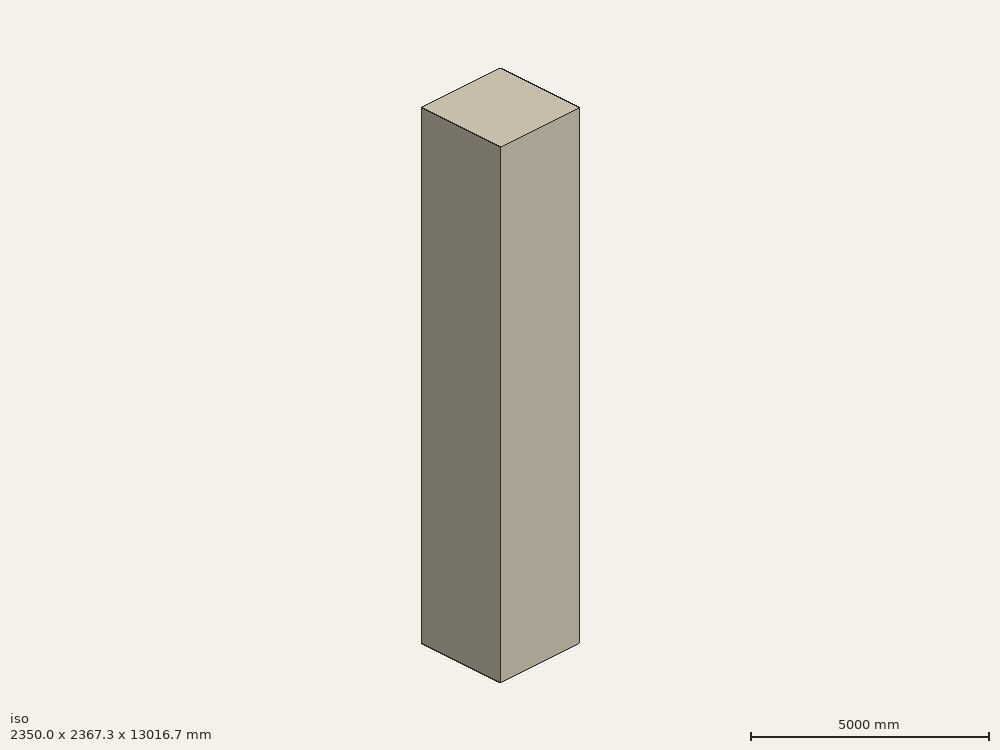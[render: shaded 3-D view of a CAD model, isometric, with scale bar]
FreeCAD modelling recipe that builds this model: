
FCSTD DOCUMENT  (FreeCAD 1.0R39109 (Git))
Label: revolveTester-6-a
License: All rights reserved
objects: App::DocumentObjectGroupPython×1252, Spreadsheet::Sheet×2, App::Part×2, Part::FeaturePython×1, Part::Cylinder×1, Sketcher::SketchObject×1, Part::Revolution×1, Part::Cut×1
note: 6 computed .brp shape members not serialized (recipe doc carries the construction recipe); baked Part::Feature solids carry a one-line shape summary decoded from their .brp

FEATURE [Spreadsheet::Sheet] defines
  cells = A1='constant; B1='HALFPI; C1(HALFPI)==pi / 2; A2='constant; B2='PI; C2(PI)==1 * pi; A3='constant; B3='TWOPI; C3(TWOPI)==2 * pi
FEATURE [Spreadsheet::Sheet] gdmlInfo
FEATURE [App::DocumentObjectGroupPython] Define  # scripted group (container) (typed FeaturePython)
  Group = -> [defines,gdmlInfo]
FEATURE [App::DocumentObjectGroupPython] HALFPI  # scripted group (container) (typed FeaturePython)
  name = HALFPI
  value = pi/2.
FEATURE [App::DocumentObjectGroupPython] PI  # scripted group (container) (typed FeaturePython)
  name = PI
  value = 1.*pi
FEATURE [App::DocumentObjectGroupPython] TWOPI  # scripted group (container) (typed FeaturePython)
  name = TWOPI
  value = 2.*pi
FEATURE [App::DocumentObjectGroupPython] Constants  # scripted group (container) (typed FeaturePython)
  Group = -> [HALFPI,PI,TWOPI]
FEATURE [App::DocumentObjectGroupPython] Quantities  # scripted group (container) (typed FeaturePython)
FEATURE [App::DocumentObjectGroupPython] Variables  # scripted group (container) (typed FeaturePython)
FEATURE [App::DocumentObjectGroupPython] Isotopes  # scripted group (container) (typed FeaturePython)
FEATURE [App::DocumentObjectGroupPython] Elements  # scripted group (container) (typed FeaturePython)
FEATURE [App::DocumentObjectGroupPython] Matrix  # scripted group (container) (typed FeaturePython)
FEATURE [App::DocumentObjectGroupPython] Surfaces  # scripted group (container) (typed FeaturePython)
FEATURE [App::DocumentObjectGroupPython] Opticals  # scripted group (container) (typed FeaturePython)
  Group = -> [Matrix,Surfaces]
FEATURE [App::DocumentObjectGroupPython] G4Isotopes  # scripted group (container) (typed FeaturePython)
FEATURE [App::DocumentObjectGroupPython] H_element  # scripted group (container) (typed FeaturePython)
  Z = 1
  atom_value = 1.008
  formula = H
  name = H_element
FEATURE [App::DocumentObjectGroupPython] He_element  # scripted group (container) (typed FeaturePython)
  Z = 2
  atom_value = 4.0026
  formula = He
  name = He_element
FEATURE [App::DocumentObjectGroupPython] Li_element  # scripted group (container) (typed FeaturePython)
  Z = 3
  atom_value = 6.94
  formula = Li
  name = Li_element
FEATURE [App::DocumentObjectGroupPython] Be_element  # scripted group (container) (typed FeaturePython)
  Z = 4
  atom_value = 9.01218
  formula = Be
  name = Be_element
FEATURE [App::DocumentObjectGroupPython] B_element  # scripted group (container) (typed FeaturePython)
  Z = 5
  atom_value = 10.81
  formula = B
  name = B_element
FEATURE [App::DocumentObjectGroupPython] C_element  # scripted group (container) (typed FeaturePython)
  Z = 6
  atom_value = 12.011
  formula = C
  name = C_element
FEATURE [App::DocumentObjectGroupPython] N_element  # scripted group (container) (typed FeaturePython)
  Z = 7
  atom_value = 14.007
  formula = N
  name = N_element
FEATURE [App::DocumentObjectGroupPython] O_element  # scripted group (container) (typed FeaturePython)
  Z = 8
  atom_value = 15.999
  formula = O
  name = O_element
FEATURE [App::DocumentObjectGroupPython] F_element  # scripted group (container) (typed FeaturePython)
  Z = 9
  atom_value = 18.9984
  formula = F
  name = F_element
FEATURE [App::DocumentObjectGroupPython] Ne_element  # scripted group (container) (typed FeaturePython)
  Z = 10
  atom_value = 20.1797
  formula = Ne
  name = Ne_element
FEATURE [App::DocumentObjectGroupPython] Na_element  # scripted group (container) (typed FeaturePython)
  Z = 11
  atom_value = 22.9898
  formula = Na
  name = Na_element
FEATURE [App::DocumentObjectGroupPython] Mg_element  # scripted group (container) (typed FeaturePython)
  Z = 12
  atom_value = 24.305
  formula = Mg
  name = Mg_element
FEATURE [App::DocumentObjectGroupPython] Al_element  # scripted group (container) (typed FeaturePython)
  Z = 13
  atom_value = 26.9815
  formula = Al
  name = Al_element
FEATURE [App::DocumentObjectGroupPython] Si_element  # scripted group (container) (typed FeaturePython)
  Z = 14
  atom_value = 28.085
  formula = Si
  name = Si_element
FEATURE [App::DocumentObjectGroupPython] P_element  # scripted group (container) (typed FeaturePython)
  Z = 15
  atom_value = 30.9738
  formula = P
  name = P_element
FEATURE [App::DocumentObjectGroupPython] S_element  # scripted group (container) (typed FeaturePython)
  Z = 16
  atom_value = 32.06
  formula = S
  name = S_element
FEATURE [App::DocumentObjectGroupPython] Cl_element  # scripted group (container) (typed FeaturePython)
  Z = 17
  atom_value = 35.45
  formula = Cl
  name = Cl_element
FEATURE [App::DocumentObjectGroupPython] Ar_element  # scripted group (container) (typed FeaturePython)
  Z = 18
  atom_value = 39.95
  formula = Ar
  name = Ar_element
FEATURE [App::DocumentObjectGroupPython] K_element  # scripted group (container) (typed FeaturePython)
  Z = 19
  atom_value = 39.0983
  formula = K
  name = K_element
FEATURE [App::DocumentObjectGroupPython] Ca_element  # scripted group (container) (typed FeaturePython)
  Z = 20
  atom_value = 40.078
  formula = Ca
  name = Ca_element
FEATURE [App::DocumentObjectGroupPython] Sc_element  # scripted group (container) (typed FeaturePython)
  Z = 21
  atom_value = 44.9559
  formula = Sc
  name = Sc_element
FEATURE [App::DocumentObjectGroupPython] Ti_element  # scripted group (container) (typed FeaturePython)
  Z = 22
  atom_value = 47.867
  formula = Ti
  name = Ti_element
FEATURE [App::DocumentObjectGroupPython] V_element  # scripted group (container) (typed FeaturePython)
  Z = 23
  atom_value = 50.9415
  formula = V
  name = V_element
FEATURE [App::DocumentObjectGroupPython] Cr_element  # scripted group (container) (typed FeaturePython)
  Z = 24
  atom_value = 51.9961
  formula = Cr
  name = Cr_element
FEATURE [App::DocumentObjectGroupPython] Mn_element  # scripted group (container) (typed FeaturePython)
  Z = 25
  atom_value = 54.938
  formula = Mn
  name = Mn_element
FEATURE [App::DocumentObjectGroupPython] Fe_element  # scripted group (container) (typed FeaturePython)
  Z = 26
  atom_value = 55.845
  formula = Fe
  name = Fe_element
FEATURE [App::DocumentObjectGroupPython] Co_element  # scripted group (container) (typed FeaturePython)
  Z = 27
  atom_value = 58.9332
  formula = Co
  name = Co_element
FEATURE [App::DocumentObjectGroupPython] Ni_element  # scripted group (container) (typed FeaturePython)
  Z = 28
  atom_value = 58.6934
  formula = Ni
  name = Ni_element
FEATURE [App::DocumentObjectGroupPython] Cu_element  # scripted group (container) (typed FeaturePython)
  Z = 29
  atom_value = 63.546
  formula = Cu
  name = Cu_element
FEATURE [App::DocumentObjectGroupPython] Zn_element  # scripted group (container) (typed FeaturePython)
  Z = 30
  atom_value = 65.38
  formula = Zn
  name = Zn_element
FEATURE [App::DocumentObjectGroupPython] Ga_element  # scripted group (container) (typed FeaturePython)
  Z = 31
  atom_value = 69.723
  formula = Ga
  name = Ga_element
FEATURE [App::DocumentObjectGroupPython] Ge_element  # scripted group (container) (typed FeaturePython)
  Z = 32
  atom_value = 72.63
  formula = Ge
  name = Ge_element
FEATURE [App::DocumentObjectGroupPython] As_element  # scripted group (container) (typed FeaturePython)
  Z = 33
  atom_value = 74.9216
  formula = As
  name = As_element
FEATURE [App::DocumentObjectGroupPython] Se_element  # scripted group (container) (typed FeaturePython)
  Z = 34
  atom_value = 78.971
  formula = Se
  name = Se_element
FEATURE [App::DocumentObjectGroupPython] Br_element  # scripted group (container) (typed FeaturePython)
  Z = 35
  atom_value = 79.904
  formula = Br
  name = Br_element
FEATURE [App::DocumentObjectGroupPython] Kr_element  # scripted group (container) (typed FeaturePython)
  Z = 36
  atom_value = 83.798
  formula = Kr
  name = Kr_element
FEATURE [App::DocumentObjectGroupPython] Rb_element  # scripted group (container) (typed FeaturePython)
  Z = 37
  atom_value = 85.4678
  formula = Rb
  name = Rb_element
FEATURE [App::DocumentObjectGroupPython] Sr_element  # scripted group (container) (typed FeaturePython)
  Z = 38
  atom_value = 87.62
  formula = Sr
  name = Sr_element
FEATURE [App::DocumentObjectGroupPython] Y_element  # scripted group (container) (typed FeaturePython)
  Z = 39
  atom_value = 88.9058
  formula = Y
  name = Y_element
FEATURE [App::DocumentObjectGroupPython] Zr_element  # scripted group (container) (typed FeaturePython)
  Z = 40
  atom_value = 91.224
  formula = Zr
  name = Zr_element
FEATURE [App::DocumentObjectGroupPython] Nb_element  # scripted group (container) (typed FeaturePython)
  Z = 41
  atom_value = 92.9064
  formula = Nb
  name = Nb_element
FEATURE [App::DocumentObjectGroupPython] Mo_element  # scripted group (container) (typed FeaturePython)
  Z = 42
  atom_value = 95.95
  formula = Mo
  name = Mo_element
FEATURE [App::DocumentObjectGroupPython] Tc_element  # scripted group (container) (typed FeaturePython)
  Z = 43
  atom_value = 97
  formula = Tc
  name = Tc_element
FEATURE [App::DocumentObjectGroupPython] Ru_element  # scripted group (container) (typed FeaturePython)
  Z = 44
  atom_value = 101.07
  formula = Ru
  name = Ru_element
FEATURE [App::DocumentObjectGroupPython] Rh_element  # scripted group (container) (typed FeaturePython)
  Z = 45
  atom_value = 102.905
  formula = Rh
  name = Rh_element
FEATURE [App::DocumentObjectGroupPython] Pd_element  # scripted group (container) (typed FeaturePython)
  Z = 46
  atom_value = 106.42
  formula = Pd
  name = Pd_element
FEATURE [App::DocumentObjectGroupPython] Ag_element  # scripted group (container) (typed FeaturePython)
  Z = 47
  atom_value = 107.868
  formula = Ag
  name = Ag_element
FEATURE [App::DocumentObjectGroupPython] Cd_element  # scripted group (container) (typed FeaturePython)
  Z = 48
  atom_value = 112.414
  formula = Cd
  name = Cd_element
FEATURE [App::DocumentObjectGroupPython] In_element  # scripted group (container) (typed FeaturePython)
  Z = 49
  atom_value = 114.818
  formula = In
  name = In_element
FEATURE [App::DocumentObjectGroupPython] Sn_element  # scripted group (container) (typed FeaturePython)
  Z = 50
  atom_value = 118.71
  formula = Sn
  name = Sn_element
FEATURE [App::DocumentObjectGroupPython] Sb_element  # scripted group (container) (typed FeaturePython)
  Z = 51
  atom_value = 121.76
  formula = Sb
  name = Sb_element
FEATURE [App::DocumentObjectGroupPython] Te_element  # scripted group (container) (typed FeaturePython)
  Z = 52
  atom_value = 127.6
  formula = Te
  name = Te_element
FEATURE [App::DocumentObjectGroupPython] I_element  # scripted group (container) (typed FeaturePython)
  Z = 53
  atom_value = 126.904
  formula = I
  name = I_element
FEATURE [App::DocumentObjectGroupPython] Xe_element  # scripted group (container) (typed FeaturePython)
  Z = 54
  atom_value = 131.293
  formula = Xe
  name = Xe_element
FEATURE [App::DocumentObjectGroupPython] Cs_element  # scripted group (container) (typed FeaturePython)
  Z = 55
  atom_value = 132.905
  formula = Cs
  name = Cs_element
FEATURE [App::DocumentObjectGroupPython] Ba_element  # scripted group (container) (typed FeaturePython)
  Z = 56
  atom_value = 137.327
  formula = Ba
  name = Ba_element
FEATURE [App::DocumentObjectGroupPython] La_element  # scripted group (container) (typed FeaturePython)
  Z = 57
  atom_value = 138.905
  formula = La
  name = La_element
FEATURE [App::DocumentObjectGroupPython] Ce_element  # scripted group (container) (typed FeaturePython)
  Z = 58
  atom_value = 140.116
  formula = Ce
  name = Ce_element
FEATURE [App::DocumentObjectGroupPython] Pr_element  # scripted group (container) (typed FeaturePython)
  Z = 59
  atom_value = 140.908
  formula = Pr
  name = Pr_element
FEATURE [App::DocumentObjectGroupPython] Nd_element  # scripted group (container) (typed FeaturePython)
  Z = 60
  atom_value = 144.242
  formula = Nd
  name = Nd_element
FEATURE [App::DocumentObjectGroupPython] Pm_element  # scripted group (container) (typed FeaturePython)
  Z = 61
  atom_value = 145
  formula = Pm
  name = Pm_element
FEATURE [App::DocumentObjectGroupPython] Sm_element  # scripted group (container) (typed FeaturePython)
  Z = 62
  atom_value = 150.36
  formula = Sm
  name = Sm_element
FEATURE [App::DocumentObjectGroupPython] Eu_element  # scripted group (container) (typed FeaturePython)
  Z = 63
  atom_value = 151.964
  formula = Eu
  name = Eu_element
FEATURE [App::DocumentObjectGroupPython] Gd_element  # scripted group (container) (typed FeaturePython)
  Z = 64
  atom_value = 157.25
  formula = Gd
  name = Gd_element
FEATURE [App::DocumentObjectGroupPython] Tb_element  # scripted group (container) (typed FeaturePython)
  Z = 65
  atom_value = 158.925
  formula = Tb
  name = Tb_element
FEATURE [App::DocumentObjectGroupPython] Dy_element  # scripted group (container) (typed FeaturePython)
  Z = 66
  atom_value = 162.5
  formula = Dy
  name = Dy_element
FEATURE [App::DocumentObjectGroupPython] Ho_element  # scripted group (container) (typed FeaturePython)
  Z = 67
  atom_value = 164.93
  formula = Ho
  name = Ho_element
FEATURE [App::DocumentObjectGroupPython] Er_element  # scripted group (container) (typed FeaturePython)
  Z = 68
  atom_value = 167.259
  formula = Er
  name = Er_element
FEATURE [App::DocumentObjectGroupPython] Tm_element  # scripted group (container) (typed FeaturePython)
  Z = 69
  atom_value = 168.934
  formula = Tm
  name = Tm_element
FEATURE [App::DocumentObjectGroupPython] Yb_element  # scripted group (container) (typed FeaturePython)
  Z = 70
  atom_value = 173.045
  formula = Yb
  name = Yb_element
FEATURE [App::DocumentObjectGroupPython] Lu_element  # scripted group (container) (typed FeaturePython)
  Z = 71
  atom_value = 174.967
  formula = Lu
  name = Lu_element
FEATURE [App::DocumentObjectGroupPython] Hf_element  # scripted group (container) (typed FeaturePython)
  Z = 72
  atom_value = 178.49
  formula = Hf
  name = Hf_element
FEATURE [App::DocumentObjectGroupPython] Ta_element  # scripted group (container) (typed FeaturePython)
  Z = 73
  atom_value = 180.948
  formula = Ta
  name = Ta_element
FEATURE [App::DocumentObjectGroupPython] W_element  # scripted group (container) (typed FeaturePython)
  Z = 74
  atom_value = 183.84
  formula = W
  name = W_element
FEATURE [App::DocumentObjectGroupPython] Re_element  # scripted group (container) (typed FeaturePython)
  Z = 75
  atom_value = 186.207
  formula = Re
  name = Re_element
FEATURE [App::DocumentObjectGroupPython] Os_element  # scripted group (container) (typed FeaturePython)
  Z = 76
  atom_value = 190.23
  formula = Os
  name = Os_element
FEATURE [App::DocumentObjectGroupPython] Ir_element  # scripted group (container) (typed FeaturePython)
  Z = 77
  atom_value = 192.217
  formula = Ir
  name = Ir_element
FEATURE [App::DocumentObjectGroupPython] Pt_element  # scripted group (container) (typed FeaturePython)
  Z = 78
  atom_value = 195.084
  formula = Pt
  name = Pt_element
FEATURE [App::DocumentObjectGroupPython] Au_element  # scripted group (container) (typed FeaturePython)
  Z = 79
  atom_value = 196.967
  formula = Au
  name = Au_element
FEATURE [App::DocumentObjectGroupPython] Hg_element  # scripted group (container) (typed FeaturePython)
  Z = 80
  atom_value = 200.592
  formula = Hg
  name = Hg_element
FEATURE [App::DocumentObjectGroupPython] Tl_element  # scripted group (container) (typed FeaturePython)
  Z = 81
  atom_value = 204.38
  formula = Tl
  name = Tl_element
FEATURE [App::DocumentObjectGroupPython] Pb_element  # scripted group (container) (typed FeaturePython)
  Z = 82
  atom_value = 207.2
  formula = Pb
  name = Pb_element
FEATURE [App::DocumentObjectGroupPython] Bi_element  # scripted group (container) (typed FeaturePython)
  Z = 83
  atom_value = 208.98
  formula = Bi
  name = Bi_element
FEATURE [App::DocumentObjectGroupPython] Po_element  # scripted group (container) (typed FeaturePython)
  Z = 84
  atom_value = 209
  formula = Po
  name = Po_element
FEATURE [App::DocumentObjectGroupPython] At_element  # scripted group (container) (typed FeaturePython)
  Z = 85
  atom_value = 210
  formula = At
  name = At_element
FEATURE [App::DocumentObjectGroupPython] Rn_element  # scripted group (container) (typed FeaturePython)
  Z = 86
  atom_value = 222
  formula = Rn
  name = Rn_element
FEATURE [App::DocumentObjectGroupPython] Fr_element  # scripted group (container) (typed FeaturePython)
  Z = 87
  atom_value = 223
  formula = Fr
  name = Fr_element
FEATURE [App::DocumentObjectGroupPython] Ra_element  # scripted group (container) (typed FeaturePython)
  Z = 88
  atom_value = 226
  formula = Ra
  name = Ra_element
FEATURE [App::DocumentObjectGroupPython] Ac_element  # scripted group (container) (typed FeaturePython)
  Z = 89
  atom_value = 227
  formula = Ac
  name = Ac_element
FEATURE [App::DocumentObjectGroupPython] Th_element  # scripted group (container) (typed FeaturePython)
  Z = 90
  atom_value = 232.038
  formula = Th
  name = Th_element
FEATURE [App::DocumentObjectGroupPython] Pa_element  # scripted group (container) (typed FeaturePython)
  Z = 91
  atom_value = 231.036
  formula = Pa
  name = Pa_element
FEATURE [App::DocumentObjectGroupPython] U_element  # scripted group (container) (typed FeaturePython)
  Z = 92
  atom_value = 238.029
  formula = U
  name = U_element
FEATURE [App::DocumentObjectGroupPython] Np_element  # scripted group (container) (typed FeaturePython)
  Z = 93
  atom_value = 237
  formula = Np
  name = Np_element
FEATURE [App::DocumentObjectGroupPython] Pu_element  # scripted group (container) (typed FeaturePython)
  Z = 94
  atom_value = 244
  formula = Pu
  name = Pu_element
FEATURE [App::DocumentObjectGroupPython] Am_element  # scripted group (container) (typed FeaturePython)
  Z = 95
  atom_value = 243
  formula = Am
  name = Am_element
FEATURE [App::DocumentObjectGroupPython] Cm_element  # scripted group (container) (typed FeaturePython)
  Z = 96
  atom_value = 247
  formula = Cm
  name = Cm_element
FEATURE [App::DocumentObjectGroupPython] Bk_element  # scripted group (container) (typed FeaturePython)
  Z = 97
  atom_value = 247
  formula = Bk
  name = Bk_element
FEATURE [App::DocumentObjectGroupPython] Cf_element  # scripted group (container) (typed FeaturePython)
  Z = 98
  atom_value = 251
  formula = Cf
  name = Cf_element
FEATURE [App::DocumentObjectGroupPython] G4Elements  # scripted group (container) (typed FeaturePython)
  Group = -> [H_element,He_element,Li_element,Be_element,B_element,C_element,N_element,O_element,F_element,Ne_element,Na_element,Mg_element,Al_element,Si_element,P_element,S_element,Cl_element,Ar_element,K_element,Ca_element,Sc_element,Ti_element,V_element,Cr_element,Mn_element,Fe_element,Co_element,Ni_element,Cu_element,Zn_element,Ga_element,Ge_element,As_element,Se_element,Br_element,Kr_element,Rb_element,+61 more]
FEATURE [App::DocumentObjectGroupPython] H_element001  label="H_element : 0.101"  # scripted group (container) (typed FeaturePython)
  n = 0.101327
FEATURE [App::DocumentObjectGroupPython] C_element001  label="C_element : 0.775"  # scripted group (container) (typed FeaturePython)
  n = 0.7755
FEATURE [App::DocumentObjectGroupPython] N_element001  label="N_element : 0.035"  # scripted group (container) (typed FeaturePython)
  n = 0.035057
FEATURE [App::DocumentObjectGroupPython] O_element001  label="O_element : 0.052"  # scripted group (container) (typed FeaturePython)
  n = 0.0523159
FEATURE [App::DocumentObjectGroupPython] F_element001  label="F_element : 0.017"  # scripted group (container) (typed FeaturePython)
  n = 0.017422
FEATURE [App::DocumentObjectGroupPython] Ca_element001  label="Ca_element : 0.018"  # scripted group (container) (typed FeaturePython)
  n = 0.018378
FEATURE [App::DocumentObjectGroupPython] G4_A_150_TISSUE  label="G4_A-150_TISSUE"  # scripted group (container) (typed FeaturePython)
  Dunit = g/cm3
  Dvalue = 1.127
  Group = -> [H_element001,C_element001,N_element001,O_element001,F_element001,Ca_element001]
  conduct = 2
  density = 1
  expand = 3
  formula = G4_A-150_TISSUE
  name = G4_A-150_TISSUE
  specific = 4
FEATURE [App::DocumentObjectGroupPython] C_element002  label="C_element : 3"  # scripted group (container) (typed FeaturePython)
  n = 3
  ref = C_element
FEATURE [App::DocumentObjectGroupPython] H_element002  label="H_element : 6"  # scripted group (container) (typed FeaturePython)
  n = 6
  ref = H_element
FEATURE [App::DocumentObjectGroupPython] O_element002  label="O_element : 1"  # scripted group (container) (typed FeaturePython)
  n = 1
  ref = O_element
FEATURE [App::DocumentObjectGroupPython] G4_ACETONE  # scripted group (container) (typed FeaturePython)
  Dunit = g/cm3
  Dvalue = 0.7899
  Group = -> [C_element002,H_element002,O_element002]
  conduct = 2
  density = 1
  expand = 3
  formula = G4_ACETONE
  name = G4_ACETONE
  specific = 4
FEATURE [App::DocumentObjectGroupPython] C_element003  label="C_element : 2"  # scripted group (container) (typed FeaturePython)
  n = 2
  ref = C_element
FEATURE [App::DocumentObjectGroupPython] H_element003  label="H_element : 2"  # scripted group (container) (typed FeaturePython)
  n = 2
  ref = H_element
FEATURE [App::DocumentObjectGroupPython] G4_ACETYLENE  # scripted group (container) (typed FeaturePython)
  Dunit = g/cm3
  Dvalue = 0.0010967
  Group = -> [C_element003,H_element003]
  conduct = 2
  density = 1
  expand = 3
  formula = G4_ACETYLENE
  name = G4_ACETYLENE
  specific = 4
FEATURE [App::DocumentObjectGroupPython] C_element004  label="C_element : 5"  # scripted group (container) (typed FeaturePython)
  n = 5
  ref = C_element
FEATURE [App::DocumentObjectGroupPython] H_element004  label="H_element : 5"  # scripted group (container) (typed FeaturePython)
  n = 5
  ref = H_element
FEATURE [App::DocumentObjectGroupPython] N_element002  label="N_element : 5"  # scripted group (container) (typed FeaturePython)
  n = 5
  ref = N_element
FEATURE [App::DocumentObjectGroupPython] G4_ADENINE  # scripted group (container) (typed FeaturePython)
  Dunit = g/cm3
  Dvalue = 1.6
  Group = -> [C_element004,H_element004,N_element002]
  conduct = 2
  density = 1
  expand = 3
  formula = G4_ADENINE
  name = G4_ADENINE
  specific = 4
FEATURE [App::DocumentObjectGroupPython] H_element005  label="H_element : 0.114"  # scripted group (container) (typed FeaturePython)
  n = 0.114
FEATURE [App::DocumentObjectGroupPython] C_element005  label="C_element : 0.598"  # scripted group (container) (typed FeaturePython)
  n = 0.598
FEATURE [App::DocumentObjectGroupPython] N_element003  label="N_element : 0.007"  # scripted group (container) (typed FeaturePython)
  n = 0.007
FEATURE [App::DocumentObjectGroupPython] O_element003  label="O_element : 0.278"  # scripted group (container) (typed FeaturePython)
  n = 0.278
FEATURE [App::DocumentObjectGroupPython] Na_element001  label="Na_element : 0.001"  # scripted group (container) (typed FeaturePython)
  n = 0.001
FEATURE [App::DocumentObjectGroupPython] S_element001  label="S_element : 0.001"  # scripted group (container) (typed FeaturePython)
  n = 0.001
FEATURE [App::DocumentObjectGroupPython] Cl_element001  label="Cl_element : 0.001"  # scripted group (container) (typed FeaturePython)
  n = 0.001
FEATURE [App::DocumentObjectGroupPython] G4_ADIPOSE_TISSUE_ICRP  # scripted group (container) (typed FeaturePython)
  Dunit = g/cm3
  Dvalue = 0.95
  Group = -> [H_element005,C_element005,N_element003,O_element003,Na_element001,S_element001,Cl_element001]
  conduct = 2
  density = 1
  expand = 3
  formula = G4_ADIPOSE_TISSUE_ICRP
  name = G4_ADIPOSE_TISSUE_ICRP
  specific = 4
FEATURE [App::DocumentObjectGroupPython] C_element006  label="C_element : 0.000"  # scripted group (container) (typed FeaturePython)
  n = 0.000124
FEATURE [App::DocumentObjectGroupPython] N_element004  label="N_element : 0.755"  # scripted group (container) (typed FeaturePython)
  n = 0.755268
FEATURE [App::DocumentObjectGroupPython] O_element004  label="O_element : 0.232"  # scripted group (container) (typed FeaturePython)
  n = 0.231781
FEATURE [App::DocumentObjectGroupPython] Ar_element001  label="Ar_element : 0.013"  # scripted group (container) (typed FeaturePython)
  n = 0.012827
FEATURE [App::DocumentObjectGroupPython] G4_AIR  # scripted group (container) (typed FeaturePython)
  Dunit = g/cm3
  Dvalue = 0.00120479
  Group = -> [C_element006,N_element004,O_element004,Ar_element001]
  conduct = 2
  density = 1
  expand = 3
  formula = G4_AIR
  name = G4_AIR
  specific = 4
FEATURE [App::DocumentObjectGroupPython] C_element007  label="C_element : 006"  # scripted group (container) (typed FeaturePython)
  n = 3
  ref = C_element
FEATURE [App::DocumentObjectGroupPython] H_element006  label="H_element : 7"  # scripted group (container) (typed FeaturePython)
  n = 7
  ref = H_element
FEATURE [App::DocumentObjectGroupPython] N_element005  label="N_element : 1"  # scripted group (container) (typed FeaturePython)
  n = 1
  ref = N_element
FEATURE [App::DocumentObjectGroupPython] O_element005  label="O_element : 2"  # scripted group (container) (typed FeaturePython)
  n = 2
  ref = O_element
FEATURE [App::DocumentObjectGroupPython] G4_ALANINE  # scripted group (container) (typed FeaturePython)
  Dunit = g/cm3
  Dvalue = 1.42
  Group = -> [C_element007,H_element006,N_element005,O_element005]
  conduct = 2
  density = 1
  expand = 3
  formula = G4_ALANINE
  name = G4_ALANINE
  specific = 4
FEATURE [App::DocumentObjectGroupPython] Al_element001  label="Al_element : 2"  # scripted group (container) (typed FeaturePython)
  n = 2
  ref = Al_element
FEATURE [App::DocumentObjectGroupPython] O_element006  label="O_element : 3"  # scripted group (container) (typed FeaturePython)
  n = 3
  ref = O_element
FEATURE [App::DocumentObjectGroupPython] G4_ALUMINUM_OXIDE  # scripted group (container) (typed FeaturePython)
  Dunit = g/cm3
  Dvalue = 3.97
  Group = -> [Al_element001,O_element006]
  conduct = 2
  density = 1
  expand = 3
  formula = G4_ALUMINUM_OXIDE
  name = G4_ALUMINUM_OXIDE
  specific = 4
FEATURE [App::DocumentObjectGroupPython] H_element007  label="H_element : 0.106"  # scripted group (container) (typed FeaturePython)
  n = 0.10593
FEATURE [App::DocumentObjectGroupPython] C_element008  label="C_element : 0.789"  # scripted group (container) (typed FeaturePython)
  n = 0.788974
FEATURE [App::DocumentObjectGroupPython] O_element007  label="O_element : 0.105"  # scripted group (container) (typed FeaturePython)
  n = 0.105096
FEATURE [App::DocumentObjectGroupPython] G4_AMBER  # scripted group (container) (typed FeaturePython)
  Dunit = g/cm3
  Dvalue = 1.1
  Group = -> [H_element007,C_element008,O_element007]
  conduct = 2
  density = 1
  expand = 3
  formula = G4_AMBER
  name = G4_AMBER
  specific = 4
FEATURE [App::DocumentObjectGroupPython] N_element006  label="N_element : 006"  # scripted group (container) (typed FeaturePython)
  n = 1
  ref = N_element
FEATURE [App::DocumentObjectGroupPython] H_element008  label="H_element : 3"  # scripted group (container) (typed FeaturePython)
  n = 3
  ref = H_element
FEATURE [App::DocumentObjectGroupPython] G4_AMMONIA  # scripted group (container) (typed FeaturePython)
  Dunit = g/cm3
  Dvalue = 0.000826019
  Group = -> [N_element006,H_element008]
  conduct = 2
  density = 1
  expand = 3
  formula = G4_AMMONIA
  name = G4_AMMONIA
  specific = 4
FEATURE [App::DocumentObjectGroupPython] C_element009  label="C_element : 6"  # scripted group (container) (typed FeaturePython)
  n = 6
  ref = C_element
FEATURE [App::DocumentObjectGroupPython] H_element009  label="H_element : 008"  # scripted group (container) (typed FeaturePython)
  n = 7
  ref = H_element
FEATURE [App::DocumentObjectGroupPython] N_element007  label="N_element : 007"  # scripted group (container) (typed FeaturePython)
  n = 1
  ref = N_element
FEATURE [App::DocumentObjectGroupPython] G4_ANILINE  # scripted group (container) (typed FeaturePython)
  Dunit = g/cm3
  Dvalue = 1.0235
  Group = -> [C_element009,H_element009,N_element007]
  conduct = 2
  density = 1
  expand = 3
  formula = G4_ANILINE
  name = G4_ANILINE
  specific = 4
FEATURE [App::DocumentObjectGroupPython] C_element010  label="C_element : 14"  # scripted group (container) (typed FeaturePython)
  n = 14
  ref = C_element
FEATURE [App::DocumentObjectGroupPython] H_element010  label="H_element : 10"  # scripted group (container) (typed FeaturePython)
  n = 10
  ref = H_element
FEATURE [App::DocumentObjectGroupPython] G4_ANTHRACENE  # scripted group (container) (typed FeaturePython)
  Dunit = g/cm3
  Dvalue = 1.283
  Group = -> [C_element010,H_element010]
  conduct = 2
  density = 1
  expand = 3
  formula = G4_ANTHRACENE
  name = G4_ANTHRACENE
  specific = 4
FEATURE [App::DocumentObjectGroupPython] H_element011  label="H_element : 0.065"  # scripted group (container) (typed FeaturePython)
  n = 0.0654709
FEATURE [App::DocumentObjectGroupPython] C_element011  label="C_element : 0.537"  # scripted group (container) (typed FeaturePython)
  n = 0.536944
FEATURE [App::DocumentObjectGroupPython] N_element008  label="N_element : 0.021"  # scripted group (container) (typed FeaturePython)
  n = 0.0215
FEATURE [App::DocumentObjectGroupPython] O_element008  label="O_element : 0.032"  # scripted group (container) (typed FeaturePython)
  n = 0.032085
FEATURE [App::DocumentObjectGroupPython] F_element002  label="F_element : 0.167"  # scripted group (container) (typed FeaturePython)
  n = 0.167411
FEATURE [App::DocumentObjectGroupPython] Ca_element002  label="Ca_element : 0.177"  # scripted group (container) (typed FeaturePython)
  n = 0.176589
FEATURE [App::DocumentObjectGroupPython] G4_B_100_BONE  label="G4_B-100_BONE"  # scripted group (container) (typed FeaturePython)
  Dunit = g/cm3
  Dvalue = 1.45
  Group = -> [H_element011,C_element011,N_element008,O_element008,F_element002,Ca_element002]
  conduct = 2
  density = 1
  expand = 3
  formula = G4_B-100_BONE
  name = G4_B-100_BONE
  specific = 4
FEATURE [App::DocumentObjectGroupPython] H_element012  label="H_element : 0.057"  # scripted group (container) (typed FeaturePython)
  n = 0.057441
FEATURE [App::DocumentObjectGroupPython] C_element012  label="C_element : 0.790"  # scripted group (container) (typed FeaturePython)
  n = 0.774591
FEATURE [App::DocumentObjectGroupPython] O_element009  label="O_element : 0.168"  # scripted group (container) (typed FeaturePython)
  n = 0.167968
FEATURE [App::DocumentObjectGroupPython] G4_BAKELITE  # scripted group (container) (typed FeaturePython)
  Dunit = g/cm3
  Dvalue = 1.25
  Group = -> [H_element012,C_element012,O_element009]
  conduct = 2
  density = 1
  expand = 3
  formula = G4_BAKELITE
  name = G4_BAKELITE
  specific = 4
FEATURE [App::DocumentObjectGroupPython] Ba_element001  label="Ba_element : 1"  # scripted group (container) (typed FeaturePython)
  n = 1
  ref = Ba_element
FEATURE [App::DocumentObjectGroupPython] F_element003  label="F_element : 2"  # scripted group (container) (typed FeaturePython)
  n = 2
  ref = F_element
FEATURE [App::DocumentObjectGroupPython] G4_BARIUM_FLUORIDE  # scripted group (container) (typed FeaturePython)
  Dunit = g/cm3
  Dvalue = 4.89
  Group = -> [Ba_element001,F_element003]
  conduct = 2
  density = 1
  expand = 3
  formula = G4_BARIUM_FLUORIDE
  name = G4_BARIUM_FLUORIDE
  specific = 4
FEATURE [App::DocumentObjectGroupPython] Ba_element002  label="Ba_element : 002"  # scripted group (container) (typed FeaturePython)
  n = 1
  ref = Ba_element
FEATURE [App::DocumentObjectGroupPython] S_element002  label="S_element : 1"  # scripted group (container) (typed FeaturePython)
  n = 1
  ref = S_element
FEATURE [App::DocumentObjectGroupPython] O_element010  label="O_element : 4"  # scripted group (container) (typed FeaturePython)
  n = 4
  ref = O_element
FEATURE [App::DocumentObjectGroupPython] G4_BARIUM_SULFATE  # scripted group (container) (typed FeaturePython)
  Dunit = g/cm3
  Dvalue = 4.5
  Group = -> [Ba_element002,S_element002,O_element010]
  conduct = 2
  density = 1
  expand = 3
  formula = G4_BARIUM_SULFATE
  name = G4_BARIUM_SULFATE
  specific = 4
FEATURE [App::DocumentObjectGroupPython] C_element013  label="C_element : 007"  # scripted group (container) (typed FeaturePython)
  n = 6
  ref = C_element
FEATURE [App::DocumentObjectGroupPython] H_element013  label="H_element : 009"  # scripted group (container) (typed FeaturePython)
  n = 6
  ref = H_element
FEATURE [App::DocumentObjectGroupPython] G4_BENZENE  # scripted group (container) (typed FeaturePython)
  Dunit = g/cm3
  Dvalue = 0.87865
  Group = -> [C_element013,H_element013]
  conduct = 2
  density = 1
  expand = 3
  formula = G4_BENZENE
  name = G4_BENZENE
  specific = 4
FEATURE [App::DocumentObjectGroupPython] Be_element001  label="Be_element : 1"  # scripted group (container) (typed FeaturePython)
  n = 1
  ref = Be_element
FEATURE [App::DocumentObjectGroupPython] O_element011  label="O_element : 005"  # scripted group (container) (typed FeaturePython)
  n = 1
  ref = O_element
FEATURE [App::DocumentObjectGroupPython] G4_BERYLLIUM_OXIDE  # scripted group (container) (typed FeaturePython)
  Dunit = g/cm3
  Dvalue = 3.01
  Group = -> [Be_element001,O_element011]
  conduct = 2
  density = 1
  expand = 3
  formula = G4_BERYLLIUM_OXIDE
  name = G4_BERYLLIUM_OXIDE
  specific = 4
FEATURE [App::DocumentObjectGroupPython] Bi_element001  label="Bi_element : 4"  # scripted group (container) (typed FeaturePython)
  n = 4
  ref = Bi_element
FEATURE [App::DocumentObjectGroupPython] Ge_element001  label="Ge_element : 3"  # scripted group (container) (typed FeaturePython)
  n = 3
  ref = Ge_element
FEATURE [App::DocumentObjectGroupPython] O_element012  label="O_element : 12"  # scripted group (container) (typed FeaturePython)
  n = 12
  ref = O_element
FEATURE [App::DocumentObjectGroupPython] G4_BGO  # scripted group (container) (typed FeaturePython)
  Dunit = g/cm3
  Dvalue = 7.13
  Group = -> [Bi_element001,Ge_element001,O_element012]
  conduct = 2
  density = 1
  expand = 3
  formula = G4_BGO
  name = G4_BGO
  specific = 4
FEATURE [App::DocumentObjectGroupPython] H_element014  label="H_element : 0.102"  # scripted group (container) (typed FeaturePython)
  n = 0.102
FEATURE [App::DocumentObjectGroupPython] C_element014  label="C_element : 0.110"  # scripted group (container) (typed FeaturePython)
  n = 0.11
FEATURE [App::DocumentObjectGroupPython] N_element009  label="N_element : 0.033"  # scripted group (container) (typed FeaturePython)
  n = 0.033
FEATURE [App::DocumentObjectGroupPython] O_element013  label="O_element : 0.745"  # scripted group (container) (typed FeaturePython)
  n = 0.745
FEATURE [App::DocumentObjectGroupPython] Na_element002  label="Na_element : 0.002"  # scripted group (container) (typed FeaturePython)
  n = 0.001
FEATURE [App::DocumentObjectGroupPython] P_element001  label="P_element : 0.001"  # scripted group (container) (typed FeaturePython)
  n = 0.001
FEATURE [App::DocumentObjectGroupPython] S_element003  label="S_element : 0.002"  # scripted group (container) (typed FeaturePython)
  n = 0.002
FEATURE [App::DocumentObjectGroupPython] Cl_element002  label="Cl_element : 0.003"  # scripted group (container) (typed FeaturePython)
  n = 0.003
FEATURE [App::DocumentObjectGroupPython] K_element001  label="K_element : 0.002"  # scripted group (container) (typed FeaturePython)
  n = 0.002
FEATURE [App::DocumentObjectGroupPython] Fe_element001  label="Fe_element : 0.001"  # scripted group (container) (typed FeaturePython)
  n = 0.001
FEATURE [App::DocumentObjectGroupPython] G4_BLOOD_ICRP  # scripted group (container) (typed FeaturePython)
  Dunit = g/cm3
  Dvalue = 1.06
  Group = -> [H_element014,C_element014,N_element009,O_element013,Na_element002,P_element001,S_element003,Cl_element002,K_element001,Fe_element001]
  conduct = 2
  density = 1
  expand = 3
  formula = G4_BLOOD_ICRP
  name = G4_BLOOD_ICRP
  specific = 4
FEATURE [App::DocumentObjectGroupPython] H_element015  label="H_element : 0.064"  # scripted group (container) (typed FeaturePython)
  n = 0.064
FEATURE [App::DocumentObjectGroupPython] C_element015  label="C_element : 0.278"  # scripted group (container) (typed FeaturePython)
  n = 0.278
FEATURE [App::DocumentObjectGroupPython] N_element010  label="N_element : 0.027"  # scripted group (container) (typed FeaturePython)
  n = 0.027
FEATURE [App::DocumentObjectGroupPython] O_element014  label="O_element : 0.410"  # scripted group (container) (typed FeaturePython)
  n = 0.41
FEATURE [App::DocumentObjectGroupPython] Mg_element001  label="Mg_element : 0.002"  # scripted group (container) (typed FeaturePython)
  n = 0.002
FEATURE [App::DocumentObjectGroupPython] P_element002  label="P_element : 0.070"  # scripted group (container) (typed FeaturePython)
  n = 0.07
FEATURE [App::DocumentObjectGroupPython] S_element004  label="S_element : 0.003"  # scripted group (container) (typed FeaturePython)
  n = 0.002
FEATURE [App::DocumentObjectGroupPython] Ca_element003  label="Ca_element : 0.147"  # scripted group (container) (typed FeaturePython)
  n = 0.147
FEATURE [App::DocumentObjectGroupPython] G4_BONE_COMPACT_ICRU  # scripted group (container) (typed FeaturePython)
  Dunit = g/cm3
  Dvalue = 1.85
  Group = -> [H_element015,C_element015,N_element010,O_element014,Mg_element001,P_element002,S_element004,Ca_element003]
  conduct = 2
  density = 1
  expand = 3
  formula = G4_BONE_COMPACT_ICRU
  name = G4_BONE_COMPACT_ICRU
  specific = 4
FEATURE [App::DocumentObjectGroupPython] H_element016  label="H_element : 0.034"  # scripted group (container) (typed FeaturePython)
  n = 0.034
FEATURE [App::DocumentObjectGroupPython] C_element016  label="C_element : 0.155"  # scripted group (container) (typed FeaturePython)
  n = 0.155
FEATURE [App::DocumentObjectGroupPython] N_element011  label="N_element : 0.042"  # scripted group (container) (typed FeaturePython)
  n = 0.042
FEATURE [App::DocumentObjectGroupPython] O_element015  label="O_element : 0.435"  # scripted group (container) (typed FeaturePython)
  n = 0.435
FEATURE [App::DocumentObjectGroupPython] Na_element003  label="Na_element : 0.003"  # scripted group (container) (typed FeaturePython)
  n = 0.001
FEATURE [App::DocumentObjectGroupPython] Mg_element002  label="Mg_element : 0.003"  # scripted group (container) (typed FeaturePython)
  n = 0.002
FEATURE [App::DocumentObjectGroupPython] P_element003  label="P_element : 0.103"  # scripted group (container) (typed FeaturePython)
  n = 0.103
FEATURE [App::DocumentObjectGroupPython] S_element005  label="S_element : 0.004"  # scripted group (container) (typed FeaturePython)
  n = 0.003
FEATURE [App::DocumentObjectGroupPython] Ca_element004  label="Ca_element : 0.225"  # scripted group (container) (typed FeaturePython)
  n = 0.225
FEATURE [App::DocumentObjectGroupPython] G4_BONE_CORTICAL_ICRP  # scripted group (container) (typed FeaturePython)
  Dunit = g/cm3
  Dvalue = 1.92
  Group = -> [H_element016,C_element016,N_element011,O_element015,Na_element003,Mg_element002,P_element003,S_element005,Ca_element004]
  conduct = 2
  density = 1
  expand = 3
  formula = G4_BONE_CORTICAL_ICRP
  name = G4_BONE_CORTICAL_ICRP
  specific = 4
FEATURE [App::DocumentObjectGroupPython] B_element001  label="B_element : 4"  # scripted group (container) (typed FeaturePython)
  n = 4
  ref = B_element
FEATURE [App::DocumentObjectGroupPython] C_element017  label="C_element : 1"  # scripted group (container) (typed FeaturePython)
  n = 1
  ref = C_element
FEATURE [App::DocumentObjectGroupPython] G4_BORON_CARBIDE  # scripted group (container) (typed FeaturePython)
  Dunit = g/cm3
  Dvalue = 2.52
  Group = -> [B_element001,C_element017]
  conduct = 2
  density = 1
  expand = 3
  formula = G4_BORON_CARBIDE
  name = G4_BORON_CARBIDE
  specific = 4
FEATURE [App::DocumentObjectGroupPython] B_element002  label="B_element : 2"  # scripted group (container) (typed FeaturePython)
  n = 2
  ref = B_element
FEATURE [App::DocumentObjectGroupPython] O_element016  label="O_element : 006"  # scripted group (container) (typed FeaturePython)
  n = 3
  ref = O_element
FEATURE [App::DocumentObjectGroupPython] G4_BORON_OXIDE  # scripted group (container) (typed FeaturePython)
  Dunit = g/cm3
  Dvalue = 1.812
  Group = -> [B_element002,O_element016]
  conduct = 2
  density = 1
  expand = 3
  formula = G4_BORON_OXIDE
  name = G4_BORON_OXIDE
  specific = 4
FEATURE [App::DocumentObjectGroupPython] H_element017  label="H_element : 0.107"  # scripted group (container) (typed FeaturePython)
  n = 0.107
FEATURE [App::DocumentObjectGroupPython] C_element018  label="C_element : 0.145"  # scripted group (container) (typed FeaturePython)
  n = 0.145
FEATURE [App::DocumentObjectGroupPython] N_element012  label="N_element : 0.022"  # scripted group (container) (typed FeaturePython)
  n = 0.022
FEATURE [App::DocumentObjectGroupPython] O_element017  label="O_element : 0.712"  # scripted group (container) (typed FeaturePython)
  n = 0.712
FEATURE [App::DocumentObjectGroupPython] Na_element004  label="Na_element : 0.004"  # scripted group (container) (typed FeaturePython)
  n = 0.002
FEATURE [App::DocumentObjectGroupPython] P_element004  label="P_element : 0.004"  # scripted group (container) (typed FeaturePython)
  n = 0.004
FEATURE [App::DocumentObjectGroupPython] S_element006  label="S_element : 0.005"  # scripted group (container) (typed FeaturePython)
  n = 0.002
FEATURE [App::DocumentObjectGroupPython] Cl_element003  label="Cl_element : 0.004"  # scripted group (container) (typed FeaturePython)
  n = 0.003
FEATURE [App::DocumentObjectGroupPython] K_element002  label="K_element : 0.003"  # scripted group (container) (typed FeaturePython)
  n = 0.003
FEATURE [App::DocumentObjectGroupPython] G4_BRAIN_ICRP  # scripted group (container) (typed FeaturePython)
  Dunit = g/cm3
  Dvalue = 1.04
  Group = -> [H_element017,C_element018,N_element012,O_element017,Na_element004,P_element004,S_element006,Cl_element003,K_element002]
  conduct = 2
  density = 1
  expand = 3
  formula = G4_BRAIN_ICRP
  name = G4_BRAIN_ICRP
  specific = 4
FEATURE [App::DocumentObjectGroupPython] C_element019  label="C_element : 4"  # scripted group (container) (typed FeaturePython)
  n = 4
  ref = C_element
FEATURE [App::DocumentObjectGroupPython] H_element018  label="H_element : 010"  # scripted group (container) (typed FeaturePython)
  n = 10
  ref = H_element
FEATURE [App::DocumentObjectGroupPython] G4_BUTANE  # scripted group (container) (typed FeaturePython)
  Dunit = g/cm3
  Dvalue = 0.00249343
  Group = -> [C_element019,H_element018]
  conduct = 2
  density = 1
  expand = 3
  formula = G4_BUTANE
  name = G4_BUTANE
  specific = 4
FEATURE [App::DocumentObjectGroupPython] C_element020  label="C_element : 008"  # scripted group (container) (typed FeaturePython)
  n = 4
  ref = C_element
FEATURE [App::DocumentObjectGroupPython] H_element019  label="H_element : 011"  # scripted group (container) (typed FeaturePython)
  n = 10
  ref = H_element
FEATURE [App::DocumentObjectGroupPython] O_element018  label="O_element : 007"  # scripted group (container) (typed FeaturePython)
  n = 1
  ref = O_element
FEATURE [App::DocumentObjectGroupPython] G4_N_BUTYL_ALCOHOL  label="G4_N-BUTYL_ALCOHOL"  # scripted group (container) (typed FeaturePython)
  Dunit = g/cm3
  Dvalue = 0.8098
  Group = -> [C_element020,H_element019,O_element018]
  conduct = 2
  density = 1
  expand = 3
  formula = G4_N-BUTYL_ALCOHOL
  name = G4_N-BUTYL_ALCOHOL
  specific = 4
FEATURE [App::DocumentObjectGroupPython] H_element020  label="H_element : 0.025"  # scripted group (container) (typed FeaturePython)
  n = 0.02468
FEATURE [App::DocumentObjectGroupPython] C_element021  label="C_element : 0.502"  # scripted group (container) (typed FeaturePython)
  n = 0.501611
FEATURE [App::DocumentObjectGroupPython] O_element019  label="O_element : 0.005"  # scripted group (container) (typed FeaturePython)
  n = 0.004527
FEATURE [App::DocumentObjectGroupPython] F_element004  label="F_element : 0.465"  # scripted group (container) (typed FeaturePython)
  n = 0.465209
FEATURE [App::DocumentObjectGroupPython] Si_element001  label="Si_element : 0.004"  # scripted group (container) (typed FeaturePython)
  n = 0.003973
FEATURE [App::DocumentObjectGroupPython] G4_C_552  label="G4_C-552"  # scripted group (container) (typed FeaturePython)
  Dunit = g/cm3
  Dvalue = 1.76
  Group = -> [H_element020,C_element021,O_element019,F_element004,Si_element001]
  conduct = 2
  density = 1
  expand = 3
  formula = G4_C-552
  name = G4_C-552
  specific = 4
FEATURE [App::DocumentObjectGroupPython] Cd_element001  label="Cd_element : 1"  # scripted group (container) (typed FeaturePython)
  n = 1
  ref = Cd_element
FEATURE [App::DocumentObjectGroupPython] Te_element001  label="Te_element : 1"  # scripted group (container) (typed FeaturePython)
  n = 1
  ref = Te_element
FEATURE [App::DocumentObjectGroupPython] G4_CADMIUM_TELLURIDE  # scripted group (container) (typed FeaturePython)
  Dunit = g/cm3
  Dvalue = 6.2
  Group = -> [Cd_element001,Te_element001]
  conduct = 2
  density = 1
  expand = 3
  formula = G4_CADMIUM_TELLURIDE
  name = G4_CADMIUM_TELLURIDE
  specific = 4
FEATURE [App::DocumentObjectGroupPython] Cd_element002  label="Cd_element : 002"  # scripted group (container) (typed FeaturePython)
  n = 1
  ref = Cd_element
FEATURE [App::DocumentObjectGroupPython] W_element001  label="W_element : 1"  # scripted group (container) (typed FeaturePython)
  n = 1
  ref = W_element
FEATURE [App::DocumentObjectGroupPython] O_element020  label="O_element : 008"  # scripted group (container) (typed FeaturePython)
  n = 4
  ref = O_element
FEATURE [App::DocumentObjectGroupPython] G4_CADMIUM_TUNGSTATE  # scripted group (container) (typed FeaturePython)
  Dunit = g/cm3
  Dvalue = 7.9
  Group = -> [Cd_element002,W_element001,O_element020]
  conduct = 2
  density = 1
  expand = 3
  formula = G4_CADMIUM_TUNGSTATE
  name = G4_CADMIUM_TUNGSTATE
  specific = 4
FEATURE [App::DocumentObjectGroupPython] Ca_element005  label="Ca_element : 1"  # scripted group (container) (typed FeaturePython)
  n = 1
  ref = Ca_element
FEATURE [App::DocumentObjectGroupPython] C_element022  label="C_element : 009"  # scripted group (container) (typed FeaturePython)
  n = 1
  ref = C_element
FEATURE [App::DocumentObjectGroupPython] O_element021  label="O_element : 009"  # scripted group (container) (typed FeaturePython)
  n = 3
  ref = O_element
FEATURE [App::DocumentObjectGroupPython] G4_CALCIUM_CARBONATE  # scripted group (container) (typed FeaturePython)
  Dunit = g/cm3
  Dvalue = 2.8
  Group = -> [Ca_element005,C_element022,O_element021]
  conduct = 2
  density = 1
  expand = 3
  formula = G4_CALCIUM_CARBONATE
  name = G4_CALCIUM_CARBONATE
  specific = 4
FEATURE [App::DocumentObjectGroupPython] Ca_element006  label="Ca_element : 002"  # scripted group (container) (typed FeaturePython)
  n = 1
  ref = Ca_element
FEATURE [App::DocumentObjectGroupPython] F_element005  label="F_element : 003"  # scripted group (container) (typed FeaturePython)
  n = 2
  ref = F_element
FEATURE [App::DocumentObjectGroupPython] G4_CALCIUM_FLUORIDE  # scripted group (container) (typed FeaturePython)
  Dunit = g/cm3
  Dvalue = 3.18
  Group = -> [Ca_element006,F_element005]
  conduct = 2
  density = 1
  expand = 3
  formula = G4_CALCIUM_FLUORIDE
  name = G4_CALCIUM_FLUORIDE
  specific = 4
FEATURE [App::DocumentObjectGroupPython] Ca_element007  label="Ca_element : 003"  # scripted group (container) (typed FeaturePython)
  n = 1
  ref = Ca_element
FEATURE [App::DocumentObjectGroupPython] O_element022  label="O_element : 010"  # scripted group (container) (typed FeaturePython)
  n = 1
  ref = O_element
FEATURE [App::DocumentObjectGroupPython] G4_CALCIUM_OXIDE  # scripted group (container) (typed FeaturePython)
  Dunit = g/cm3
  Dvalue = 3.3
  Group = -> [Ca_element007,O_element022]
  conduct = 2
  density = 1
  expand = 3
  formula = G4_CALCIUM_OXIDE
  name = G4_CALCIUM_OXIDE
  specific = 4
FEATURE [App::DocumentObjectGroupPython] Ca_element008  label="Ca_element : 004"  # scripted group (container) (typed FeaturePython)
  n = 1
  ref = Ca_element
FEATURE [App::DocumentObjectGroupPython] S_element007  label="S_element : 002"  # scripted group (container) (typed FeaturePython)
  n = 1
  ref = S_element
FEATURE [App::DocumentObjectGroupPython] O_element023  label="O_element : 011"  # scripted group (container) (typed FeaturePython)
  n = 4
  ref = O_element
FEATURE [App::DocumentObjectGroupPython] G4_CALCIUM_SULFATE  # scripted group (container) (typed FeaturePython)
  Dunit = g/cm3
  Dvalue = 2.96
  Group = -> [Ca_element008,S_element007,O_element023]
  conduct = 2
  density = 1
  expand = 3
  formula = G4_CALCIUM_SULFATE
  name = G4_CALCIUM_SULFATE
  specific = 4
FEATURE [App::DocumentObjectGroupPython] Ca_element009  label="Ca_element : 005"  # scripted group (container) (typed FeaturePython)
  n = 1
  ref = Ca_element
FEATURE [App::DocumentObjectGroupPython] W_element002  label="W_element : 002"  # scripted group (container) (typed FeaturePython)
  n = 1
  ref = W_element
FEATURE [App::DocumentObjectGroupPython] O_element024  label="O_element : 012"  # scripted group (container) (typed FeaturePython)
  n = 4
  ref = O_element
FEATURE [App::DocumentObjectGroupPython] G4_CALCIUM_TUNGSTATE  # scripted group (container) (typed FeaturePython)
  Dunit = g/cm3
  Dvalue = 6.062
  Group = -> [Ca_element009,W_element002,O_element024]
  conduct = 2
  density = 1
  expand = 3
  formula = G4_CALCIUM_TUNGSTATE
  name = G4_CALCIUM_TUNGSTATE
  specific = 4
FEATURE [App::DocumentObjectGroupPython] C_element023  label="C_element : 010"  # scripted group (container) (typed FeaturePython)
  n = 1
  ref = C_element
FEATURE [App::DocumentObjectGroupPython] O_element025  label="O_element : 013"  # scripted group (container) (typed FeaturePython)
  n = 2
  ref = O_element
FEATURE [App::DocumentObjectGroupPython] G4_CARBON_DIOXIDE  # scripted group (container) (typed FeaturePython)
  Dunit = g/cm3
  Dvalue = 0.00184212
  Group = -> [C_element023,O_element025]
  conduct = 2
  density = 1
  expand = 3
  formula = G4_CARBON_DIOXIDE
  name = G4_CARBON_DIOXIDE
  specific = 4
FEATURE [App::DocumentObjectGroupPython] C_element024  label="C_element : 011"  # scripted group (container) (typed FeaturePython)
  n = 1
  ref = C_element
FEATURE [App::DocumentObjectGroupPython] Cl_element004  label="Cl_element : 4"  # scripted group (container) (typed FeaturePython)
  n = 4
  ref = Cl_element
FEATURE [App::DocumentObjectGroupPython] G4_CARBON_TETRACHLORIDE  # scripted group (container) (typed FeaturePython)
  Dunit = g/cm3
  Dvalue = 1.594
  Group = -> [C_element024,Cl_element004]
  conduct = 2
  density = 1
  expand = 3
  formula = G4_CARBON_TETRACHLORIDE
  name = G4_CARBON_TETRACHLORIDE
  specific = 4
FEATURE [App::DocumentObjectGroupPython] C_element025  label="C_element : 012"  # scripted group (container) (typed FeaturePython)
  n = 6
  ref = C_element
FEATURE [App::DocumentObjectGroupPython] H_element021  label="H_element : 012"  # scripted group (container) (typed FeaturePython)
  n = 10
  ref = H_element
FEATURE [App::DocumentObjectGroupPython] O_element026  label="O_element : 5"  # scripted group (container) (typed FeaturePython)
  n = 5
  ref = O_element
FEATURE [App::DocumentObjectGroupPython] G4_CELLULOSE_CELLOPHANE  # scripted group (container) (typed FeaturePython)
  Dunit = g/cm3
  Dvalue = 1.42
  Group = -> [C_element025,H_element021,O_element026]
  conduct = 2
  density = 1
  expand = 3
  formula = G4_CELLULOSE_CELLOPHANE
  name = G4_CELLULOSE_CELLOPHANE
  specific = 4
FEATURE [App::DocumentObjectGroupPython] H_element022  label="H_element : 0.067"  # scripted group (container) (typed FeaturePython)
  n = 0.067125
FEATURE [App::DocumentObjectGroupPython] C_element026  label="C_element : 0.545"  # scripted group (container) (typed FeaturePython)
  n = 0.545403
FEATURE [App::DocumentObjectGroupPython] O_element027  label="O_element : 0.387"  # scripted group (container) (typed FeaturePython)
  n = 0.387472
FEATURE [App::DocumentObjectGroupPython] G4_CELLULOSE_BUTYRATE  # scripted group (container) (typed FeaturePython)
  Dunit = g/cm3
  Dvalue = 1.2
  Group = -> [H_element022,C_element026,O_element027]
  conduct = 2
  density = 1
  expand = 3
  formula = G4_CELLULOSE_BUTYRATE
  name = G4_CELLULOSE_BUTYRATE
  specific = 4
FEATURE [App::DocumentObjectGroupPython] H_element023  label="H_element : 0.029"  # scripted group (container) (typed FeaturePython)
  n = 0.029216
FEATURE [App::DocumentObjectGroupPython] C_element027  label="C_element : 0.271"  # scripted group (container) (typed FeaturePython)
  n = 0.271296
FEATURE [App::DocumentObjectGroupPython] N_element013  label="N_element : 0.121"  # scripted group (container) (typed FeaturePython)
  n = 0.121276
FEATURE [App::DocumentObjectGroupPython] O_element028  label="O_element : 0.578"  # scripted group (container) (typed FeaturePython)
  n = 0.578212
FEATURE [App::DocumentObjectGroupPython] G4_CELLULOSE_NITRATE  # scripted group (container) (typed FeaturePython)
  Dunit = g/cm3
  Dvalue = 1.49
  Group = -> [H_element023,C_element027,N_element013,O_element028]
  conduct = 2
  density = 1
  expand = 3
  formula = G4_CELLULOSE_NITRATE
  name = G4_CELLULOSE_NITRATE
  specific = 4
FEATURE [App::DocumentObjectGroupPython] H_element024  label="H_element : 0.108"  # scripted group (container) (typed FeaturePython)
  n = 0.107596
FEATURE [App::DocumentObjectGroupPython] N_element014  label="N_element : 0.001"  # scripted group (container) (typed FeaturePython)
  n = 0.0008
FEATURE [App::DocumentObjectGroupPython] O_element029  label="O_element : 0.875"  # scripted group (container) (typed FeaturePython)
  n = 0.874976
FEATURE [App::DocumentObjectGroupPython] S_element008  label="S_element : 0.015"  # scripted group (container) (typed FeaturePython)
  n = 0.014627
FEATURE [App::DocumentObjectGroupPython] Ce_element001  label="Ce_element : 0.002"  # scripted group (container) (typed FeaturePython)
  n = 0.002001
FEATURE [App::DocumentObjectGroupPython] G4_CERIC_SULFATE  # scripted group (container) (typed FeaturePython)
  Dunit = g/cm3
  Dvalue = 1.03
  Group = -> [H_element024,N_element014,O_element029,S_element008,Ce_element001]
  conduct = 2
  density = 1
  expand = 3
  formula = G4_CERIC_SULFATE
  name = G4_CERIC_SULFATE
  specific = 4
FEATURE [App::DocumentObjectGroupPython] Cs_element001  label="Cs_element : 1"  # scripted group (container) (typed FeaturePython)
  n = 1
  ref = Cs_element
FEATURE [App::DocumentObjectGroupPython] F_element006  label="F_element : 1"  # scripted group (container) (typed FeaturePython)
  n = 1
  ref = F_element
FEATURE [App::DocumentObjectGroupPython] G4_CESIUM_FLUORIDE  # scripted group (container) (typed FeaturePython)
  Dunit = g/cm3
  Dvalue = 4.115
  Group = -> [Cs_element001,F_element006]
  conduct = 2
  density = 1
  expand = 3
  formula = G4_CESIUM_FLUORIDE
  name = G4_CESIUM_FLUORIDE
  specific = 4
FEATURE [App::DocumentObjectGroupPython] Cs_element002  label="Cs_element : 002"  # scripted group (container) (typed FeaturePython)
  n = 1
  ref = Cs_element
FEATURE [App::DocumentObjectGroupPython] I_element001  label="I_element : 1"  # scripted group (container) (typed FeaturePython)
  n = 1
  ref = I_element
FEATURE [App::DocumentObjectGroupPython] G4_CESIUM_IODIDE  # scripted group (container) (typed FeaturePython)
  Dunit = g/cm3
  Dvalue = 4.51
  Group = -> [Cs_element002,I_element001]
  conduct = 2
  density = 1
  expand = 3
  formula = G4_CESIUM_IODIDE
  name = G4_CESIUM_IODIDE
  specific = 4
FEATURE [App::DocumentObjectGroupPython] C_element028  label="C_element : 013"  # scripted group (container) (typed FeaturePython)
  n = 6
  ref = C_element
FEATURE [App::DocumentObjectGroupPython] H_element025  label="H_element : 013"  # scripted group (container) (typed FeaturePython)
  n = 5
  ref = H_element
FEATURE [App::DocumentObjectGroupPython] Cl_element005  label="Cl_element : 1"  # scripted group (container) (typed FeaturePython)
  n = 1
  ref = Cl_element
FEATURE [App::DocumentObjectGroupPython] G4_CHLOROBENZENE  # scripted group (container) (typed FeaturePython)
  Dunit = g/cm3
  Dvalue = 1.1058
  Group = -> [C_element028,H_element025,Cl_element005]
  conduct = 2
  density = 1
  expand = 3
  formula = G4_CHLOROBENZENE
  name = G4_CHLOROBENZENE
  specific = 4
FEATURE [App::DocumentObjectGroupPython] C_element029  label="C_element : 014"  # scripted group (container) (typed FeaturePython)
  n = 1
  ref = C_element
FEATURE [App::DocumentObjectGroupPython] H_element026  label="H_element : 1"  # scripted group (container) (typed FeaturePython)
  n = 1
  ref = H_element
FEATURE [App::DocumentObjectGroupPython] Cl_element006  label="Cl_element : 3"  # scripted group (container) (typed FeaturePython)
  n = 3
  ref = Cl_element
FEATURE [App::DocumentObjectGroupPython] G4_CHLOROFORM  # scripted group (container) (typed FeaturePython)
  Dunit = g/cm3
  Dvalue = 1.4832
  Group = -> [C_element029,H_element026,Cl_element006]
  conduct = 2
  density = 1
  expand = 3
  formula = G4_CHLOROFORM
  name = G4_CHLOROFORM
  specific = 4
FEATURE [App::DocumentObjectGroupPython] H_element027  label="H_element : 0.010"  # scripted group (container) (typed FeaturePython)
  n = 0.01
FEATURE [App::DocumentObjectGroupPython] C_element030  label="C_element : 0.001"  # scripted group (container) (typed FeaturePython)
  n = 0.001
FEATURE [App::DocumentObjectGroupPython] O_element030  label="O_element : 0.529"  # scripted group (container) (typed FeaturePython)
  n = 0.529107
FEATURE [App::DocumentObjectGroupPython] Na_element005  label="Na_element : 0.016"  # scripted group (container) (typed FeaturePython)
  n = 0.016
FEATURE [App::DocumentObjectGroupPython] Mg_element003  label="Mg_element : 0.004"  # scripted group (container) (typed FeaturePython)
  n = 0.002
FEATURE [App::DocumentObjectGroupPython] Al_element002  label="Al_element : 0.034"  # scripted group (container) (typed FeaturePython)
  n = 0.033872
FEATURE [App::DocumentObjectGroupPython] Si_element002  label="Si_element : 0.337"  # scripted group (container) (typed FeaturePython)
  n = 0.337021
FEATURE [App::DocumentObjectGroupPython] K_element003  label="K_element : 0.013"  # scripted group (container) (typed FeaturePython)
  n = 0.013
FEATURE [App::DocumentObjectGroupPython] Ca_element010  label="Ca_element : 0.044"  # scripted group (container) (typed FeaturePython)
  n = 0.044
FEATURE [App::DocumentObjectGroupPython] Fe_element002  label="Fe_element : 0.014"  # scripted group (container) (typed FeaturePython)
  n = 0.014
FEATURE [App::DocumentObjectGroupPython] G4_CONCRETE  # scripted group (container) (typed FeaturePython)
  Dunit = g/cm3
  Dvalue = 2.3
  Group = -> [H_element027,C_element030,O_element030,Na_element005,Mg_element003,Al_element002,Si_element002,K_element003,Ca_element010,Fe_element002]
  conduct = 2
  density = 1
  expand = 3
  formula = G4_CONCRETE
  name = G4_CONCRETE
  specific = 4
FEATURE [App::DocumentObjectGroupPython] C_element031  label="C_element : 015"  # scripted group (container) (typed FeaturePython)
  n = 6
  ref = C_element
FEATURE [App::DocumentObjectGroupPython] H_element028  label="H_element : 12"  # scripted group (container) (typed FeaturePython)
  n = 12
  ref = H_element
FEATURE [App::DocumentObjectGroupPython] G4_CYCLOHEXANE  # scripted group (container) (typed FeaturePython)
  Dunit = g/cm3
  Dvalue = 0.779
  Group = -> [C_element031,H_element028]
  conduct = 2
  density = 1
  expand = 3
  formula = G4_CYCLOHEXANE
  name = G4_CYCLOHEXANE
  specific = 4
FEATURE [App::DocumentObjectGroupPython] C_element032  label="C_element : 016"  # scripted group (container) (typed FeaturePython)
  n = 6
  ref = C_element
FEATURE [App::DocumentObjectGroupPython] H_element029  label="H_element : 4"  # scripted group (container) (typed FeaturePython)
  n = 4
  ref = H_element
FEATURE [App::DocumentObjectGroupPython] Cl_element007  label="Cl_element : 2"  # scripted group (container) (typed FeaturePython)
  n = 2
  ref = Cl_element
FEATURE [App::DocumentObjectGroupPython] G4_1_2_DICHLOROBENZENE  label="G4_1.2-DICHLOROBENZENE"  # scripted group (container) (typed FeaturePython)
  Dunit = g/cm3
  Dvalue = 1.3048
  Group = -> [C_element032,H_element029,Cl_element007]
  conduct = 2
  density = 1
  expand = 3
  formula = G4_1.2-DICHLOROBENZENE
  name = G4_1.2-DICHLOROBENZENE
  specific = 4
FEATURE [App::DocumentObjectGroupPython] C_element033  label="C_element : 017"  # scripted group (container) (typed FeaturePython)
  n = 4
  ref = C_element
FEATURE [App::DocumentObjectGroupPython] H_element030  label="H_element : 8"  # scripted group (container) (typed FeaturePython)
  n = 8
  ref = H_element
FEATURE [App::DocumentObjectGroupPython] O_element031  label="O_element : 014"  # scripted group (container) (typed FeaturePython)
  n = 1
  ref = O_element
FEATURE [App::DocumentObjectGroupPython] Cl_element008  label="Cl_element : 005"  # scripted group (container) (typed FeaturePython)
  n = 2
  ref = Cl_element
FEATURE [App::DocumentObjectGroupPython] G4_DICHLORODIETHYL_ETHER  # scripted group (container) (typed FeaturePython)
  Dunit = g/cm3
  Dvalue = 1.2199
  Group = -> [C_element033,H_element030,O_element031,Cl_element008]
  conduct = 2
  density = 1
  expand = 3
  formula = G4_DICHLORODIETHYL_ETHER
  name = G4_DICHLORODIETHYL_ETHER
  specific = 4
FEATURE [App::DocumentObjectGroupPython] C_element034  label="C_element : 018"  # scripted group (container) (typed FeaturePython)
  n = 2
  ref = C_element
FEATURE [App::DocumentObjectGroupPython] H_element031  label="H_element : 014"  # scripted group (container) (typed FeaturePython)
  n = 4
  ref = H_element
FEATURE [App::DocumentObjectGroupPython] Cl_element009  label="Cl_element : 006"  # scripted group (container) (typed FeaturePython)
  n = 2
  ref = Cl_element
FEATURE [App::DocumentObjectGroupPython] G4_1_2_DICHLOROETHANE  label="G4_1.2-DICHLOROETHANE"  # scripted group (container) (typed FeaturePython)
  Dunit = g/cm3
  Dvalue = 1.2351
  Group = -> [C_element034,H_element031,Cl_element009]
  conduct = 2
  density = 1
  expand = 3
  formula = G4_1.2-DICHLOROETHANE
  name = G4_1.2-DICHLOROETHANE
  specific = 4
FEATURE [App::DocumentObjectGroupPython] C_element035  label="C_element : 019"  # scripted group (container) (typed FeaturePython)
  n = 4
  ref = C_element
FEATURE [App::DocumentObjectGroupPython] H_element032  label="H_element : 015"  # scripted group (container) (typed FeaturePython)
  n = 10
  ref = H_element
FEATURE [App::DocumentObjectGroupPython] O_element032  label="O_element : 015"  # scripted group (container) (typed FeaturePython)
  n = 1
  ref = O_element
FEATURE [App::DocumentObjectGroupPython] G4_DIETHYL_ETHER  # scripted group (container) (typed FeaturePython)
  Dunit = g/cm3
  Dvalue = 0.71378
  Group = -> [C_element035,H_element032,O_element032]
  conduct = 2
  density = 1
  expand = 3
  formula = G4_DIETHYL_ETHER
  name = G4_DIETHYL_ETHER
  specific = 4
FEATURE [App::DocumentObjectGroupPython] C_element036  label="C_element : 020"  # scripted group (container) (typed FeaturePython)
  n = 3
  ref = C_element
FEATURE [App::DocumentObjectGroupPython] H_element033  label="H_element : 016"  # scripted group (container) (typed FeaturePython)
  n = 7
  ref = H_element
FEATURE [App::DocumentObjectGroupPython] N_element015  label="N_element : 008"  # scripted group (container) (typed FeaturePython)
  n = 1
  ref = N_element
FEATURE [App::DocumentObjectGroupPython] O_element033  label="O_element : 016"  # scripted group (container) (typed FeaturePython)
  n = 1
  ref = O_element
FEATURE [App::DocumentObjectGroupPython] G4_N_N_DIMETHYL_FORMAMIDE  label="G4_N.N-DIMETHYL_FORMAMIDE"  # scripted group (container) (typed FeaturePython)
  Dunit = g/cm3
  Dvalue = 0.9487
  Group = -> [C_element036,H_element033,N_element015,O_element033]
  conduct = 2
  density = 1
  expand = 3
  formula = G4_N.N-DIMETHYL_FORMAMIDE
  name = G4_N.N-DIMETHYL_FORMAMIDE
  specific = 4
FEATURE [App::DocumentObjectGroupPython] C_element037  label="C_element : 021"  # scripted group (container) (typed FeaturePython)
  n = 2
  ref = C_element
FEATURE [App::DocumentObjectGroupPython] H_element034  label="H_element : 017"  # scripted group (container) (typed FeaturePython)
  n = 6
  ref = H_element
FEATURE [App::DocumentObjectGroupPython] O_element034  label="O_element : 017"  # scripted group (container) (typed FeaturePython)
  n = 1
  ref = O_element
FEATURE [App::DocumentObjectGroupPython] S_element009  label="S_element : 003"  # scripted group (container) (typed FeaturePython)
  n = 1
  ref = S_element
FEATURE [App::DocumentObjectGroupPython] G4_DIMETHYL_SULFOXIDE  # scripted group (container) (typed FeaturePython)
  Dunit = g/cm3
  Dvalue = 1.1014
  Group = -> [C_element037,H_element034,O_element034,S_element009]
  conduct = 2
  density = 1
  expand = 3
  formula = G4_DIMETHYL_SULFOXIDE
  name = G4_DIMETHYL_SULFOXIDE
  specific = 4
FEATURE [App::DocumentObjectGroupPython] C_element038  label="C_element : 022"  # scripted group (container) (typed FeaturePython)
  n = 2
  ref = C_element
FEATURE [App::DocumentObjectGroupPython] H_element035  label="H_element : 018"  # scripted group (container) (typed FeaturePython)
  n = 6
  ref = H_element
FEATURE [App::DocumentObjectGroupPython] G4_ETHANE  # scripted group (container) (typed FeaturePython)
  Dunit = g/cm3
  Dvalue = 0.00125324
  Group = -> [C_element038,H_element035]
  conduct = 2
  density = 1
  expand = 3
  formula = G4_ETHANE
  name = G4_ETHANE
  specific = 4
FEATURE [App::DocumentObjectGroupPython] C_element039  label="C_element : 023"  # scripted group (container) (typed FeaturePython)
  n = 2
  ref = C_element
FEATURE [App::DocumentObjectGroupPython] H_element036  label="H_element : 019"  # scripted group (container) (typed FeaturePython)
  n = 6
  ref = H_element
FEATURE [App::DocumentObjectGroupPython] O_element035  label="O_element : 018"  # scripted group (container) (typed FeaturePython)
  n = 1
  ref = O_element
FEATURE [App::DocumentObjectGroupPython] G4_ETHYL_ALCOHOL  # scripted group (container) (typed FeaturePython)
  Dunit = g/cm3
  Dvalue = 0.7893
  Group = -> [C_element039,H_element036,O_element035]
  conduct = 2
  density = 1
  expand = 3
  formula = G4_ETHYL_ALCOHOL
  name = G4_ETHYL_ALCOHOL
  specific = 4
FEATURE [App::DocumentObjectGroupPython] H_element037  label="H_element : 0.090"  # scripted group (container) (typed FeaturePython)
  n = 0.090027
FEATURE [App::DocumentObjectGroupPython] C_element040  label="C_element : 0.585"  # scripted group (container) (typed FeaturePython)
  n = 0.585182
FEATURE [App::DocumentObjectGroupPython] O_element036  label="O_element : 0.325"  # scripted group (container) (typed FeaturePython)
  n = 0.324791
FEATURE [App::DocumentObjectGroupPython] G4_ETHYL_CELLULOSE  # scripted group (container) (typed FeaturePython)
  Dunit = g/cm3
  Dvalue = 1.13
  Group = -> [H_element037,C_element040,O_element036]
  conduct = 2
  density = 1
  expand = 3
  formula = G4_ETHYL_CELLULOSE
  name = G4_ETHYL_CELLULOSE
  specific = 4
FEATURE [App::DocumentObjectGroupPython] C_element041  label="C_element : 024"  # scripted group (container) (typed FeaturePython)
  n = 2
  ref = C_element
FEATURE [App::DocumentObjectGroupPython] H_element038  label="H_element : 020"  # scripted group (container) (typed FeaturePython)
  n = 4
  ref = H_element
FEATURE [App::DocumentObjectGroupPython] G4_ETHYLENE  # scripted group (container) (typed FeaturePython)
  Dunit = g/cm3
  Dvalue = 0.00117497
  Group = -> [C_element041,H_element038]
  conduct = 2
  density = 1
  expand = 3
  formula = G4_ETHYLENE
  name = G4_ETHYLENE
  specific = 4
FEATURE [App::DocumentObjectGroupPython] H_element039  label="H_element : 0.096"  # scripted group (container) (typed FeaturePython)
  n = 0.096
FEATURE [App::DocumentObjectGroupPython] C_element042  label="C_element : 0.195"  # scripted group (container) (typed FeaturePython)
  n = 0.195
FEATURE [App::DocumentObjectGroupPython] N_element016  label="N_element : 0.057"  # scripted group (container) (typed FeaturePython)
  n = 0.057
FEATURE [App::DocumentObjectGroupPython] O_element037  label="O_element : 0.646"  # scripted group (container) (typed FeaturePython)
  n = 0.646
FEATURE [App::DocumentObjectGroupPython] Na_element006  label="Na_element : 0.017"  # scripted group (container) (typed FeaturePython)
  n = 0.001
FEATURE [App::DocumentObjectGroupPython] P_element005  label="P_element : 0.104"  # scripted group (container) (typed FeaturePython)
  n = 0.001
FEATURE [App::DocumentObjectGroupPython] S_element010  label="S_element : 0.016"  # scripted group (container) (typed FeaturePython)
  n = 0.003
FEATURE [App::DocumentObjectGroupPython] Cl_element010  label="Cl_element : 0.005"  # scripted group (container) (typed FeaturePython)
  n = 0.001
FEATURE [App::DocumentObjectGroupPython] G4_EYE_LENS_ICRP  # scripted group (container) (typed FeaturePython)
  Dunit = g/cm3
  Dvalue = 1.07
  Group = -> [H_element039,C_element042,N_element016,O_element037,Na_element006,P_element005,S_element010,Cl_element010]
  conduct = 2
  density = 1
  expand = 3
  formula = G4_EYE_LENS_ICRP
  name = G4_EYE_LENS_ICRP
  specific = 4
FEATURE [App::DocumentObjectGroupPython] Fe_element003  label="Fe_element : 2"  # scripted group (container) (typed FeaturePython)
  n = 2
  ref = Fe_element
FEATURE [App::DocumentObjectGroupPython] O_element038  label="O_element : 019"  # scripted group (container) (typed FeaturePython)
  n = 3
  ref = O_element
FEATURE [App::DocumentObjectGroupPython] G4_FERRIC_OXIDE  # scripted group (container) (typed FeaturePython)
  Dunit = g/cm3
  Dvalue = 5.2
  Group = -> [Fe_element003,O_element038]
  conduct = 2
  density = 1
  expand = 3
  formula = G4_FERRIC_OXIDE
  name = G4_FERRIC_OXIDE
  specific = 4
FEATURE [App::DocumentObjectGroupPython] Fe_element004  label="Fe_element : 1"  # scripted group (container) (typed FeaturePython)
  n = 1
  ref = Fe_element
FEATURE [App::DocumentObjectGroupPython] B_element003  label="B_element : 1"  # scripted group (container) (typed FeaturePython)
  n = 1
  ref = B_element
FEATURE [App::DocumentObjectGroupPython] G4_FERROBORIDE  # scripted group (container) (typed FeaturePython)
  Dunit = g/cm3
  Dvalue = 7.15
  Group = -> [Fe_element004,B_element003]
  conduct = 2
  density = 1
  expand = 3
  formula = G4_FERROBORIDE
  name = G4_FERROBORIDE
  specific = 4
FEATURE [App::DocumentObjectGroupPython] Fe_element005  label="Fe_element : 003"  # scripted group (container) (typed FeaturePython)
  n = 1
  ref = Fe_element
FEATURE [App::DocumentObjectGroupPython] O_element039  label="O_element : 020"  # scripted group (container) (typed FeaturePython)
  n = 1
  ref = O_element
FEATURE [App::DocumentObjectGroupPython] G4_FERROUS_OXIDE  # scripted group (container) (typed FeaturePython)
  Dunit = g/cm3
  Dvalue = 5.7
  Group = -> [Fe_element005,O_element039]
  conduct = 2
  density = 1
  expand = 3
  formula = G4_FERROUS_OXIDE
  name = G4_FERROUS_OXIDE
  specific = 4
FEATURE [App::DocumentObjectGroupPython] H_element040  label="H_element : 0.115"  # scripted group (container) (typed FeaturePython)
  n = 0.108259
FEATURE [App::DocumentObjectGroupPython] N_element017  label="N_element : 0.000"  # scripted group (container) (typed FeaturePython)
  n = 2.7e-05
FEATURE [App::DocumentObjectGroupPython] O_element040  label="O_element : 0.879"  # scripted group (container) (typed FeaturePython)
  n = 0.878636
FEATURE [App::DocumentObjectGroupPython] Na_element007  label="Na_element : 0.000"  # scripted group (container) (typed FeaturePython)
  n = 2.2e-05
FEATURE [App::DocumentObjectGroupPython] S_element011  label="S_element : 0.013"  # scripted group (container) (typed FeaturePython)
  n = 0.012968
FEATURE [App::DocumentObjectGroupPython] Cl_element011  label="Cl_element : 0.000"  # scripted group (container) (typed FeaturePython)
  n = 3.4e-05
FEATURE [App::DocumentObjectGroupPython] Fe_element006  label="Fe_element : 0.000"  # scripted group (container) (typed FeaturePython)
  n = 5.4e-05
FEATURE [App::DocumentObjectGroupPython] G4_FERROUS_SULFATE  # scripted group (container) (typed FeaturePython)
  Dunit = g/cm3
  Dvalue = 1.024
  Group = -> [H_element040,N_element017,O_element040,Na_element007,S_element011,Cl_element011,Fe_element006]
  conduct = 2
  density = 1
  expand = 3
  formula = G4_FERROUS_SULFATE
  name = G4_FERROUS_SULFATE
  specific = 4
FEATURE [App::DocumentObjectGroupPython] C_element043  label="C_element : 0.099"  # scripted group (container) (typed FeaturePython)
  n = 0.099335
FEATURE [App::DocumentObjectGroupPython] F_element007  label="F_element : 0.314"  # scripted group (container) (typed FeaturePython)
  n = 0.314247
FEATURE [App::DocumentObjectGroupPython] Cl_element012  label="Cl_element : 0.586"  # scripted group (container) (typed FeaturePython)
  n = 0.586418
FEATURE [App::DocumentObjectGroupPython] G4_FREON_12  label="G4_FREON-12"  # scripted group (container) (typed FeaturePython)
  Dunit = g/cm3
  Dvalue = 1.12
  Group = -> [C_element043,F_element007,Cl_element012]
  conduct = 2
  density = 1
  expand = 3
  formula = G4_FREON-12
  name = G4_FREON-12
  specific = 4
FEATURE [App::DocumentObjectGroupPython] C_element044  label="C_element : 0.057"  # scripted group (container) (typed FeaturePython)
  n = 0.057245
FEATURE [App::DocumentObjectGroupPython] F_element008  label="F_element : 0.181"  # scripted group (container) (typed FeaturePython)
  n = 0.181096
FEATURE [App::DocumentObjectGroupPython] Br_element001  label="Br_element : 0.762"  # scripted group (container) (typed FeaturePython)
  n = 0.761659
FEATURE [App::DocumentObjectGroupPython] G4_FREON_12B2  label="G4_FREON-12B2"  # scripted group (container) (typed FeaturePython)
  Dunit = g/cm3
  Dvalue = 1.8
  Group = -> [C_element044,F_element008,Br_element001]
  conduct = 2
  density = 1
  expand = 3
  formula = G4_FREON-12B2
  name = G4_FREON-12B2
  specific = 4
FEATURE [App::DocumentObjectGroupPython] C_element045  label="C_element : 0.115"  # scripted group (container) (typed FeaturePython)
  n = 0.114983
FEATURE [App::DocumentObjectGroupPython] F_element009  label="F_element : 0.546"  # scripted group (container) (typed FeaturePython)
  n = 0.545621
FEATURE [App::DocumentObjectGroupPython] Cl_element013  label="Cl_element : 0.339"  # scripted group (container) (typed FeaturePython)
  n = 0.339396
FEATURE [App::DocumentObjectGroupPython] G4_FREON_13  label="G4_FREON-13"  # scripted group (container) (typed FeaturePython)
  Dunit = g/cm3
  Dvalue = 0.95
  Group = -> [C_element045,F_element009,Cl_element013]
  conduct = 2
  density = 1
  expand = 3
  formula = G4_FREON-13
  name = G4_FREON-13
  specific = 4
FEATURE [App::DocumentObjectGroupPython] C_element046  label="C_element : 025"  # scripted group (container) (typed FeaturePython)
  n = 1
  ref = C_element
FEATURE [App::DocumentObjectGroupPython] F_element010  label="F_element : 3"  # scripted group (container) (typed FeaturePython)
  n = 3
  ref = F_element
FEATURE [App::DocumentObjectGroupPython] Br_element002  label="Br_element : 1"  # scripted group (container) (typed FeaturePython)
  n = 1
  ref = Br_element
FEATURE [App::DocumentObjectGroupPython] G4_FREON_13B1  label="G4_FREON-13B1"  # scripted group (container) (typed FeaturePython)
  Dunit = g/cm3
  Dvalue = 1.5
  Group = -> [C_element046,F_element010,Br_element002]
  conduct = 2
  density = 1
  expand = 3
  formula = G4_FREON-13B1
  name = G4_FREON-13B1
  specific = 4
FEATURE [App::DocumentObjectGroupPython] C_element047  label="C_element : 0.061"  # scripted group (container) (typed FeaturePython)
  n = 0.061309
FEATURE [App::DocumentObjectGroupPython] F_element011  label="F_element : 0.291"  # scripted group (container) (typed FeaturePython)
  n = 0.290924
FEATURE [App::DocumentObjectGroupPython] I_element002  label="I_element : 0.648"  # scripted group (container) (typed FeaturePython)
  n = 0.647767
FEATURE [App::DocumentObjectGroupPython] G4_FREON_13I1  label="G4_FREON-13I1"  # scripted group (container) (typed FeaturePython)
  Dunit = g/cm3
  Dvalue = 1.8
  Group = -> [C_element047,F_element011,I_element002]
  conduct = 2
  density = 1
  expand = 3
  formula = G4_FREON-13I1
  name = G4_FREON-13I1
  specific = 4
FEATURE [App::DocumentObjectGroupPython] Gd_element001  label="Gd_element : 2"  # scripted group (container) (typed FeaturePython)
  n = 2
  ref = Gd_element
FEATURE [App::DocumentObjectGroupPython] O_element041  label="O_element : 021"  # scripted group (container) (typed FeaturePython)
  n = 2
  ref = O_element
FEATURE [App::DocumentObjectGroupPython] S_element012  label="S_element : 004"  # scripted group (container) (typed FeaturePython)
  n = 1
  ref = S_element
FEATURE [App::DocumentObjectGroupPython] G4_GADOLINIUM_OXYSULFIDE  # scripted group (container) (typed FeaturePython)
  Dunit = g/cm3
  Dvalue = 7.44
  Group = -> [Gd_element001,O_element041,S_element012]
  conduct = 2
  density = 1
  expand = 3
  formula = G4_GADOLINIUM_OXYSULFIDE
  name = G4_GADOLINIUM_OXYSULFIDE
  specific = 4
FEATURE [App::DocumentObjectGroupPython] Ga_element001  label="Ga_element : 1"  # scripted group (container) (typed FeaturePython)
  n = 1
  ref = Ga_element
FEATURE [App::DocumentObjectGroupPython] As_element001  label="As_element : 1"  # scripted group (container) (typed FeaturePython)
  n = 1
  ref = As_element
FEATURE [App::DocumentObjectGroupPython] G4_GALLIUM_ARSENIDE  # scripted group (container) (typed FeaturePython)
  Dunit = g/cm3
  Dvalue = 5.31
  Group = -> [Ga_element001,As_element001]
  conduct = 2
  density = 1
  expand = 3
  formula = G4_GALLIUM_ARSENIDE
  name = G4_GALLIUM_ARSENIDE
  specific = 4
FEATURE [App::DocumentObjectGroupPython] H_element041  label="H_element : 0.081"  # scripted group (container) (typed FeaturePython)
  n = 0.08118
FEATURE [App::DocumentObjectGroupPython] C_element048  label="C_element : 0.416"  # scripted group (container) (typed FeaturePython)
  n = 0.41606
FEATURE [App::DocumentObjectGroupPython] N_element018  label="N_element : 0.111"  # scripted group (container) (typed FeaturePython)
  n = 0.11124
FEATURE [App::DocumentObjectGroupPython] O_element042  label="O_element : 0.381"  # scripted group (container) (typed FeaturePython)
  n = 0.38064
FEATURE [App::DocumentObjectGroupPython] S_element013  label="S_element : 0.011"  # scripted group (container) (typed FeaturePython)
  n = 0.01088
FEATURE [App::DocumentObjectGroupPython] G4_GEL_PHOTO_EMULSION  # scripted group (container) (typed FeaturePython)
  Dunit = g/cm3
  Dvalue = 1.2914
  Group = -> [H_element041,C_element048,N_element018,O_element042,S_element013]
  conduct = 2
  density = 1
  expand = 3
  formula = G4_GEL_PHOTO_EMULSION
  name = G4_GEL_PHOTO_EMULSION
  specific = 4
FEATURE [App::DocumentObjectGroupPython] B_element004  label="B_element : 0.040"  # scripted group (container) (typed FeaturePython)
  n = 0.0400639
FEATURE [App::DocumentObjectGroupPython] O_element043  label="O_element : 0.540"  # scripted group (container) (typed FeaturePython)
  n = 0.539561
FEATURE [App::DocumentObjectGroupPython] Na_element008  label="Na_element : 0.028"  # scripted group (container) (typed FeaturePython)
  n = 0.0281909
FEATURE [App::DocumentObjectGroupPython] Al_element003  label="Al_element : 0.012"  # scripted group (container) (typed FeaturePython)
  n = 0.011644
FEATURE [App::DocumentObjectGroupPython] Si_element003  label="Si_element : 0.377"  # scripted group (container) (typed FeaturePython)
  n = 0.377219
FEATURE [App::DocumentObjectGroupPython] K_element004  label="K_element : 0.014"  # scripted group (container) (typed FeaturePython)
  n = 0.00332099
FEATURE [App::DocumentObjectGroupPython] G4_Pyrex_Glass  # scripted group (container) (typed FeaturePython)
  Dunit = g/cm3
  Dvalue = 2.23
  Group = -> [B_element004,O_element043,Na_element008,Al_element003,Si_element003,K_element004]
  conduct = 2
  density = 1
  expand = 3
  formula = G4_Pyrex_Glass
  name = G4_Pyrex_Glass
  specific = 4
FEATURE [App::DocumentObjectGroupPython] O_element044  label="O_element : 0.156"  # scripted group (container) (typed FeaturePython)
  n = 0.156453
FEATURE [App::DocumentObjectGroupPython] Si_element004  label="Si_element : 0.081"  # scripted group (container) (typed FeaturePython)
  n = 0.080866
FEATURE [App::DocumentObjectGroupPython] Ti_element001  label="Ti_element : 0.008"  # scripted group (container) (typed FeaturePython)
  n = 0.008092
FEATURE [App::DocumentObjectGroupPython] As_element002  label="As_element : 0.003"  # scripted group (container) (typed FeaturePython)
  n = 0.002651
FEATURE [App::DocumentObjectGroupPython] Pb_element001  label="Pb_element : 0.752"  # scripted group (container) (typed FeaturePython)
  n = 0.751938
FEATURE [App::DocumentObjectGroupPython] G4_GLASS_LEAD  # scripted group (container) (typed FeaturePython)
  Dunit = g/cm3
  Dvalue = 6.22
  Group = -> [O_element044,Si_element004,Ti_element001,As_element002,Pb_element001]
  conduct = 2
  density = 1
  expand = 3
  formula = G4_GLASS_LEAD
  name = G4_GLASS_LEAD
  specific = 4
FEATURE [App::DocumentObjectGroupPython] O_element045  label="O_element : 0.460"  # scripted group (container) (typed FeaturePython)
  n = 0.4598
FEATURE [App::DocumentObjectGroupPython] Na_element009  label="Na_element : 0.096"  # scripted group (container) (typed FeaturePython)
  n = 0.0964411
FEATURE [App::DocumentObjectGroupPython] Si_element005  label="Si_element : 0.378"  # scripted group (container) (typed FeaturePython)
  n = 0.336553
FEATURE [App::DocumentObjectGroupPython] Ca_element011  label="Ca_element : 0.107"  # scripted group (container) (typed FeaturePython)
  n = 0.107205
FEATURE [App::DocumentObjectGroupPython] G4_GLASS_PLATE  # scripted group (container) (typed FeaturePython)
  Dunit = g/cm3
  Dvalue = 2.4
  Group = -> [O_element045,Na_element009,Si_element005,Ca_element011]
  conduct = 2
  density = 1
  expand = 3
  formula = G4_GLASS_PLATE
  name = G4_GLASS_PLATE
  specific = 4
FEATURE [App::DocumentObjectGroupPython] C_element049  label="C_element : 026"  # scripted group (container) (typed FeaturePython)
  n = 5
  ref = C_element
FEATURE [App::DocumentObjectGroupPython] H_element042  label="H_element : 021"  # scripted group (container) (typed FeaturePython)
  n = 10
  ref = H_element
FEATURE [App::DocumentObjectGroupPython] N_element019  label="N_element : 2"  # scripted group (container) (typed FeaturePython)
  n = 2
  ref = N_element
FEATURE [App::DocumentObjectGroupPython] O_element046  label="O_element : 022"  # scripted group (container) (typed FeaturePython)
  n = 3
  ref = O_element
FEATURE [App::DocumentObjectGroupPython] G4_GLUTAMINE  # scripted group (container) (typed FeaturePython)
  Dunit = g/cm3
  Dvalue = 1.46
  Group = -> [C_element049,H_element042,N_element019,O_element046]
  conduct = 2
  density = 1
  expand = 3
  formula = G4_GLUTAMINE
  name = G4_GLUTAMINE
  specific = 4
FEATURE [App::DocumentObjectGroupPython] C_element050  label="C_element : 027"  # scripted group (container) (typed FeaturePython)
  n = 3
  ref = C_element
FEATURE [App::DocumentObjectGroupPython] H_element043  label="H_element : 022"  # scripted group (container) (typed FeaturePython)
  n = 8
  ref = H_element
FEATURE [App::DocumentObjectGroupPython] O_element047  label="O_element : 023"  # scripted group (container) (typed FeaturePython)
  n = 3
  ref = O_element
FEATURE [App::DocumentObjectGroupPython] G4_GLYCEROL  # scripted group (container) (typed FeaturePython)
  Dunit = g/cm3
  Dvalue = 1.2613
  Group = -> [C_element050,H_element043,O_element047]
  conduct = 2
  density = 1
  expand = 3
  formula = G4_GLYCEROL
  name = G4_GLYCEROL
  specific = 4
FEATURE [App::DocumentObjectGroupPython] C_element051  label="C_element : 028"  # scripted group (container) (typed FeaturePython)
  n = 5
  ref = C_element
FEATURE [App::DocumentObjectGroupPython] H_element044  label="H_element : 023"  # scripted group (container) (typed FeaturePython)
  n = 5
  ref = H_element
FEATURE [App::DocumentObjectGroupPython] N_element020  label="N_element : 009"  # scripted group (container) (typed FeaturePython)
  n = 5
  ref = N_element
FEATURE [App::DocumentObjectGroupPython] O_element048  label="O_element : 024"  # scripted group (container) (typed FeaturePython)
  n = 1
  ref = O_element
FEATURE [App::DocumentObjectGroupPython] G4_GUANINE  # scripted group (container) (typed FeaturePython)
  Dunit = g/cm3
  Dvalue = 2.2
  Group = -> [C_element051,H_element044,N_element020,O_element048]
  conduct = 2
  density = 1
  expand = 3
  formula = G4_GUANINE
  name = G4_GUANINE
  specific = 4
FEATURE [App::DocumentObjectGroupPython] Ca_element012  label="Ca_element : 006"  # scripted group (container) (typed FeaturePython)
  n = 1
  ref = Ca_element
FEATURE [App::DocumentObjectGroupPython] S_element014  label="S_element : 005"  # scripted group (container) (typed FeaturePython)
  n = 1
  ref = S_element
FEATURE [App::DocumentObjectGroupPython] O_element049  label="O_element : 6"  # scripted group (container) (typed FeaturePython)
  n = 6
  ref = O_element
FEATURE [App::DocumentObjectGroupPython] H_element045  label="H_element : 024"  # scripted group (container) (typed FeaturePython)
  n = 4
  ref = H_element
FEATURE [App::DocumentObjectGroupPython] G4_GYPSUM  # scripted group (container) (typed FeaturePython)
  Dunit = g/cm3
  Dvalue = 2.32
  Group = -> [Ca_element012,S_element014,O_element049,H_element045]
  conduct = 2
  density = 1
  expand = 3
  formula = G4_GYPSUM
  name = G4_GYPSUM
  specific = 4
FEATURE [App::DocumentObjectGroupPython] C_element052  label="C_element : 7"  # scripted group (container) (typed FeaturePython)
  n = 7
  ref = C_element
FEATURE [App::DocumentObjectGroupPython] H_element046  label="H_element : 16"  # scripted group (container) (typed FeaturePython)
  n = 16
  ref = H_element
FEATURE [App::DocumentObjectGroupPython] G4_N_HEPTANE  label="G4_N-HEPTANE"  # scripted group (container) (typed FeaturePython)
  Dunit = g/cm3
  Dvalue = 0.68376
  Group = -> [C_element052,H_element046]
  conduct = 2
  density = 1
  expand = 3
  formula = G4_N-HEPTANE
  name = G4_N-HEPTANE
  specific = 4
FEATURE [App::DocumentObjectGroupPython] C_element053  label="C_element : 029"  # scripted group (container) (typed FeaturePython)
  n = 6
  ref = C_element
FEATURE [App::DocumentObjectGroupPython] H_element047  label="H_element : 14"  # scripted group (container) (typed FeaturePython)
  n = 14
  ref = H_element
FEATURE [App::DocumentObjectGroupPython] G4_N_HEXANE  label="G4_N-HEXANE"  # scripted group (container) (typed FeaturePython)
  Dunit = g/cm3
  Dvalue = 0.6603
  Group = -> [C_element053,H_element047]
  conduct = 2
  density = 1
  expand = 3
  formula = G4_N-HEXANE
  name = G4_N-HEXANE
  specific = 4
FEATURE [App::DocumentObjectGroupPython] C_element054  label="C_element : 22"  # scripted group (container) (typed FeaturePython)
  n = 22
  ref = C_element
FEATURE [App::DocumentObjectGroupPython] H_element048  label="H_element : 025"  # scripted group (container) (typed FeaturePython)
  n = 10
  ref = H_element
FEATURE [App::DocumentObjectGroupPython] N_element021  label="N_element : 010"  # scripted group (container) (typed FeaturePython)
  n = 2
  ref = N_element
FEATURE [App::DocumentObjectGroupPython] O_element050  label="O_element : 025"  # scripted group (container) (typed FeaturePython)
  n = 5
  ref = O_element
FEATURE [App::DocumentObjectGroupPython] G4_KAPTON  # scripted group (container) (typed FeaturePython)
  Dunit = g/cm3
  Dvalue = 1.42
  Group = -> [C_element054,H_element048,N_element021,O_element050]
  conduct = 2
  density = 1
  expand = 3
  formula = G4_KAPTON
  name = G4_KAPTON
  specific = 4
FEATURE [App::DocumentObjectGroupPython] La_element001  label="La_element : 1"  # scripted group (container) (typed FeaturePython)
  n = 1
  ref = La_element
FEATURE [App::DocumentObjectGroupPython] Br_element003  label="Br_element : 002"  # scripted group (container) (typed FeaturePython)
  n = 1
  ref = Br_element
FEATURE [App::DocumentObjectGroupPython] O_element051  label="O_element : 026"  # scripted group (container) (typed FeaturePython)
  n = 1
  ref = O_element
FEATURE [App::DocumentObjectGroupPython] G4_LANTHANUM_OXYBROMIDE  # scripted group (container) (typed FeaturePython)
  Dunit = g/cm3
  Dvalue = 6.28
  Group = -> [La_element001,Br_element003,O_element051]
  conduct = 2
  density = 1
  expand = 3
  formula = G4_LANTHANUM_OXYBROMIDE
  name = G4_LANTHANUM_OXYBROMIDE
  specific = 4
FEATURE [App::DocumentObjectGroupPython] La_element002  label="La_element : 2"  # scripted group (container) (typed FeaturePython)
  n = 2
  ref = La_element
FEATURE [App::DocumentObjectGroupPython] O_element052  label="O_element : 027"  # scripted group (container) (typed FeaturePython)
  n = 2
  ref = O_element
FEATURE [App::DocumentObjectGroupPython] S_element015  label="S_element : 006"  # scripted group (container) (typed FeaturePython)
  n = 1
  ref = S_element
FEATURE [App::DocumentObjectGroupPython] G4_LANTHANUM_OXYSULFIDE  # scripted group (container) (typed FeaturePython)
  Dunit = g/cm3
  Dvalue = 5.86
  Group = -> [La_element002,O_element052,S_element015]
  conduct = 2
  density = 1
  expand = 3
  formula = G4_LANTHANUM_OXYSULFIDE
  name = G4_LANTHANUM_OXYSULFIDE
  specific = 4
FEATURE [App::DocumentObjectGroupPython] O_element053  label="O_element : 0.072"  # scripted group (container) (typed FeaturePython)
  n = 0.071682
FEATURE [App::DocumentObjectGroupPython] Pb_element002  label="Pb_element : 0.928"  # scripted group (container) (typed FeaturePython)
  n = 0.928318
FEATURE [App::DocumentObjectGroupPython] G4_LEAD_OXIDE  # scripted group (container) (typed FeaturePython)
  Dunit = g/cm3
  Dvalue = 9.53
  Group = -> [O_element053,Pb_element002]
  conduct = 2
  density = 1
  expand = 3
  formula = G4_LEAD_OXIDE
  name = G4_LEAD_OXIDE
  specific = 4
FEATURE [App::DocumentObjectGroupPython] Li_element001  label="Li_element : 1"  # scripted group (container) (typed FeaturePython)
  n = 1
  ref = Li_element
FEATURE [App::DocumentObjectGroupPython] N_element022  label="N_element : 011"  # scripted group (container) (typed FeaturePython)
  n = 1
  ref = N_element
FEATURE [App::DocumentObjectGroupPython] H_element049  label="H_element : 026"  # scripted group (container) (typed FeaturePython)
  n = 2
  ref = H_element
FEATURE [App::DocumentObjectGroupPython] G4_LITHIUM_AMIDE  # scripted group (container) (typed FeaturePython)
  Dunit = g/cm3
  Dvalue = 1.178
  Group = -> [Li_element001,N_element022,H_element049]
  conduct = 2
  density = 1
  expand = 3
  formula = G4_LITHIUM_AMIDE
  name = G4_LITHIUM_AMIDE
  specific = 4
FEATURE [App::DocumentObjectGroupPython] Li_element002  label="Li_element : 2"  # scripted group (container) (typed FeaturePython)
  n = 2
  ref = Li_element
FEATURE [App::DocumentObjectGroupPython] C_element055  label="C_element : 030"  # scripted group (container) (typed FeaturePython)
  n = 1
  ref = C_element
FEATURE [App::DocumentObjectGroupPython] O_element054  label="O_element : 028"  # scripted group (container) (typed FeaturePython)
  n = 3
  ref = O_element
FEATURE [App::DocumentObjectGroupPython] G4_LITHIUM_CARBONATE  # scripted group (container) (typed FeaturePython)
  Dunit = g/cm3
  Dvalue = 2.11
  Group = -> [Li_element002,C_element055,O_element054]
  conduct = 2
  density = 1
  expand = 3
  formula = G4_LITHIUM_CARBONATE
  name = G4_LITHIUM_CARBONATE
  specific = 4
FEATURE [App::DocumentObjectGroupPython] Li_element003  label="Li_element : 003"  # scripted group (container) (typed FeaturePython)
  n = 1
  ref = Li_element
FEATURE [App::DocumentObjectGroupPython] F_element012  label="F_element : 004"  # scripted group (container) (typed FeaturePython)
  n = 1
  ref = F_element
FEATURE [App::DocumentObjectGroupPython] G4_LITHIUM_FLUORIDE  # scripted group (container) (typed FeaturePython)
  Dunit = g/cm3
  Dvalue = 2.635
  Group = -> [Li_element003,F_element012]
  conduct = 2
  density = 1
  expand = 3
  formula = G4_LITHIUM_FLUORIDE
  name = G4_LITHIUM_FLUORIDE
  specific = 4
FEATURE [App::DocumentObjectGroupPython] Li_element004  label="Li_element : 004"  # scripted group (container) (typed FeaturePython)
  n = 1
  ref = Li_element
FEATURE [App::DocumentObjectGroupPython] H_element050  label="H_element : 027"  # scripted group (container) (typed FeaturePython)
  n = 1
  ref = H_element
FEATURE [App::DocumentObjectGroupPython] G4_LITHIUM_HYDRIDE  # scripted group (container) (typed FeaturePython)
  Dunit = g/cm3
  Dvalue = 0.82
  Group = -> [Li_element004,H_element050]
  conduct = 2
  density = 1
  expand = 3
  formula = G4_LITHIUM_HYDRIDE
  name = G4_LITHIUM_HYDRIDE
  specific = 4
FEATURE [App::DocumentObjectGroupPython] Li_element005  label="Li_element : 005"  # scripted group (container) (typed FeaturePython)
  n = 1
  ref = Li_element
FEATURE [App::DocumentObjectGroupPython] I_element003  label="I_element : 002"  # scripted group (container) (typed FeaturePython)
  n = 1
  ref = I_element
FEATURE [App::DocumentObjectGroupPython] G4_LITHIUM_IODIDE  # scripted group (container) (typed FeaturePython)
  Dunit = g/cm3
  Dvalue = 3.494
  Group = -> [Li_element005,I_element003]
  conduct = 2
  density = 1
  expand = 3
  formula = G4_LITHIUM_IODIDE
  name = G4_LITHIUM_IODIDE
  specific = 4
FEATURE [App::DocumentObjectGroupPython] Li_element006  label="Li_element : 006"  # scripted group (container) (typed FeaturePython)
  n = 2
  ref = Li_element
FEATURE [App::DocumentObjectGroupPython] O_element055  label="O_element : 029"  # scripted group (container) (typed FeaturePython)
  n = 1
  ref = O_element
FEATURE [App::DocumentObjectGroupPython] G4_LITHIUM_OXIDE  # scripted group (container) (typed FeaturePython)
  Dunit = g/cm3
  Dvalue = 2.013
  Group = -> [Li_element006,O_element055]
  conduct = 2
  density = 1
  expand = 3
  formula = G4_LITHIUM_OXIDE
  name = G4_LITHIUM_OXIDE
  specific = 4
FEATURE [App::DocumentObjectGroupPython] Li_element007  label="Li_element : 007"  # scripted group (container) (typed FeaturePython)
  n = 2
  ref = Li_element
FEATURE [App::DocumentObjectGroupPython] B_element005  label="B_element : 005"  # scripted group (container) (typed FeaturePython)
  n = 4
  ref = B_element
FEATURE [App::DocumentObjectGroupPython] O_element056  label="O_element : 7"  # scripted group (container) (typed FeaturePython)
  n = 7
  ref = O_element
FEATURE [App::DocumentObjectGroupPython] G4_LITHIUM_TETRABORATE  # scripted group (container) (typed FeaturePython)
  Dunit = g/cm3
  Dvalue = 2.44
  Group = -> [Li_element007,B_element005,O_element056]
  conduct = 2
  density = 1
  expand = 3
  formula = G4_LITHIUM_TETRABORATE
  name = G4_LITHIUM_TETRABORATE
  specific = 4
FEATURE [App::DocumentObjectGroupPython] H_element051  label="H_element : 0.105"  # scripted group (container) (typed FeaturePython)
  n = 0.105
FEATURE [App::DocumentObjectGroupPython] C_element056  label="C_element : 0.083"  # scripted group (container) (typed FeaturePython)
  n = 0.083
FEATURE [App::DocumentObjectGroupPython] N_element023  label="N_element : 0.023"  # scripted group (container) (typed FeaturePython)
  n = 0.023
FEATURE [App::DocumentObjectGroupPython] O_element057  label="O_element : 0.779"  # scripted group (container) (typed FeaturePython)
  n = 0.779
FEATURE [App::DocumentObjectGroupPython] Na_element010  label="Na_element : 0.097"  # scripted group (container) (typed FeaturePython)
  n = 0.002
FEATURE [App::DocumentObjectGroupPython] P_element006  label="P_element : 0.105"  # scripted group (container) (typed FeaturePython)
  n = 0.001
FEATURE [App::DocumentObjectGroupPython] S_element016  label="S_element : 0.017"  # scripted group (container) (typed FeaturePython)
  n = 0.002
FEATURE [App::DocumentObjectGroupPython] Cl_element014  label="Cl_element : 0.587"  # scripted group (container) (typed FeaturePython)
  n = 0.003
FEATURE [App::DocumentObjectGroupPython] K_element005  label="K_element : 0.015"  # scripted group (container) (typed FeaturePython)
  n = 0.002
FEATURE [App::DocumentObjectGroupPython] G4_LUNG_ICRP  # scripted group (container) (typed FeaturePython)
  Dunit = g/cm3
  Dvalue = 1.04
  Group = -> [H_element051,C_element056,N_element023,O_element057,Na_element010,P_element006,S_element016,Cl_element014,K_element005]
  conduct = 2
  density = 1
  expand = 3
  formula = G4_LUNG_ICRP
  name = G4_LUNG_ICRP
  specific = 4
FEATURE [App::DocumentObjectGroupPython] H_element052  label="H_element : 0.116"  # scripted group (container) (typed FeaturePython)
  n = 0.114318
FEATURE [App::DocumentObjectGroupPython] C_element057  label="C_element : 0.656"  # scripted group (container) (typed FeaturePython)
  n = 0.655824
FEATURE [App::DocumentObjectGroupPython] O_element058  label="O_element : 0.092"  # scripted group (container) (typed FeaturePython)
  n = 0.0921831
FEATURE [App::DocumentObjectGroupPython] Mg_element004  label="Mg_element : 0.135"  # scripted group (container) (typed FeaturePython)
  n = 0.134792
FEATURE [App::DocumentObjectGroupPython] Ca_element013  label="Ca_element : 0.003"  # scripted group (container) (typed FeaturePython)
  n = 0.002883
FEATURE [App::DocumentObjectGroupPython] G4_M3_WAX  # scripted group (container) (typed FeaturePython)
  Dunit = g/cm3
  Dvalue = 1.05
  Group = -> [H_element052,C_element057,O_element058,Mg_element004,Ca_element013]
  conduct = 2
  density = 1
  expand = 3
  formula = G4_M3_WAX
  name = G4_M3_WAX
  specific = 4
FEATURE [App::DocumentObjectGroupPython] Mg_element005  label="Mg_element : 1"  # scripted group (container) (typed FeaturePython)
  n = 1
  ref = Mg_element
FEATURE [App::DocumentObjectGroupPython] C_element058  label="C_element : 031"  # scripted group (container) (typed FeaturePython)
  n = 1
  ref = C_element
FEATURE [App::DocumentObjectGroupPython] O_element059  label="O_element : 030"  # scripted group (container) (typed FeaturePython)
  n = 3
  ref = O_element
FEATURE [App::DocumentObjectGroupPython] G4_MAGNESIUM_CARBONATE  # scripted group (container) (typed FeaturePython)
  Dunit = g/cm3
  Dvalue = 2.958
  Group = -> [Mg_element005,C_element058,O_element059]
  conduct = 2
  density = 1
  expand = 3
  formula = G4_MAGNESIUM_CARBONATE
  name = G4_MAGNESIUM_CARBONATE
  specific = 4
FEATURE [App::DocumentObjectGroupPython] Mg_element006  label="Mg_element : 002"  # scripted group (container) (typed FeaturePython)
  n = 1
  ref = Mg_element
FEATURE [App::DocumentObjectGroupPython] F_element013  label="F_element : 005"  # scripted group (container) (typed FeaturePython)
  n = 2
  ref = F_element
FEATURE [App::DocumentObjectGroupPython] G4_MAGNESIUM_FLUORIDE  # scripted group (container) (typed FeaturePython)
  Dunit = g/cm3
  Dvalue = 3
  Group = -> [Mg_element006,F_element013]
  conduct = 2
  density = 1
  expand = 3
  formula = G4_MAGNESIUM_FLUORIDE
  name = G4_MAGNESIUM_FLUORIDE
  specific = 4
FEATURE [App::DocumentObjectGroupPython] Mg_element007  label="Mg_element : 003"  # scripted group (container) (typed FeaturePython)
  n = 1
  ref = Mg_element
FEATURE [App::DocumentObjectGroupPython] O_element060  label="O_element : 031"  # scripted group (container) (typed FeaturePython)
  n = 1
  ref = O_element
FEATURE [App::DocumentObjectGroupPython] G4_MAGNESIUM_OXIDE  # scripted group (container) (typed FeaturePython)
  Dunit = g/cm3
  Dvalue = 3.58
  Group = -> [Mg_element007,O_element060]
  conduct = 2
  density = 1
  expand = 3
  formula = G4_MAGNESIUM_OXIDE
  name = G4_MAGNESIUM_OXIDE
  specific = 4
FEATURE [App::DocumentObjectGroupPython] Mg_element008  label="Mg_element : 004"  # scripted group (container) (typed FeaturePython)
  n = 1
  ref = Mg_element
FEATURE [App::DocumentObjectGroupPython] B_element006  label="B_element : 006"  # scripted group (container) (typed FeaturePython)
  n = 4
  ref = B_element
FEATURE [App::DocumentObjectGroupPython] O_element061  label="O_element : 032"  # scripted group (container) (typed FeaturePython)
  n = 7
  ref = O_element
FEATURE [App::DocumentObjectGroupPython] G4_MAGNESIUM_TETRABORATE  # scripted group (container) (typed FeaturePython)
  Dunit = g/cm3
  Dvalue = 2.53
  Group = -> [Mg_element008,B_element006,O_element061]
  conduct = 2
  density = 1
  expand = 3
  formula = G4_MAGNESIUM_TETRABORATE
  name = G4_MAGNESIUM_TETRABORATE
  specific = 4
FEATURE [App::DocumentObjectGroupPython] Hg_element001  label="Hg_element : 1"  # scripted group (container) (typed FeaturePython)
  n = 1
  ref = Hg_element
FEATURE [App::DocumentObjectGroupPython] I_element004  label="I_element : 2"  # scripted group (container) (typed FeaturePython)
  n = 2
  ref = I_element
FEATURE [App::DocumentObjectGroupPython] G4_MERCURIC_IODIDE  # scripted group (container) (typed FeaturePython)
  Dunit = g/cm3
  Dvalue = 6.36
  Group = -> [Hg_element001,I_element004]
  conduct = 2
  density = 1
  expand = 3
  formula = G4_MERCURIC_IODIDE
  name = G4_MERCURIC_IODIDE
  specific = 4
FEATURE [App::DocumentObjectGroupPython] C_element059  label="C_element : 032"  # scripted group (container) (typed FeaturePython)
  n = 1
  ref = C_element
FEATURE [App::DocumentObjectGroupPython] H_element053  label="H_element : 028"  # scripted group (container) (typed FeaturePython)
  n = 4
  ref = H_element
FEATURE [App::DocumentObjectGroupPython] G4_METHANE  # scripted group (container) (typed FeaturePython)
  Dunit = g/cm3
  Dvalue = 0.000667151
  Group = -> [C_element059,H_element053]
  conduct = 2
  density = 1
  expand = 3
  formula = G4_METHANE
  name = G4_METHANE
  specific = 4
FEATURE [App::DocumentObjectGroupPython] C_element060  label="C_element : 033"  # scripted group (container) (typed FeaturePython)
  n = 1
  ref = C_element
FEATURE [App::DocumentObjectGroupPython] H_element054  label="H_element : 029"  # scripted group (container) (typed FeaturePython)
  n = 4
  ref = H_element
FEATURE [App::DocumentObjectGroupPython] O_element062  label="O_element : 033"  # scripted group (container) (typed FeaturePython)
  n = 1
  ref = O_element
FEATURE [App::DocumentObjectGroupPython] G4_METHANOL  # scripted group (container) (typed FeaturePython)
  Dunit = g/cm3
  Dvalue = 0.7914
  Group = -> [C_element060,H_element054,O_element062]
  conduct = 2
  density = 1
  expand = 3
  formula = G4_METHANOL
  name = G4_METHANOL
  specific = 4
FEATURE [App::DocumentObjectGroupPython] H_element055  label="H_element : 0.134"  # scripted group (container) (typed FeaturePython)
  n = 0.13404
FEATURE [App::DocumentObjectGroupPython] C_element061  label="C_element : 0.778"  # scripted group (container) (typed FeaturePython)
  n = 0.77796
FEATURE [App::DocumentObjectGroupPython] O_element063  label="O_element : 0.035"  # scripted group (container) (typed FeaturePython)
  n = 0.03502
FEATURE [App::DocumentObjectGroupPython] Mg_element009  label="Mg_element : 0.039"  # scripted group (container) (typed FeaturePython)
  n = 0.038594
FEATURE [App::DocumentObjectGroupPython] Ti_element002  label="Ti_element : 0.014"  # scripted group (container) (typed FeaturePython)
  n = 0.014386
FEATURE [App::DocumentObjectGroupPython] G4_MIX_D_WAX  # scripted group (container) (typed FeaturePython)
  Dunit = g/cm3
  Dvalue = 0.99
  Group = -> [H_element055,C_element061,O_element063,Mg_element009,Ti_element002]
  conduct = 2
  density = 1
  expand = 3
  formula = G4_MIX_D_WAX
  name = G4_MIX_D_WAX
  specific = 4
FEATURE [App::DocumentObjectGroupPython] H_element056  label="H_element : 0.135"  # scripted group (container) (typed FeaturePython)
  n = 0.081192
FEATURE [App::DocumentObjectGroupPython] C_element062  label="C_element : 0.583"  # scripted group (container) (typed FeaturePython)
  n = 0.583442
FEATURE [App::DocumentObjectGroupPython] N_element024  label="N_element : 0.018"  # scripted group (container) (typed FeaturePython)
  n = 0.017798
FEATURE [App::DocumentObjectGroupPython] O_element064  label="O_element : 0.186"  # scripted group (container) (typed FeaturePython)
  n = 0.186381
FEATURE [App::DocumentObjectGroupPython] Mg_element010  label="Mg_element : 0.130"  # scripted group (container) (typed FeaturePython)
  n = 0.130287
FEATURE [App::DocumentObjectGroupPython] Cl_element015  label="Cl_element : 0.588"  # scripted group (container) (typed FeaturePython)
  n = 0.0009
FEATURE [App::DocumentObjectGroupPython] G4_MS20_TISSUE  # scripted group (container) (typed FeaturePython)
  Dunit = g/cm3
  Dvalue = 1
  Group = -> [H_element056,C_element062,N_element024,O_element064,Mg_element010,Cl_element015]
  conduct = 2
  density = 1
  expand = 3
  formula = G4_MS20_TISSUE
  name = G4_MS20_TISSUE
  specific = 4
FEATURE [App::DocumentObjectGroupPython] H_element057  label="H_element : 0.136"  # scripted group (container) (typed FeaturePython)
  n = 0.102
FEATURE [App::DocumentObjectGroupPython] C_element063  label="C_element : 0.143"  # scripted group (container) (typed FeaturePython)
  n = 0.143
FEATURE [App::DocumentObjectGroupPython] N_element025  label="N_element : 0.034"  # scripted group (container) (typed FeaturePython)
  n = 0.034
FEATURE [App::DocumentObjectGroupPython] O_element065  label="O_element : 0.710"  # scripted group (container) (typed FeaturePython)
  n = 0.71
FEATURE [App::DocumentObjectGroupPython] Na_element011  label="Na_element : 0.098"  # scripted group (container) (typed FeaturePython)
  n = 0.001
FEATURE [App::DocumentObjectGroupPython] P_element007  label="P_element : 0.002"  # scripted group (container) (typed FeaturePython)
  n = 0.002
FEATURE [App::DocumentObjectGroupPython] S_element017  label="S_element : 0.018"  # scripted group (container) (typed FeaturePython)
  n = 0.003
FEATURE [App::DocumentObjectGroupPython] Cl_element016  label="Cl_element : 0.589"  # scripted group (container) (typed FeaturePython)
  n = 0.001
FEATURE [App::DocumentObjectGroupPython] K_element006  label="K_element : 0.004"  # scripted group (container) (typed FeaturePython)
  n = 0.004
FEATURE [App::DocumentObjectGroupPython] G4_MUSCLE_SKELETAL_ICRP  # scripted group (container) (typed FeaturePython)
  Dunit = g/cm3
  Dvalue = 1.05
  Group = -> [H_element057,C_element063,N_element025,O_element065,Na_element011,P_element007,S_element017,Cl_element016,K_element006]
  conduct = 2
  density = 1
  expand = 3
  formula = G4_MUSCLE_SKELETAL_ICRP
  name = G4_MUSCLE_SKELETAL_ICRP
  specific = 4
FEATURE [App::DocumentObjectGroupPython] H_element058  label="H_element : 0.137"  # scripted group (container) (typed FeaturePython)
  n = 0.102102
FEATURE [App::DocumentObjectGroupPython] C_element064  label="C_element : 0.123"  # scripted group (container) (typed FeaturePython)
  n = 0.123123
FEATURE [App::DocumentObjectGroupPython] N_element026  label="N_element : 0.756"  # scripted group (container) (typed FeaturePython)
  n = 0.035035
FEATURE [App::DocumentObjectGroupPython] O_element066  label="O_element : 0.730"  # scripted group (container) (typed FeaturePython)
  n = 0.72973
FEATURE [App::DocumentObjectGroupPython] Na_element012  label="Na_element : 0.099"  # scripted group (container) (typed FeaturePython)
  n = 0.001001
FEATURE [App::DocumentObjectGroupPython] P_element008  label="P_element : 0.106"  # scripted group (container) (typed FeaturePython)
  n = 0.002002
FEATURE [App::DocumentObjectGroupPython] S_element018  label="S_element : 0.019"  # scripted group (container) (typed FeaturePython)
  n = 0.004004
FEATURE [App::DocumentObjectGroupPython] K_element007  label="K_element : 0.016"  # scripted group (container) (typed FeaturePython)
  n = 0.003003
FEATURE [App::DocumentObjectGroupPython] G4_MUSCLE_STRIATED_ICRU  # scripted group (container) (typed FeaturePython)
  Dunit = g/cm3
  Dvalue = 1.04
  Group = -> [H_element058,C_element064,N_element026,O_element066,Na_element012,P_element008,S_element018,K_element007]
  conduct = 2
  density = 1
  expand = 3
  formula = G4_MUSCLE_STRIATED_ICRU
  name = G4_MUSCLE_STRIATED_ICRU
  specific = 4
FEATURE [App::DocumentObjectGroupPython] H_element059  label="H_element : 0.098"  # scripted group (container) (typed FeaturePython)
  n = 0.0982341
FEATURE [App::DocumentObjectGroupPython] C_element065  label="C_element : 0.156"  # scripted group (container) (typed FeaturePython)
  n = 0.156214
FEATURE [App::DocumentObjectGroupPython] N_element027  label="N_element : 0.757"  # scripted group (container) (typed FeaturePython)
  n = 0.035451
FEATURE [App::DocumentObjectGroupPython] O_element067  label="O_element : 0.880"  # scripted group (container) (typed FeaturePython)
  n = 0.710101
FEATURE [App::DocumentObjectGroupPython] G4_MUSCLE_WITH_SUCROSE  # scripted group (container) (typed FeaturePython)
  Dunit = g/cm3
  Dvalue = 1.11
  Group = -> [H_element059,C_element065,N_element027,O_element067]
  conduct = 2
  density = 1
  expand = 3
  formula = G4_MUSCLE_WITH_SUCROSE
  name = G4_MUSCLE_WITH_SUCROSE
  specific = 4
FEATURE [App::DocumentObjectGroupPython] H_element060  label="H_element : 0.138"  # scripted group (container) (typed FeaturePython)
  n = 0.101969
FEATURE [App::DocumentObjectGroupPython] C_element066  label="C_element : 0.120"  # scripted group (container) (typed FeaturePython)
  n = 0.120058
FEATURE [App::DocumentObjectGroupPython] N_element028  label="N_element : 0.758"  # scripted group (container) (typed FeaturePython)
  n = 0.035451
FEATURE [App::DocumentObjectGroupPython] O_element068  label="O_element : 0.743"  # scripted group (container) (typed FeaturePython)
  n = 0.742522
FEATURE [App::DocumentObjectGroupPython] G4_MUSCLE_WITHOUT_SUCROSE  # scripted group (container) (typed FeaturePython)
  Dunit = g/cm3
  Dvalue = 1.07
  Group = -> [H_element060,C_element066,N_element028,O_element068]
  conduct = 2
  density = 1
  expand = 3
  formula = G4_MUSCLE_WITHOUT_SUCROSE
  name = G4_MUSCLE_WITHOUT_SUCROSE
  specific = 4
FEATURE [App::DocumentObjectGroupPython] C_element067  label="C_element : 10"  # scripted group (container) (typed FeaturePython)
  n = 10
  ref = C_element
FEATURE [App::DocumentObjectGroupPython] H_element061  label="H_element : 030"  # scripted group (container) (typed FeaturePython)
  n = 8
  ref = H_element
FEATURE [App::DocumentObjectGroupPython] G4_NAPHTHALENE  # scripted group (container) (typed FeaturePython)
  Dunit = g/cm3
  Dvalue = 1.145
  Group = -> [C_element067,H_element061]
  conduct = 2
  density = 1
  expand = 3
  formula = G4_NAPHTHALENE
  name = G4_NAPHTHALENE
  specific = 4
FEATURE [App::DocumentObjectGroupPython] C_element068  label="C_element : 034"  # scripted group (container) (typed FeaturePython)
  n = 6
  ref = C_element
FEATURE [App::DocumentObjectGroupPython] H_element062  label="H_element : 031"  # scripted group (container) (typed FeaturePython)
  n = 5
  ref = H_element
FEATURE [App::DocumentObjectGroupPython] N_element029  label="N_element : 012"  # scripted group (container) (typed FeaturePython)
  n = 1
  ref = N_element
FEATURE [App::DocumentObjectGroupPython] O_element069  label="O_element : 034"  # scripted group (container) (typed FeaturePython)
  n = 2
  ref = O_element
FEATURE [App::DocumentObjectGroupPython] G4_NITROBENZENE  # scripted group (container) (typed FeaturePython)
  Dunit = g/cm3
  Dvalue = 1.19867
  Group = -> [C_element068,H_element062,N_element029,O_element069]
  conduct = 2
  density = 1
  expand = 3
  formula = G4_NITROBENZENE
  name = G4_NITROBENZENE
  specific = 4
FEATURE [App::DocumentObjectGroupPython] N_element030  label="N_element : 013"  # scripted group (container) (typed FeaturePython)
  n = 2
  ref = N_element
FEATURE [App::DocumentObjectGroupPython] O_element070  label="O_element : 035"  # scripted group (container) (typed FeaturePython)
  n = 1
  ref = O_element
FEATURE [App::DocumentObjectGroupPython] G4_NITROUS_OXIDE  # scripted group (container) (typed FeaturePython)
  Dunit = g/cm3
  Dvalue = 0.00183094
  Group = -> [N_element030,O_element070]
  conduct = 2
  density = 1
  expand = 3
  formula = G4_NITROUS_OXIDE
  name = G4_NITROUS_OXIDE
  specific = 4
FEATURE [App::DocumentObjectGroupPython] H_element063  label="H_element : 0.104"  # scripted group (container) (typed FeaturePython)
  n = 0.103509
FEATURE [App::DocumentObjectGroupPython] C_element069  label="C_element : 0.648"  # scripted group (container) (typed FeaturePython)
  n = 0.648416
FEATURE [App::DocumentObjectGroupPython] N_element031  label="N_element : 0.100"  # scripted group (container) (typed FeaturePython)
  n = 0.0995361
FEATURE [App::DocumentObjectGroupPython] O_element071  label="O_element : 0.149"  # scripted group (container) (typed FeaturePython)
  n = 0.148539
FEATURE [App::DocumentObjectGroupPython] G4_NYLON_8062  label="G4_NYLON-8062"  # scripted group (container) (typed FeaturePython)
  Dunit = g/cm3
  Dvalue = 1.08
  Group = -> [H_element063,C_element069,N_element031,O_element071]
  conduct = 2
  density = 1
  expand = 3
  formula = G4_NYLON-8062
  name = G4_NYLON-8062
  specific = 4
FEATURE [App::DocumentObjectGroupPython] C_element070  label="C_element : 035"  # scripted group (container) (typed FeaturePython)
  n = 6
  ref = C_element
FEATURE [App::DocumentObjectGroupPython] H_element064  label="H_element : 11"  # scripted group (container) (typed FeaturePython)
  n = 11
  ref = H_element
FEATURE [App::DocumentObjectGroupPython] N_element032  label="N_element : 014"  # scripted group (container) (typed FeaturePython)
  n = 1
  ref = N_element
FEATURE [App::DocumentObjectGroupPython] O_element072  label="O_element : 036"  # scripted group (container) (typed FeaturePython)
  n = 1
  ref = O_element
FEATURE [App::DocumentObjectGroupPython] G4_NYLON_6_6  label="G4_NYLON-6-6"  # scripted group (container) (typed FeaturePython)
  Dunit = g/cm3
  Dvalue = 1.14
  Group = -> [C_element070,H_element064,N_element032,O_element072]
  conduct = 2
  density = 1
  expand = 3
  formula = G4_NYLON-6-6
  name = G4_NYLON-6-6
  specific = 4
FEATURE [App::DocumentObjectGroupPython] H_element065  label="H_element : 0.139"  # scripted group (container) (typed FeaturePython)
  n = 0.107062
FEATURE [App::DocumentObjectGroupPython] C_element071  label="C_element : 0.680"  # scripted group (container) (typed FeaturePython)
  n = 0.680449
FEATURE [App::DocumentObjectGroupPython] N_element033  label="N_element : 0.099"  # scripted group (container) (typed FeaturePython)
  n = 0.099189
FEATURE [App::DocumentObjectGroupPython] O_element073  label="O_element : 0.113"  # scripted group (container) (typed FeaturePython)
  n = 0.1133
FEATURE [App::DocumentObjectGroupPython] G4_NYLON_6_10  label="G4_NYLON-6-10"  # scripted group (container) (typed FeaturePython)
  Dunit = g/cm3
  Dvalue = 1.14
  Group = -> [H_element065,C_element071,N_element033,O_element073]
  conduct = 2
  density = 1
  expand = 3
  formula = G4_NYLON-6-10
  name = G4_NYLON-6-10
  specific = 4
FEATURE [App::DocumentObjectGroupPython] H_element066  label="H_element : 0.140"  # scripted group (container) (typed FeaturePython)
  n = 0.115476
FEATURE [App::DocumentObjectGroupPython] C_element072  label="C_element : 0.721"  # scripted group (container) (typed FeaturePython)
  n = 0.720818
FEATURE [App::DocumentObjectGroupPython] N_element034  label="N_element : 0.076"  # scripted group (container) (typed FeaturePython)
  n = 0.0764169
FEATURE [App::DocumentObjectGroupPython] O_element074  label="O_element : 0.087"  # scripted group (container) (typed FeaturePython)
  n = 0.0872889
FEATURE [App::DocumentObjectGroupPython] G4_NYLON_11_RILSAN  label="G4_NYLON-11_RILSAN"  # scripted group (container) (typed FeaturePython)
  Dunit = g/cm3
  Dvalue = 1.425
  Group = -> [H_element066,C_element072,N_element034,O_element074]
  conduct = 2
  density = 1
  expand = 3
  formula = G4_NYLON-11_RILSAN
  name = G4_NYLON-11_RILSAN
  specific = 4
FEATURE [App::DocumentObjectGroupPython] C_element073  label="C_element : 8"  # scripted group (container) (typed FeaturePython)
  n = 8
  ref = C_element
FEATURE [App::DocumentObjectGroupPython] H_element067  label="H_element : 18"  # scripted group (container) (typed FeaturePython)
  n = 18
  ref = H_element
FEATURE [App::DocumentObjectGroupPython] G4_OCTANE  # scripted group (container) (typed FeaturePython)
  Dunit = g/cm3
  Dvalue = 0.7026
  Group = -> [C_element073,H_element067]
  conduct = 2
  density = 1
  expand = 3
  formula = G4_OCTANE
  name = G4_OCTANE
  specific = 4
FEATURE [App::DocumentObjectGroupPython] C_element074  label="C_element : 25"  # scripted group (container) (typed FeaturePython)
  n = 25
  ref = C_element
FEATURE [App::DocumentObjectGroupPython] H_element068  label="H_element : 52"  # scripted group (container) (typed FeaturePython)
  n = 52
  ref = H_element
FEATURE [App::DocumentObjectGroupPython] G4_PARAFFIN  # scripted group (container) (typed FeaturePython)
  Dunit = g/cm3
  Dvalue = 0.93
  Group = -> [C_element074,H_element068]
  conduct = 2
  density = 1
  expand = 3
  formula = G4_PARAFFIN
  name = G4_PARAFFIN
  specific = 4
FEATURE [App::DocumentObjectGroupPython] C_element075  label="C_element : 036"  # scripted group (container) (typed FeaturePython)
  n = 5
  ref = C_element
FEATURE [App::DocumentObjectGroupPython] H_element069  label="H_element : 032"  # scripted group (container) (typed FeaturePython)
  n = 12
  ref = H_element
FEATURE [App::DocumentObjectGroupPython] G4_N_PENTANE  label="G4_N-PENTANE"  # scripted group (container) (typed FeaturePython)
  Dunit = g/cm3
  Dvalue = 0.6262
  Group = -> [C_element075,H_element069]
  conduct = 2
  density = 1
  expand = 3
  formula = G4_N-PENTANE
  name = G4_N-PENTANE
  specific = 4
FEATURE [App::DocumentObjectGroupPython] H_element070  label="H_element : 0.014"  # scripted group (container) (typed FeaturePython)
  n = 0.0141
FEATURE [App::DocumentObjectGroupPython] C_element076  label="C_element : 0.072"  # scripted group (container) (typed FeaturePython)
  n = 0.072261
FEATURE [App::DocumentObjectGroupPython] N_element035  label="N_element : 0.019"  # scripted group (container) (typed FeaturePython)
  n = 0.01932
FEATURE [App::DocumentObjectGroupPython] O_element075  label="O_element : 0.066"  # scripted group (container) (typed FeaturePython)
  n = 0.066101
FEATURE [App::DocumentObjectGroupPython] S_element019  label="S_element : 0.020"  # scripted group (container) (typed FeaturePython)
  n = 0.00189
FEATURE [App::DocumentObjectGroupPython] Br_element004  label="Br_element : 0.349"  # scripted group (container) (typed FeaturePython)
  n = 0.349103
FEATURE [App::DocumentObjectGroupPython] Ag_element001  label="Ag_element : 0.474"  # scripted group (container) (typed FeaturePython)
  n = 0.474105
FEATURE [App::DocumentObjectGroupPython] I_element005  label="I_element : 0.003"  # scripted group (container) (typed FeaturePython)
  n = 0.00312
FEATURE [App::DocumentObjectGroupPython] G4_PHOTO_EMULSION  # scripted group (container) (typed FeaturePython)
  Dunit = g/cm3
  Dvalue = 3.815
  Group = -> [H_element070,C_element076,N_element035,O_element075,S_element019,Br_element004,Ag_element001,I_element005]
  conduct = 2
  density = 1
  expand = 3
  formula = G4_PHOTO_EMULSION
  name = G4_PHOTO_EMULSION
  specific = 4
FEATURE [App::DocumentObjectGroupPython] C_element077  label="C_element : 9"  # scripted group (container) (typed FeaturePython)
  n = 9
  ref = C_element
FEATURE [App::DocumentObjectGroupPython] H_element071  label="H_element : 033"  # scripted group (container) (typed FeaturePython)
  n = 10
  ref = H_element
FEATURE [App::DocumentObjectGroupPython] G4_PLASTIC_SC_VINYLTOLUENE  # scripted group (container) (typed FeaturePython)
  Dunit = g/cm3
  Dvalue = 1.032
  Group = -> [C_element077,H_element071]
  conduct = 2
  density = 1
  expand = 3
  formula = G4_PLASTIC_SC_VINYLTOLUENE
  name = G4_PLASTIC_SC_VINYLTOLUENE
  specific = 4
FEATURE [App::DocumentObjectGroupPython] Pu_element001  label="Pu_element : 1"  # scripted group (container) (typed FeaturePython)
  n = 1
  ref = Pu_element
FEATURE [App::DocumentObjectGroupPython] O_element076  label="O_element : 037"  # scripted group (container) (typed FeaturePython)
  n = 2
  ref = O_element
FEATURE [App::DocumentObjectGroupPython] G4_PLUTONIUM_DIOXIDE  # scripted group (container) (typed FeaturePython)
  Dunit = g/cm3
  Dvalue = 11.46
  Group = -> [Pu_element001,O_element076]
  conduct = 2
  density = 1
  expand = 3
  formula = G4_PLUTONIUM_DIOXIDE
  name = G4_PLUTONIUM_DIOXIDE
  specific = 4
FEATURE [App::DocumentObjectGroupPython] C_element078  label="C_element : 037"  # scripted group (container) (typed FeaturePython)
  n = 3
  ref = C_element
FEATURE [App::DocumentObjectGroupPython] H_element072  label="H_element : 034"  # scripted group (container) (typed FeaturePython)
  n = 3
  ref = H_element
FEATURE [App::DocumentObjectGroupPython] N_element036  label="N_element : 015"  # scripted group (container) (typed FeaturePython)
  n = 1
  ref = N_element
FEATURE [App::DocumentObjectGroupPython] G4_POLYACRYLONITRILE  # scripted group (container) (typed FeaturePython)
  Dunit = g/cm3
  Dvalue = 1.17
  Group = -> [C_element078,H_element072,N_element036]
  conduct = 2
  density = 1
  expand = 3
  formula = G4_POLYACRYLONITRILE
  name = G4_POLYACRYLONITRILE
  specific = 4
FEATURE [App::DocumentObjectGroupPython] C_element079  label="C_element : 16"  # scripted group (container) (typed FeaturePython)
  n = 16
  ref = C_element
FEATURE [App::DocumentObjectGroupPython] H_element073  label="H_element : 035"  # scripted group (container) (typed FeaturePython)
  n = 14
  ref = H_element
FEATURE [App::DocumentObjectGroupPython] O_element077  label="O_element : 038"  # scripted group (container) (typed FeaturePython)
  n = 3
  ref = O_element
FEATURE [App::DocumentObjectGroupPython] G4_POLYCARBONATE  # scripted group (container) (typed FeaturePython)
  Dunit = g/cm3
  Dvalue = 1.2
  Group = -> [C_element079,H_element073,O_element077]
  conduct = 2
  density = 1
  expand = 3
  formula = G4_POLYCARBONATE
  name = G4_POLYCARBONATE
  specific = 4
FEATURE [App::DocumentObjectGroupPython] C_element080  label="C_element : 038"  # scripted group (container) (typed FeaturePython)
  n = 8
  ref = C_element
FEATURE [App::DocumentObjectGroupPython] H_element074  label="H_element : 036"  # scripted group (container) (typed FeaturePython)
  n = 7
  ref = H_element
FEATURE [App::DocumentObjectGroupPython] Cl_element017  label="Cl_element : 007"  # scripted group (container) (typed FeaturePython)
  n = 1
  ref = Cl_element
FEATURE [App::DocumentObjectGroupPython] G4_POLYCHLOROSTYRENE  # scripted group (container) (typed FeaturePython)
  Dunit = g/cm3
  Dvalue = 1.3
  Group = -> [C_element080,H_element074,Cl_element017]
  conduct = 2
  density = 1
  expand = 3
  formula = G4_POLYCHLOROSTYRENE
  name = G4_POLYCHLOROSTYRENE
  specific = 4
FEATURE [App::DocumentObjectGroupPython] C_element081  label="C_element : 039"  # scripted group (container) (typed FeaturePython)
  n = 1
  ref = C_element
FEATURE [App::DocumentObjectGroupPython] H_element075  label="H_element : 037"  # scripted group (container) (typed FeaturePython)
  n = 2
  ref = H_element
FEATURE [App::DocumentObjectGroupPython] G4_POLYETHYLENE  # scripted group (container) (typed FeaturePython)
  Dunit = g/cm3
  Dvalue = 0.94
  Group = -> [C_element081,H_element075]
  conduct = 2
  density = 1
  expand = 3
  formula = G4_POLYETHYLENE
  name = G4_POLYETHYLENE
  specific = 4
FEATURE [App::DocumentObjectGroupPython] C_element082  label="C_element : 040"  # scripted group (container) (typed FeaturePython)
  n = 10
  ref = C_element
FEATURE [App::DocumentObjectGroupPython] H_element076  label="H_element : 038"  # scripted group (container) (typed FeaturePython)
  n = 8
  ref = H_element
FEATURE [App::DocumentObjectGroupPython] O_element078  label="O_element : 039"  # scripted group (container) (typed FeaturePython)
  n = 4
  ref = O_element
FEATURE [App::DocumentObjectGroupPython] G4_MYLAR  # scripted group (container) (typed FeaturePython)
  Dunit = g/cm3
  Dvalue = 1.4
  Group = -> [C_element082,H_element076,O_element078]
  conduct = 2
  density = 1
  expand = 3
  formula = G4_MYLAR
  name = G4_MYLAR
  specific = 4
FEATURE [App::DocumentObjectGroupPython] C_element083  label="C_element : 041"  # scripted group (container) (typed FeaturePython)
  n = 5
  ref = C_element
FEATURE [App::DocumentObjectGroupPython] H_element077  label="H_element : 039"  # scripted group (container) (typed FeaturePython)
  n = 8
  ref = H_element
FEATURE [App::DocumentObjectGroupPython] O_element079  label="O_element : 040"  # scripted group (container) (typed FeaturePython)
  n = 2
  ref = O_element
FEATURE [App::DocumentObjectGroupPython] G4_PLEXIGLASS  # scripted group (container) (typed FeaturePython)
  Dunit = g/cm3
  Dvalue = 1.19
  Group = -> [C_element083,H_element077,O_element079]
  conduct = 2
  density = 1
  expand = 3
  formula = G4_PLEXIGLASS
  name = G4_PLEXIGLASS
  specific = 4
FEATURE [App::DocumentObjectGroupPython] C_element084  label="C_element : 042"  # scripted group (container) (typed FeaturePython)
  n = 1
  ref = C_element
FEATURE [App::DocumentObjectGroupPython] H_element078  label="H_element : 040"  # scripted group (container) (typed FeaturePython)
  n = 2
  ref = H_element
FEATURE [App::DocumentObjectGroupPython] O_element080  label="O_element : 041"  # scripted group (container) (typed FeaturePython)
  n = 1
  ref = O_element
FEATURE [App::DocumentObjectGroupPython] G4_POLYOXYMETHYLENE  # scripted group (container) (typed FeaturePython)
  Dunit = g/cm3
  Dvalue = 1.425
  Group = -> [C_element084,H_element078,O_element080]
  conduct = 2
  density = 1
  expand = 3
  formula = G4_POLYOXYMETHYLENE
  name = G4_POLYOXYMETHYLENE
  specific = 4
FEATURE [App::DocumentObjectGroupPython] C_element085  label="C_element : 043"  # scripted group (container) (typed FeaturePython)
  n = 2
  ref = C_element
FEATURE [App::DocumentObjectGroupPython] H_element079  label="H_element : 041"  # scripted group (container) (typed FeaturePython)
  n = 4
  ref = H_element
FEATURE [App::DocumentObjectGroupPython] G4_POLYPROPYLENE  # scripted group (container) (typed FeaturePython)
  Dunit = g/cm3
  Dvalue = 0.9
  Group = -> [C_element085,H_element079]
  conduct = 2
  density = 1
  expand = 3
  formula = G4_POLYPROPYLENE
  name = G4_POLYPROPYLENE
  specific = 4
FEATURE [App::DocumentObjectGroupPython] C_element086  label="C_element : 044"  # scripted group (container) (typed FeaturePython)
  n = 8
  ref = C_element
FEATURE [App::DocumentObjectGroupPython] H_element080  label="H_element : 042"  # scripted group (container) (typed FeaturePython)
  n = 8
  ref = H_element
FEATURE [App::DocumentObjectGroupPython] G4_POLYSTYRENE  # scripted group (container) (typed FeaturePython)
  Dunit = g/cm3
  Dvalue = 1.06
  Group = -> [C_element086,H_element080]
  conduct = 2
  density = 1
  expand = 3
  formula = G4_POLYSTYRENE
  name = G4_POLYSTYRENE
  specific = 4
FEATURE [App::DocumentObjectGroupPython] C_element087  label="C_element : 045"  # scripted group (container) (typed FeaturePython)
  n = 2
  ref = C_element
FEATURE [App::DocumentObjectGroupPython] F_element014  label="F_element : 4"  # scripted group (container) (typed FeaturePython)
  n = 4
  ref = F_element
FEATURE [App::DocumentObjectGroupPython] G4_TEFLON  # scripted group (container) (typed FeaturePython)
  Dunit = g/cm3
  Dvalue = 2.2
  Group = -> [C_element087,F_element014]
  conduct = 2
  density = 1
  expand = 3
  formula = G4_TEFLON
  name = G4_TEFLON
  specific = 4
FEATURE [App::DocumentObjectGroupPython] C_element088  label="C_element : 046"  # scripted group (container) (typed FeaturePython)
  n = 2
  ref = C_element
FEATURE [App::DocumentObjectGroupPython] F_element015  label="F_element : 006"  # scripted group (container) (typed FeaturePython)
  n = 3
  ref = F_element
FEATURE [App::DocumentObjectGroupPython] Cl_element018  label="Cl_element : 008"  # scripted group (container) (typed FeaturePython)
  n = 1
  ref = Cl_element
FEATURE [App::DocumentObjectGroupPython] G4_POLYTRIFLUOROCHLOROETHYLENE  # scripted group (container) (typed FeaturePython)
  Dunit = g/cm3
  Dvalue = 2.1
  Group = -> [C_element088,F_element015,Cl_element018]
  conduct = 2
  density = 1
  expand = 3
  formula = G4_POLYTRIFLUOROCHLOROETHYLENE
  name = G4_POLYTRIFLUOROCHLOROETHYLENE
  specific = 4
FEATURE [App::DocumentObjectGroupPython] C_element089  label="C_element : 047"  # scripted group (container) (typed FeaturePython)
  n = 4
  ref = C_element
FEATURE [App::DocumentObjectGroupPython] H_element081  label="H_element : 043"  # scripted group (container) (typed FeaturePython)
  n = 6
  ref = H_element
FEATURE [App::DocumentObjectGroupPython] O_element081  label="O_element : 042"  # scripted group (container) (typed FeaturePython)
  n = 2
  ref = O_element
FEATURE [App::DocumentObjectGroupPython] G4_POLYVINYL_ACETATE  # scripted group (container) (typed FeaturePython)
  Dunit = g/cm3
  Dvalue = 1.19
  Group = -> [C_element089,H_element081,O_element081]
  conduct = 2
  density = 1
  expand = 3
  formula = G4_POLYVINYL_ACETATE
  name = G4_POLYVINYL_ACETATE
  specific = 4
FEATURE [App::DocumentObjectGroupPython] C_element090  label="C_element : 048"  # scripted group (container) (typed FeaturePython)
  n = 2
  ref = C_element
FEATURE [App::DocumentObjectGroupPython] H_element082  label="H_element : 044"  # scripted group (container) (typed FeaturePython)
  n = 4
  ref = H_element
FEATURE [App::DocumentObjectGroupPython] O_element082  label="O_element : 043"  # scripted group (container) (typed FeaturePython)
  n = 1
  ref = O_element
FEATURE [App::DocumentObjectGroupPython] G4_POLYVINYL_ALCOHOL  # scripted group (container) (typed FeaturePython)
  Dunit = g/cm3
  Dvalue = 1.3
  Group = -> [C_element090,H_element082,O_element082]
  conduct = 2
  density = 1
  expand = 3
  formula = G4_POLYVINYL_ALCOHOL
  name = G4_POLYVINYL_ALCOHOL
  specific = 4
FEATURE [App::DocumentObjectGroupPython] C_element091  label="C_element : 049"  # scripted group (container) (typed FeaturePython)
  n = 8
  ref = C_element
FEATURE [App::DocumentObjectGroupPython] H_element083  label="H_element : 045"  # scripted group (container) (typed FeaturePython)
  n = 14
  ref = H_element
FEATURE [App::DocumentObjectGroupPython] O_element083  label="O_element : 044"  # scripted group (container) (typed FeaturePython)
  n = 2
  ref = O_element
FEATURE [App::DocumentObjectGroupPython] G4_POLYVINYL_BUTYRAL  # scripted group (container) (typed FeaturePython)
  Dunit = g/cm3
  Dvalue = 1.12
  Group = -> [C_element091,H_element083,O_element083]
  conduct = 2
  density = 1
  expand = 3
  formula = G4_POLYVINYL_BUTYRAL
  name = G4_POLYVINYL_BUTYRAL
  specific = 4
FEATURE [App::DocumentObjectGroupPython] C_element092  label="C_element : 050"  # scripted group (container) (typed FeaturePython)
  n = 2
  ref = C_element
FEATURE [App::DocumentObjectGroupPython] H_element084  label="H_element : 046"  # scripted group (container) (typed FeaturePython)
  n = 3
  ref = H_element
FEATURE [App::DocumentObjectGroupPython] Cl_element019  label="Cl_element : 009"  # scripted group (container) (typed FeaturePython)
  n = 1
  ref = Cl_element
FEATURE [App::DocumentObjectGroupPython] G4_POLYVINYL_CHLORIDE  # scripted group (container) (typed FeaturePython)
  Dunit = g/cm3
  Dvalue = 1.3
  Group = -> [C_element092,H_element084,Cl_element019]
  conduct = 2
  density = 1
  expand = 3
  formula = G4_POLYVINYL_CHLORIDE
  name = G4_POLYVINYL_CHLORIDE
  specific = 4
FEATURE [App::DocumentObjectGroupPython] C_element093  label="C_element : 051"  # scripted group (container) (typed FeaturePython)
  n = 2
  ref = C_element
FEATURE [App::DocumentObjectGroupPython] H_element085  label="H_element : 047"  # scripted group (container) (typed FeaturePython)
  n = 2
  ref = H_element
FEATURE [App::DocumentObjectGroupPython] Cl_element020  label="Cl_element : 010"  # scripted group (container) (typed FeaturePython)
  n = 2
  ref = Cl_element
FEATURE [App::DocumentObjectGroupPython] G4_POLYVINYLIDENE_CHLORIDE  # scripted group (container) (typed FeaturePython)
  Dunit = g/cm3
  Dvalue = 1.7
  Group = -> [C_element093,H_element085,Cl_element020]
  conduct = 2
  density = 1
  expand = 3
  formula = G4_POLYVINYLIDENE_CHLORIDE
  name = G4_POLYVINYLIDENE_CHLORIDE
  specific = 4
FEATURE [App::DocumentObjectGroupPython] C_element094  label="C_element : 052"  # scripted group (container) (typed FeaturePython)
  n = 2
  ref = C_element
FEATURE [App::DocumentObjectGroupPython] H_element086  label="H_element : 048"  # scripted group (container) (typed FeaturePython)
  n = 2
  ref = H_element
FEATURE [App::DocumentObjectGroupPython] F_element016  label="F_element : 007"  # scripted group (container) (typed FeaturePython)
  n = 2
  ref = F_element
FEATURE [App::DocumentObjectGroupPython] G4_POLYVINYLIDENE_FLUORIDE  # scripted group (container) (typed FeaturePython)
  Dunit = g/cm3
  Dvalue = 1.76
  Group = -> [C_element094,H_element086,F_element016]
  conduct = 2
  density = 1
  expand = 3
  formula = G4_POLYVINYLIDENE_FLUORIDE
  name = G4_POLYVINYLIDENE_FLUORIDE
  specific = 4
FEATURE [App::DocumentObjectGroupPython] C_element095  label="C_element : 053"  # scripted group (container) (typed FeaturePython)
  n = 6
  ref = C_element
FEATURE [App::DocumentObjectGroupPython] H_element087  label="H_element : 9"  # scripted group (container) (typed FeaturePython)
  n = 9
  ref = H_element
FEATURE [App::DocumentObjectGroupPython] N_element037  label="N_element : 016"  # scripted group (container) (typed FeaturePython)
  n = 1
  ref = N_element
FEATURE [App::DocumentObjectGroupPython] O_element084  label="O_element : 045"  # scripted group (container) (typed FeaturePython)
  n = 1
  ref = O_element
FEATURE [App::DocumentObjectGroupPython] G4_POLYVINYL_PYRROLIDONE  # scripted group (container) (typed FeaturePython)
  Dunit = g/cm3
  Dvalue = 1.25
  Group = -> [C_element095,H_element087,N_element037,O_element084]
  conduct = 2
  density = 1
  expand = 3
  formula = G4_POLYVINYL_PYRROLIDONE
  name = G4_POLYVINYL_PYRROLIDONE
  specific = 4
FEATURE [App::DocumentObjectGroupPython] K_element008  label="K_element : 1"  # scripted group (container) (typed FeaturePython)
  n = 1
  ref = K_element
FEATURE [App::DocumentObjectGroupPython] I_element006  label="I_element : 003"  # scripted group (container) (typed FeaturePython)
  n = 1
  ref = I_element
FEATURE [App::DocumentObjectGroupPython] G4_POTASSIUM_IODIDE  # scripted group (container) (typed FeaturePython)
  Dunit = g/cm3
  Dvalue = 3.13
  Group = -> [K_element008,I_element006]
  conduct = 2
  density = 1
  expand = 3
  formula = G4_POTASSIUM_IODIDE
  name = G4_POTASSIUM_IODIDE
  specific = 4
FEATURE [App::DocumentObjectGroupPython] K_element009  label="K_element : 2"  # scripted group (container) (typed FeaturePython)
  n = 2
  ref = K_element
FEATURE [App::DocumentObjectGroupPython] O_element085  label="O_element : 046"  # scripted group (container) (typed FeaturePython)
  n = 1
  ref = O_element
FEATURE [App::DocumentObjectGroupPython] G4_POTASSIUM_OXIDE  # scripted group (container) (typed FeaturePython)
  Dunit = g/cm3
  Dvalue = 2.32
  Group = -> [K_element009,O_element085]
  conduct = 2
  density = 1
  expand = 3
  formula = G4_POTASSIUM_OXIDE
  name = G4_POTASSIUM_OXIDE
  specific = 4
FEATURE [App::DocumentObjectGroupPython] C_element096  label="C_element : 054"  # scripted group (container) (typed FeaturePython)
  n = 3
  ref = C_element
FEATURE [App::DocumentObjectGroupPython] H_element088  label="H_element : 049"  # scripted group (container) (typed FeaturePython)
  n = 8
  ref = H_element
FEATURE [App::DocumentObjectGroupPython] G4_PROPANE  # scripted group (container) (typed FeaturePython)
  Dunit = g/cm3
  Dvalue = 0.00187939
  Group = -> [C_element096,H_element088]
  conduct = 2
  density = 1
  expand = 3
  formula = G4_PROPANE
  name = G4_PROPANE
  specific = 4
FEATURE [App::DocumentObjectGroupPython] C_element097  label="C_element : 055"  # scripted group (container) (typed FeaturePython)
  n = 3
  ref = C_element
FEATURE [App::DocumentObjectGroupPython] H_element089  label="H_element : 050"  # scripted group (container) (typed FeaturePython)
  n = 8
  ref = H_element
FEATURE [App::DocumentObjectGroupPython] G4_lPROPANE  # scripted group (container) (typed FeaturePython)
  Dunit = g/cm3
  Dvalue = 0.43
  Group = -> [C_element097,H_element089]
  conduct = 2
  density = 1
  expand = 3
  formula = G4_lPROPANE
  name = G4_lPROPANE
  specific = 4
FEATURE [App::DocumentObjectGroupPython] C_element098  label="C_element : 056"  # scripted group (container) (typed FeaturePython)
  n = 3
  ref = C_element
FEATURE [App::DocumentObjectGroupPython] H_element090  label="H_element : 051"  # scripted group (container) (typed FeaturePython)
  n = 8
  ref = H_element
FEATURE [App::DocumentObjectGroupPython] O_element086  label="O_element : 047"  # scripted group (container) (typed FeaturePython)
  n = 1
  ref = O_element
FEATURE [App::DocumentObjectGroupPython] G4_N_PROPYL_ALCOHOL  label="G4_N-PROPYL_ALCOHOL"  # scripted group (container) (typed FeaturePython)
  Dunit = g/cm3
  Dvalue = 0.8035
  Group = -> [C_element098,H_element090,O_element086]
  conduct = 2
  density = 1
  expand = 3
  formula = G4_N-PROPYL_ALCOHOL
  name = G4_N-PROPYL_ALCOHOL
  specific = 4
FEATURE [App::DocumentObjectGroupPython] C_element099  label="C_element : 057"  # scripted group (container) (typed FeaturePython)
  n = 5
  ref = C_element
FEATURE [App::DocumentObjectGroupPython] H_element091  label="H_element : 052"  # scripted group (container) (typed FeaturePython)
  n = 5
  ref = H_element
FEATURE [App::DocumentObjectGroupPython] N_element038  label="N_element : 017"  # scripted group (container) (typed FeaturePython)
  n = 1
  ref = N_element
FEATURE [App::DocumentObjectGroupPython] G4_PYRIDINE  # scripted group (container) (typed FeaturePython)
  Dunit = g/cm3
  Dvalue = 0.9819
  Group = -> [C_element099,H_element091,N_element038]
  conduct = 2
  density = 1
  expand = 3
  formula = G4_PYRIDINE
  name = G4_PYRIDINE
  specific = 4
FEATURE [App::DocumentObjectGroupPython] H_element092  label="H_element : 0.144"  # scripted group (container) (typed FeaturePython)
  n = 0.143711
FEATURE [App::DocumentObjectGroupPython] C_element100  label="C_element : 0.856"  # scripted group (container) (typed FeaturePython)
  n = 0.856289
FEATURE [App::DocumentObjectGroupPython] G4_RUBBER_BUTYL  # scripted group (container) (typed FeaturePython)
  Dunit = g/cm3
  Dvalue = 0.92
  Group = -> [H_element092,C_element100]
  conduct = 2
  density = 1
  expand = 3
  formula = G4_RUBBER_BUTYL
  name = G4_RUBBER_BUTYL
  specific = 4
FEATURE [App::DocumentObjectGroupPython] H_element093  label="H_element : 0.118"  # scripted group (container) (typed FeaturePython)
  n = 0.118371
FEATURE [App::DocumentObjectGroupPython] C_element101  label="C_element : 0.882"  # scripted group (container) (typed FeaturePython)
  n = 0.881629
FEATURE [App::DocumentObjectGroupPython] G4_RUBBER_NATURAL  # scripted group (container) (typed FeaturePython)
  Dunit = g/cm3
  Dvalue = 0.92
  Group = -> [H_element093,C_element101]
  conduct = 2
  density = 1
  expand = 3
  formula = G4_RUBBER_NATURAL
  name = G4_RUBBER_NATURAL
  specific = 4
FEATURE [App::DocumentObjectGroupPython] H_element094  label="H_element : 0.145"  # scripted group (container) (typed FeaturePython)
  n = 0.05692
FEATURE [App::DocumentObjectGroupPython] C_element102  label="C_element : 0.543"  # scripted group (container) (typed FeaturePython)
  n = 0.542646
FEATURE [App::DocumentObjectGroupPython] Cl_element021  label="Cl_element : 0.400"  # scripted group (container) (typed FeaturePython)
  n = 0.400434
FEATURE [App::DocumentObjectGroupPython] G4_RUBBER_NEOPRENE  # scripted group (container) (typed FeaturePython)
  Dunit = g/cm3
  Dvalue = 1.23
  Group = -> [H_element094,C_element102,Cl_element021]
  conduct = 2
  density = 1
  expand = 3
  formula = G4_RUBBER_NEOPRENE
  name = G4_RUBBER_NEOPRENE
  specific = 4
FEATURE [App::DocumentObjectGroupPython] Si_element006  label="Si_element : 1"  # scripted group (container) (typed FeaturePython)
  n = 1
  ref = Si_element
FEATURE [App::DocumentObjectGroupPython] O_element087  label="O_element : 048"  # scripted group (container) (typed FeaturePython)
  n = 2
  ref = O_element
FEATURE [App::DocumentObjectGroupPython] G4_SILICON_DIOXIDE  # scripted group (container) (typed FeaturePython)
  Dunit = g/cm3
  Dvalue = 2.32
  Group = -> [Si_element006,O_element087]
  conduct = 2
  density = 1
  expand = 3
  formula = G4_SILICON_DIOXIDE
  name = G4_SILICON_DIOXIDE
  specific = 4
FEATURE [App::DocumentObjectGroupPython] Ag_element002  label="Ag_element : 1"  # scripted group (container) (typed FeaturePython)
  n = 1
  ref = Ag_element
FEATURE [App::DocumentObjectGroupPython] Br_element005  label="Br_element : 003"  # scripted group (container) (typed FeaturePython)
  n = 1
  ref = Br_element
FEATURE [App::DocumentObjectGroupPython] G4_SILVER_BROMIDE  # scripted group (container) (typed FeaturePython)
  Dunit = g/cm3
  Dvalue = 6.473
  Group = -> [Ag_element002,Br_element005]
  conduct = 2
  density = 1
  expand = 3
  formula = G4_SILVER_BROMIDE
  name = G4_SILVER_BROMIDE
  specific = 4
FEATURE [App::DocumentObjectGroupPython] Ag_element003  label="Ag_element : 002"  # scripted group (container) (typed FeaturePython)
  n = 1
  ref = Ag_element
FEATURE [App::DocumentObjectGroupPython] Cl_element022  label="Cl_element : 011"  # scripted group (container) (typed FeaturePython)
  n = 1
  ref = Cl_element
FEATURE [App::DocumentObjectGroupPython] G4_SILVER_CHLORIDE  # scripted group (container) (typed FeaturePython)
  Dunit = g/cm3
  Dvalue = 5.56
  Group = -> [Ag_element003,Cl_element022]
  conduct = 2
  density = 1
  expand = 3
  formula = G4_SILVER_CHLORIDE
  name = G4_SILVER_CHLORIDE
  specific = 4
FEATURE [App::DocumentObjectGroupPython] Br_element006  label="Br_element : 0.423"  # scripted group (container) (typed FeaturePython)
  n = 0.422895
FEATURE [App::DocumentObjectGroupPython] Ag_element004  label="Ag_element : 0.574"  # scripted group (container) (typed FeaturePython)
  n = 0.573748
FEATURE [App::DocumentObjectGroupPython] I_element007  label="I_element : 0.649"  # scripted group (container) (typed FeaturePython)
  n = 0.003357
FEATURE [App::DocumentObjectGroupPython] G4_SILVER_HALIDES  # scripted group (container) (typed FeaturePython)
  Dunit = g/cm3
  Dvalue = 6.47
  Group = -> [Br_element006,Ag_element004,I_element007]
  conduct = 2
  density = 1
  expand = 3
  formula = G4_SILVER_HALIDES
  name = G4_SILVER_HALIDES
  specific = 4
FEATURE [App::DocumentObjectGroupPython] Ag_element005  label="Ag_element : 003"  # scripted group (container) (typed FeaturePython)
  n = 1
  ref = Ag_element
FEATURE [App::DocumentObjectGroupPython] I_element008  label="I_element : 004"  # scripted group (container) (typed FeaturePython)
  n = 1
  ref = I_element
FEATURE [App::DocumentObjectGroupPython] G4_SILVER_IODIDE  # scripted group (container) (typed FeaturePython)
  Dunit = g/cm3
  Dvalue = 6.01
  Group = -> [Ag_element005,I_element008]
  conduct = 2
  density = 1
  expand = 3
  formula = G4_SILVER_IODIDE
  name = G4_SILVER_IODIDE
  specific = 4
FEATURE [App::DocumentObjectGroupPython] H_element095  label="H_element : 0.100"  # scripted group (container) (typed FeaturePython)
  n = 0.1
FEATURE [App::DocumentObjectGroupPython] C_element103  label="C_element : 0.204"  # scripted group (container) (typed FeaturePython)
  n = 0.204
FEATURE [App::DocumentObjectGroupPython] N_element039  label="N_element : 0.759"  # scripted group (container) (typed FeaturePython)
  n = 0.042
FEATURE [App::DocumentObjectGroupPython] O_element088  label="O_element : 0.645"  # scripted group (container) (typed FeaturePython)
  n = 0.645
FEATURE [App::DocumentObjectGroupPython] Na_element013  label="Na_element : 0.100"  # scripted group (container) (typed FeaturePython)
  n = 0.002
FEATURE [App::DocumentObjectGroupPython] P_element009  label="P_element : 0.107"  # scripted group (container) (typed FeaturePython)
  n = 0.001
FEATURE [App::DocumentObjectGroupPython] S_element020  label="S_element : 0.021"  # scripted group (container) (typed FeaturePython)
  n = 0.002
FEATURE [App::DocumentObjectGroupPython] Cl_element023  label="Cl_element : 0.590"  # scripted group (container) (typed FeaturePython)
  n = 0.003
FEATURE [App::DocumentObjectGroupPython] K_element010  label="K_element : 0.001"  # scripted group (container) (typed FeaturePython)
  n = 0.001
FEATURE [App::DocumentObjectGroupPython] G4_SKIN_ICRP  # scripted group (container) (typed FeaturePython)
  Dunit = g/cm3
  Dvalue = 1.09
  Group = -> [H_element095,C_element103,N_element039,O_element088,Na_element013,P_element009,S_element020,Cl_element023,K_element010]
  conduct = 2
  density = 1
  expand = 3
  formula = G4_SKIN_ICRP
  name = G4_SKIN_ICRP
  specific = 4
FEATURE [App::DocumentObjectGroupPython] Na_element014  label="Na_element : 2"  # scripted group (container) (typed FeaturePython)
  n = 2
  ref = Na_element
FEATURE [App::DocumentObjectGroupPython] C_element104  label="C_element : 058"  # scripted group (container) (typed FeaturePython)
  n = 1
  ref = C_element
FEATURE [App::DocumentObjectGroupPython] O_element089  label="O_element : 049"  # scripted group (container) (typed FeaturePython)
  n = 3
  ref = O_element
FEATURE [App::DocumentObjectGroupPython] G4_SODIUM_CARBONATE  # scripted group (container) (typed FeaturePython)
  Dunit = g/cm3
  Dvalue = 2.532
  Group = -> [Na_element014,C_element104,O_element089]
  conduct = 2
  density = 1
  expand = 3
  formula = G4_SODIUM_CARBONATE
  name = G4_SODIUM_CARBONATE
  specific = 4
FEATURE [App::DocumentObjectGroupPython] Na_element015  label="Na_element : 1"  # scripted group (container) (typed FeaturePython)
  n = 1
  ref = Na_element
FEATURE [App::DocumentObjectGroupPython] I_element009  label="I_element : 005"  # scripted group (container) (typed FeaturePython)
  n = 1
  ref = I_element
FEATURE [App::DocumentObjectGroupPython] G4_SODIUM_IODIDE  # scripted group (container) (typed FeaturePython)
  Dunit = g/cm3
  Dvalue = 3.667
  Group = -> [Na_element015,I_element009]
  conduct = 2
  density = 1
  expand = 3
  formula = G4_SODIUM_IODIDE
  name = G4_SODIUM_IODIDE
  specific = 4
FEATURE [App::DocumentObjectGroupPython] Na_element016  label="Na_element : 003"  # scripted group (container) (typed FeaturePython)
  n = 2
  ref = Na_element
FEATURE [App::DocumentObjectGroupPython] O_element090  label="O_element : 050"  # scripted group (container) (typed FeaturePython)
  n = 1
  ref = O_element
FEATURE [App::DocumentObjectGroupPython] G4_SODIUM_MONOXIDE  # scripted group (container) (typed FeaturePython)
  Dunit = g/cm3
  Dvalue = 2.27
  Group = -> [Na_element016,O_element090]
  conduct = 2
  density = 1
  expand = 3
  formula = G4_SODIUM_MONOXIDE
  name = G4_SODIUM_MONOXIDE
  specific = 4
FEATURE [App::DocumentObjectGroupPython] Na_element017  label="Na_element : 004"  # scripted group (container) (typed FeaturePython)
  n = 1
  ref = Na_element
FEATURE [App::DocumentObjectGroupPython] N_element040  label="N_element : 018"  # scripted group (container) (typed FeaturePython)
  n = 1
  ref = N_element
FEATURE [App::DocumentObjectGroupPython] O_element091  label="O_element : 051"  # scripted group (container) (typed FeaturePython)
  n = 3
  ref = O_element
FEATURE [App::DocumentObjectGroupPython] G4_SODIUM_NITRATE  # scripted group (container) (typed FeaturePython)
  Dunit = g/cm3
  Dvalue = 2.261
  Group = -> [Na_element017,N_element040,O_element091]
  conduct = 2
  density = 1
  expand = 3
  formula = G4_SODIUM_NITRATE
  name = G4_SODIUM_NITRATE
  specific = 4
FEATURE [App::DocumentObjectGroupPython] C_element105  label="C_element : 059"  # scripted group (container) (typed FeaturePython)
  n = 14
  ref = C_element
FEATURE [App::DocumentObjectGroupPython] H_element096  label="H_element : 053"  # scripted group (container) (typed FeaturePython)
  n = 12
  ref = H_element
FEATURE [App::DocumentObjectGroupPython] G4_STILBENE  # scripted group (container) (typed FeaturePython)
  Dunit = g/cm3
  Dvalue = 0.9707
  Group = -> [C_element105,H_element096]
  conduct = 2
  density = 1
  expand = 3
  formula = G4_STILBENE
  name = G4_STILBENE
  specific = 4
FEATURE [App::DocumentObjectGroupPython] C_element106  label="C_element : 12"  # scripted group (container) (typed FeaturePython)
  n = 12
  ref = C_element
FEATURE [App::DocumentObjectGroupPython] H_element097  label="H_element : 22"  # scripted group (container) (typed FeaturePython)
  n = 22
  ref = H_element
FEATURE [App::DocumentObjectGroupPython] O_element092  label="O_element : 11"  # scripted group (container) (typed FeaturePython)
  n = 11
  ref = O_element
FEATURE [App::DocumentObjectGroupPython] G4_SUCROSE  # scripted group (container) (typed FeaturePython)
  Dunit = g/cm3
  Dvalue = 1.5805
  Group = -> [C_element106,H_element097,O_element092]
  conduct = 2
  density = 1
  expand = 3
  formula = G4_SUCROSE
  name = G4_SUCROSE
  specific = 4
FEATURE [App::DocumentObjectGroupPython] C_element107  label="C_element : 18"  # scripted group (container) (typed FeaturePython)
  n = 18
  ref = C_element
FEATURE [App::DocumentObjectGroupPython] H_element098  label="H_element : 054"  # scripted group (container) (typed FeaturePython)
  n = 14
  ref = H_element
FEATURE [App::DocumentObjectGroupPython] G4_TERPHENYL  # scripted group (container) (typed FeaturePython)
  Dunit = g/cm3
  Dvalue = 1.24
  Group = -> [C_element107,H_element098]
  conduct = 2
  density = 1
  expand = 3
  formula = G4_TERPHENYL
  name = G4_TERPHENYL
  specific = 4
FEATURE [App::DocumentObjectGroupPython] H_element099  label="H_element : 0.146"  # scripted group (container) (typed FeaturePython)
  n = 0.106
FEATURE [App::DocumentObjectGroupPython] C_element108  label="C_element : 0.883"  # scripted group (container) (typed FeaturePython)
  n = 0.099
FEATURE [App::DocumentObjectGroupPython] N_element041  label="N_element : 0.020"  # scripted group (container) (typed FeaturePython)
  n = 0.02
FEATURE [App::DocumentObjectGroupPython] O_element093  label="O_element : 0.766"  # scripted group (container) (typed FeaturePython)
  n = 0.766
FEATURE [App::DocumentObjectGroupPython] Na_element018  label="Na_element : 0.101"  # scripted group (container) (typed FeaturePython)
  n = 0.002
FEATURE [App::DocumentObjectGroupPython] P_element010  label="P_element : 0.108"  # scripted group (container) (typed FeaturePython)
  n = 0.001
FEATURE [App::DocumentObjectGroupPython] S_element021  label="S_element : 0.022"  # scripted group (container) (typed FeaturePython)
  n = 0.002
FEATURE [App::DocumentObjectGroupPython] Cl_element024  label="Cl_element : 0.002"  # scripted group (container) (typed FeaturePython)
  n = 0.002
FEATURE [App::DocumentObjectGroupPython] K_element011  label="K_element : 0.017"  # scripted group (container) (typed FeaturePython)
  n = 0.002
FEATURE [App::DocumentObjectGroupPython] G4_TESTIS_ICRP  # scripted group (container) (typed FeaturePython)
  Dunit = g/cm3
  Dvalue = 1.04
  Group = -> [H_element099,C_element108,N_element041,O_element093,Na_element018,P_element010,S_element021,Cl_element024,K_element011]
  conduct = 2
  density = 1
  expand = 3
  formula = G4_TESTIS_ICRP
  name = G4_TESTIS_ICRP
  specific = 4
FEATURE [App::DocumentObjectGroupPython] C_element109  label="C_element : 060"  # scripted group (container) (typed FeaturePython)
  n = 2
  ref = C_element
FEATURE [App::DocumentObjectGroupPython] Cl_element025  label="Cl_element : 012"  # scripted group (container) (typed FeaturePython)
  n = 4
  ref = Cl_element
FEATURE [App::DocumentObjectGroupPython] G4_TETRACHLOROETHYLENE  # scripted group (container) (typed FeaturePython)
  Dunit = g/cm3
  Dvalue = 1.625
  Group = -> [C_element109,Cl_element025]
  conduct = 2
  density = 1
  expand = 3
  formula = G4_TETRACHLOROETHYLENE
  name = G4_TETRACHLOROETHYLENE
  specific = 4
FEATURE [App::DocumentObjectGroupPython] Tl_element001  label="Tl_element : 1"  # scripted group (container) (typed FeaturePython)
  n = 1
  ref = Tl_element
FEATURE [App::DocumentObjectGroupPython] Cl_element026  label="Cl_element : 013"  # scripted group (container) (typed FeaturePython)
  n = 1
  ref = Cl_element
FEATURE [App::DocumentObjectGroupPython] G4_THALLIUM_CHLORIDE  # scripted group (container) (typed FeaturePython)
  Dunit = g/cm3
  Dvalue = 7.004
  Group = -> [Tl_element001,Cl_element026]
  conduct = 2
  density = 1
  expand = 3
  formula = G4_THALLIUM_CHLORIDE
  name = G4_THALLIUM_CHLORIDE
  specific = 4
FEATURE [App::DocumentObjectGroupPython] H_element100  label="H_element : 0.147"  # scripted group (container) (typed FeaturePython)
  n = 0.105
FEATURE [App::DocumentObjectGroupPython] C_element110  label="C_element : 0.256"  # scripted group (container) (typed FeaturePython)
  n = 0.256
FEATURE [App::DocumentObjectGroupPython] N_element042  label="N_element : 0.760"  # scripted group (container) (typed FeaturePython)
  n = 0.027
FEATURE [App::DocumentObjectGroupPython] O_element094  label="O_element : 0.602"  # scripted group (container) (typed FeaturePython)
  n = 0.602
FEATURE [App::DocumentObjectGroupPython] Na_element019  label="Na_element : 0.102"  # scripted group (container) (typed FeaturePython)
  n = 0.001
FEATURE [App::DocumentObjectGroupPython] P_element011  label="P_element : 0.109"  # scripted group (container) (typed FeaturePython)
  n = 0.002
FEATURE [App::DocumentObjectGroupPython] S_element022  label="S_element : 0.023"  # scripted group (container) (typed FeaturePython)
  n = 0.003
FEATURE [App::DocumentObjectGroupPython] Cl_element027  label="Cl_element : 0.591"  # scripted group (container) (typed FeaturePython)
  n = 0.002
FEATURE [App::DocumentObjectGroupPython] K_element012  label="K_element : 0.018"  # scripted group (container) (typed FeaturePython)
  n = 0.002
FEATURE [App::DocumentObjectGroupPython] G4_TISSUE_SOFT_ICRP  # scripted group (container) (typed FeaturePython)
  Dunit = g/cm3
  Dvalue = 1.03
  Group = -> [H_element100,C_element110,N_element042,O_element094,Na_element019,P_element011,S_element022,Cl_element027,K_element012]
  conduct = 2
  density = 1
  expand = 3
  formula = G4_TISSUE_SOFT_ICRP
  name = G4_TISSUE_SOFT_ICRP
  specific = 4
FEATURE [App::DocumentObjectGroupPython] H_element101  label="H_element : 0.148"  # scripted group (container) (typed FeaturePython)
  n = 0.101
FEATURE [App::DocumentObjectGroupPython] C_element111  label="C_element : 0.111"  # scripted group (container) (typed FeaturePython)
  n = 0.111
FEATURE [App::DocumentObjectGroupPython] N_element043  label="N_element : 0.026"  # scripted group (container) (typed FeaturePython)
  n = 0.026
FEATURE [App::DocumentObjectGroupPython] O_element095  label="O_element : 0.762"  # scripted group (container) (typed FeaturePython)
  n = 0.762
FEATURE [App::DocumentObjectGroupPython] G4_TISSUE_SOFT_ICRU_4  label="G4_TISSUE_SOFT_ICRU-4"  # scripted group (container) (typed FeaturePython)
  Dunit = g/cm3
  Dvalue = 1
  Group = -> [H_element101,C_element111,N_element043,O_element095]
  conduct = 2
  density = 1
  expand = 3
  formula = G4_TISSUE_SOFT_ICRU-4
  name = G4_TISSUE_SOFT_ICRU-4
  specific = 4
FEATURE [App::DocumentObjectGroupPython] H_element102  label="H_element : 0.149"  # scripted group (container) (typed FeaturePython)
  n = 0.101869
FEATURE [App::DocumentObjectGroupPython] C_element112  label="C_element : 0.456"  # scripted group (container) (typed FeaturePython)
  n = 0.456179
FEATURE [App::DocumentObjectGroupPython] N_element044  label="N_element : 0.761"  # scripted group (container) (typed FeaturePython)
  n = 0.035172
FEATURE [App::DocumentObjectGroupPython] O_element096  label="O_element : 0.407"  # scripted group (container) (typed FeaturePython)
  n = 0.40678
FEATURE [App::DocumentObjectGroupPython] G4_TISSUE_METHANE  label="G4_TISSUE-METHANE"  # scripted group (container) (typed FeaturePython)
  Dunit = g/cm3
  Dvalue = 0.00106409
  Group = -> [H_element102,C_element112,N_element044,O_element096]
  conduct = 2
  density = 1
  expand = 3
  formula = G4_TISSUE-METHANE
  name = G4_TISSUE-METHANE
  specific = 4
FEATURE [App::DocumentObjectGroupPython] H_element103  label="H_element : 0.103"  # scripted group (container) (typed FeaturePython)
  n = 0.102672
FEATURE [App::DocumentObjectGroupPython] C_element113  label="C_element : 0.569"  # scripted group (container) (typed FeaturePython)
  n = 0.56894
FEATURE [App::DocumentObjectGroupPython] N_element045  label="N_element : 0.762"  # scripted group (container) (typed FeaturePython)
  n = 0.035022
FEATURE [App::DocumentObjectGroupPython] O_element097  label="O_element : 0.293"  # scripted group (container) (typed FeaturePython)
  n = 0.293366
FEATURE [App::DocumentObjectGroupPython] G4_TISSUE_PROPANE  label="G4_TISSUE-PROPANE"  # scripted group (container) (typed FeaturePython)
  Dunit = g/cm3
  Dvalue = 0.00182628
  Group = -> [H_element103,C_element113,N_element045,O_element097]
  conduct = 2
  density = 1
  expand = 3
  formula = G4_TISSUE-PROPANE
  name = G4_TISSUE-PROPANE
  specific = 4
FEATURE [App::DocumentObjectGroupPython] Ti_element003  label="Ti_element : 1"  # scripted group (container) (typed FeaturePython)
  n = 1
  ref = Ti_element
FEATURE [App::DocumentObjectGroupPython] O_element098  label="O_element : 052"  # scripted group (container) (typed FeaturePython)
  n = 2
  ref = O_element
FEATURE [App::DocumentObjectGroupPython] G4_TITANIUM_DIOXIDE  # scripted group (container) (typed FeaturePython)
  Dunit = g/cm3
  Dvalue = 4.26
  Group = -> [Ti_element003,O_element098]
  conduct = 2
  density = 1
  expand = 3
  formula = G4_TITANIUM_DIOXIDE
  name = G4_TITANIUM_DIOXIDE
  specific = 4
FEATURE [App::DocumentObjectGroupPython] C_element114  label="C_element : 061"  # scripted group (container) (typed FeaturePython)
  n = 7
  ref = C_element
FEATURE [App::DocumentObjectGroupPython] H_element104  label="H_element : 055"  # scripted group (container) (typed FeaturePython)
  n = 8
  ref = H_element
FEATURE [App::DocumentObjectGroupPython] G4_TOLUENE  # scripted group (container) (typed FeaturePython)
  Dunit = g/cm3
  Dvalue = 0.8669
  Group = -> [C_element114,H_element104]
  conduct = 2
  density = 1
  expand = 3
  formula = G4_TOLUENE
  name = G4_TOLUENE
  specific = 4
FEATURE [App::DocumentObjectGroupPython] C_element115  label="C_element : 062"  # scripted group (container) (typed FeaturePython)
  n = 2
  ref = C_element
FEATURE [App::DocumentObjectGroupPython] H_element105  label="H_element : 056"  # scripted group (container) (typed FeaturePython)
  n = 1
  ref = H_element
FEATURE [App::DocumentObjectGroupPython] Cl_element028  label="Cl_element : 014"  # scripted group (container) (typed FeaturePython)
  n = 3
  ref = Cl_element
FEATURE [App::DocumentObjectGroupPython] G4_TRICHLOROETHYLENE  # scripted group (container) (typed FeaturePython)
  Dunit = g/cm3
  Dvalue = 1.46
  Group = -> [C_element115,H_element105,Cl_element028]
  conduct = 2
  density = 1
  expand = 3
  formula = G4_TRICHLOROETHYLENE
  name = G4_TRICHLOROETHYLENE
  specific = 4
FEATURE [App::DocumentObjectGroupPython] C_element116  label="C_element : 063"  # scripted group (container) (typed FeaturePython)
  n = 6
  ref = C_element
FEATURE [App::DocumentObjectGroupPython] H_element106  label="H_element : 15"  # scripted group (container) (typed FeaturePython)
  n = 15
  ref = H_element
FEATURE [App::DocumentObjectGroupPython] O_element099  label="O_element : 053"  # scripted group (container) (typed FeaturePython)
  n = 4
  ref = O_element
FEATURE [App::DocumentObjectGroupPython] P_element012  label="P_element : 1"  # scripted group (container) (typed FeaturePython)
  n = 1
  ref = P_element
FEATURE [App::DocumentObjectGroupPython] G4_TRIETHYL_PHOSPHATE  # scripted group (container) (typed FeaturePython)
  Dunit = g/cm3
  Dvalue = 1.07
  Group = -> [C_element116,H_element106,O_element099,P_element012]
  conduct = 2
  density = 1
  expand = 3
  formula = G4_TRIETHYL_PHOSPHATE
  name = G4_TRIETHYL_PHOSPHATE
  specific = 4
FEATURE [App::DocumentObjectGroupPython] W_element003  label="W_element : 003"  # scripted group (container) (typed FeaturePython)
  n = 1
  ref = W_element
FEATURE [App::DocumentObjectGroupPython] F_element017  label="F_element : 6"  # scripted group (container) (typed FeaturePython)
  n = 6
  ref = F_element
FEATURE [App::DocumentObjectGroupPython] G4_TUNGSTEN_HEXAFLUORIDE  # scripted group (container) (typed FeaturePython)
  Dunit = g/cm3
  Dvalue = 2.4
  Group = -> [W_element003,F_element017]
  conduct = 2
  density = 1
  expand = 3
  formula = G4_TUNGSTEN_HEXAFLUORIDE
  name = G4_TUNGSTEN_HEXAFLUORIDE
  specific = 4
FEATURE [App::DocumentObjectGroupPython] U_element001  label="U_element : 1"  # scripted group (container) (typed FeaturePython)
  n = 1
  ref = U_element
FEATURE [App::DocumentObjectGroupPython] C_element117  label="C_element : 064"  # scripted group (container) (typed FeaturePython)
  n = 2
  ref = C_element
FEATURE [App::DocumentObjectGroupPython] G4_URANIUM_DICARBIDE  # scripted group (container) (typed FeaturePython)
  Dunit = g/cm3
  Dvalue = 11.28
  Group = -> [U_element001,C_element117]
  conduct = 2
  density = 1
  expand = 3
  formula = G4_URANIUM_DICARBIDE
  name = G4_URANIUM_DICARBIDE
  specific = 4
FEATURE [App::DocumentObjectGroupPython] U_element002  label="U_element : 002"  # scripted group (container) (typed FeaturePython)
  n = 1
  ref = U_element
FEATURE [App::DocumentObjectGroupPython] C_element118  label="C_element : 065"  # scripted group (container) (typed FeaturePython)
  n = 1
  ref = C_element
FEATURE [App::DocumentObjectGroupPython] G4_URANIUM_MONOCARBIDE  # scripted group (container) (typed FeaturePython)
  Dunit = g/cm3
  Dvalue = 13.63
  Group = -> [U_element002,C_element118]
  conduct = 2
  density = 1
  expand = 3
  formula = G4_URANIUM_MONOCARBIDE
  name = G4_URANIUM_MONOCARBIDE
  specific = 4
FEATURE [App::DocumentObjectGroupPython] U_element003  label="U_element : 003"  # scripted group (container) (typed FeaturePython)
  n = 1
  ref = U_element
FEATURE [App::DocumentObjectGroupPython] O_element100  label="O_element : 054"  # scripted group (container) (typed FeaturePython)
  n = 2
  ref = O_element
FEATURE [App::DocumentObjectGroupPython] G4_URANIUM_OXIDE  # scripted group (container) (typed FeaturePython)
  Dunit = g/cm3
  Dvalue = 10.96
  Group = -> [U_element003,O_element100]
  conduct = 2
  density = 1
  expand = 3
  formula = G4_URANIUM_OXIDE
  name = G4_URANIUM_OXIDE
  specific = 4
FEATURE [App::DocumentObjectGroupPython] C_element119  label="C_element : 066"  # scripted group (container) (typed FeaturePython)
  n = 1
  ref = C_element
FEATURE [App::DocumentObjectGroupPython] H_element107  label="H_element : 057"  # scripted group (container) (typed FeaturePython)
  n = 4
  ref = H_element
FEATURE [App::DocumentObjectGroupPython] N_element046  label="N_element : 019"  # scripted group (container) (typed FeaturePython)
  n = 2
  ref = N_element
FEATURE [App::DocumentObjectGroupPython] O_element101  label="O_element : 055"  # scripted group (container) (typed FeaturePython)
  n = 1
  ref = O_element
FEATURE [App::DocumentObjectGroupPython] G4_UREA  # scripted group (container) (typed FeaturePython)
  Dunit = g/cm3
  Dvalue = 1.323
  Group = -> [C_element119,H_element107,N_element046,O_element101]
  conduct = 2
  density = 1
  expand = 3
  formula = G4_UREA
  name = G4_UREA
  specific = 4
FEATURE [App::DocumentObjectGroupPython] C_element120  label="C_element : 067"  # scripted group (container) (typed FeaturePython)
  n = 5
  ref = C_element
FEATURE [App::DocumentObjectGroupPython] H_element108  label="H_element : 058"  # scripted group (container) (typed FeaturePython)
  n = 11
  ref = H_element
FEATURE [App::DocumentObjectGroupPython] N_element047  label="N_element : 020"  # scripted group (container) (typed FeaturePython)
  n = 1
  ref = N_element
FEATURE [App::DocumentObjectGroupPython] O_element102  label="O_element : 056"  # scripted group (container) (typed FeaturePython)
  n = 2
  ref = O_element
FEATURE [App::DocumentObjectGroupPython] G4_VALINE  # scripted group (container) (typed FeaturePython)
  Dunit = g/cm3
  Dvalue = 1.23
  Group = -> [C_element120,H_element108,N_element047,O_element102]
  conduct = 2
  density = 1
  expand = 3
  formula = G4_VALINE
  name = G4_VALINE
  specific = 4
FEATURE [App::DocumentObjectGroupPython] H_element109  label="H_element : 0.009"  # scripted group (container) (typed FeaturePython)
  n = 0.009417
FEATURE [App::DocumentObjectGroupPython] C_element121  label="C_element : 0.281"  # scripted group (container) (typed FeaturePython)
  n = 0.280555
FEATURE [App::DocumentObjectGroupPython] F_element018  label="F_element : 0.710"  # scripted group (container) (typed FeaturePython)
  n = 0.710028
FEATURE [App::DocumentObjectGroupPython] G4_VITON  # scripted group (container) (typed FeaturePython)
  Dunit = g/cm3
  Dvalue = 1.8
  Group = -> [H_element109,C_element121,F_element018]
  conduct = 2
  density = 1
  expand = 3
  formula = G4_VITON
  name = G4_VITON
  specific = 4
FEATURE [App::DocumentObjectGroupPython] H_element110  label="H_element : 059"  # scripted group (container) (typed FeaturePython)
  n = 2
  ref = H_element
FEATURE [App::DocumentObjectGroupPython] O_element103  label="O_element : 057"  # scripted group (container) (typed FeaturePython)
  n = 1
  ref = O_element
FEATURE [App::DocumentObjectGroupPython] G4_WATER  # scripted group (container) (typed FeaturePython)
  Dunit = g/cm3
  Dvalue = 1
  Group = -> [H_element110,O_element103]
  conduct = 2
  density = 1
  expand = 3
  formula = G4_WATER
  name = G4_WATER
  specific = 4
FEATURE [App::DocumentObjectGroupPython] H_element111  label="H_element : 060"  # scripted group (container) (typed FeaturePython)
  n = 2
  ref = H_element
FEATURE [App::DocumentObjectGroupPython] O_element104  label="O_element : 058"  # scripted group (container) (typed FeaturePython)
  n = 1
  ref = O_element
FEATURE [App::DocumentObjectGroupPython] G4_WATER_VAPOR  # scripted group (container) (typed FeaturePython)
  Dunit = g/cm3
  Dvalue = 0.000756182
  Group = -> [H_element111,O_element104]
  conduct = 2
  density = 1
  expand = 3
  formula = G4_WATER_VAPOR
  name = G4_WATER_VAPOR
  specific = 4
FEATURE [App::DocumentObjectGroupPython] C_element122  label="C_element : 068"  # scripted group (container) (typed FeaturePython)
  n = 8
  ref = C_element
FEATURE [App::DocumentObjectGroupPython] H_element112  label="H_element : 061"  # scripted group (container) (typed FeaturePython)
  n = 10
  ref = H_element
FEATURE [App::DocumentObjectGroupPython] G4_XYLENE  # scripted group (container) (typed FeaturePython)
  Dunit = g/cm3
  Dvalue = 0.87
  Group = -> [C_element122,H_element112]
  conduct = 2
  density = 1
  expand = 3
  formula = G4_XYLENE
  name = G4_XYLENE
  specific = 4
FEATURE [App::DocumentObjectGroupPython] C_element123  label="C_element : 069"  # scripted group (container) (typed FeaturePython)
  n = 1
  ref = C_element
FEATURE [App::DocumentObjectGroupPython] G4_GRAPHITE  # scripted group (container) (typed FeaturePython)
  Dunit = g/cm3
  Dvalue = 2.21
  Group = -> [C_element123]
  conduct = 2
  density = 1
  expand = 3
  formula = G4_GRAPHITE
  name = G4_GRAPHITE
  specific = 4
FEATURE [App::DocumentObjectGroupPython] NIST  # scripted group (container) (typed FeaturePython)
  Group = -> [G4_A_150_TISSUE,G4_ACETONE,G4_ACETYLENE,G4_ADENINE,G4_ADIPOSE_TISSUE_ICRP,G4_AIR,G4_ALANINE,G4_ALUMINUM_OXIDE,G4_AMBER,G4_AMMONIA,G4_ANILINE,G4_ANTHRACENE,G4_B_100_BONE,G4_BAKELITE,G4_BARIUM_FLUORIDE,G4_BARIUM_SULFATE,G4_BENZENE,G4_BERYLLIUM_OXIDE,G4_BGO,G4_BLOOD_ICRP,G4_BONE_COMPACT_ICRU,G4_BONE_CORTICAL_ICRP,G4_BORON_CARBIDE,G4_BORON_OXIDE,G4_BRAIN_ICRP,G4_BUTANE,G4_N_BUTYL_ALCOHOL,G4_C_552,+152 more]
FEATURE [App::DocumentObjectGroupPython] H_element113  label="H_element : 062"  # scripted group (container) (typed FeaturePython)
  n = 1
  ref = H_element
FEATURE [App::DocumentObjectGroupPython] G4_H  # scripted group (container) (typed FeaturePython)
  Dunit = g/cm3
  Dvalue = 8.3748e-05
  Group = -> [H_element113]
  conduct = 2
  density = 1
  expand = 3
  formula = H
  name = G4_H
  specific = 4
FEATURE [App::DocumentObjectGroupPython] He_element001  label="He_element : 1"  # scripted group (container) (typed FeaturePython)
  n = 1
  ref = He_element
FEATURE [App::DocumentObjectGroupPython] G4_He  # scripted group (container) (typed FeaturePython)
  Dunit = g/cm3
  Dvalue = 0.000166322
  Group = -> [He_element001]
  conduct = 2
  density = 1
  expand = 3
  formula = He
  name = G4_He
  specific = 4
FEATURE [App::DocumentObjectGroupPython] Li_element008  label="Li_element : 008"  # scripted group (container) (typed FeaturePython)
  n = 1
  ref = Li_element
FEATURE [App::DocumentObjectGroupPython] G4_Li  # scripted group (container) (typed FeaturePython)
  Dunit = g/cm3
  Dvalue = 0.534
  Group = -> [Li_element008]
  conduct = 2
  density = 1
  expand = 3
  formula = Li
  name = G4_Li
  specific = 4
FEATURE [App::DocumentObjectGroupPython] Be_element002  label="Be_element : 002"  # scripted group (container) (typed FeaturePython)
  n = 1
  ref = Be_element
FEATURE [App::DocumentObjectGroupPython] G4_Be  # scripted group (container) (typed FeaturePython)
  Dunit = g/cm3
  Dvalue = 1.848
  Group = -> [Be_element002]
  conduct = 2
  density = 1
  expand = 3
  formula = Be
  name = G4_Be
  specific = 4
FEATURE [App::DocumentObjectGroupPython] B_element007  label="B_element : 007"  # scripted group (container) (typed FeaturePython)
  n = 1
  ref = B_element
FEATURE [App::DocumentObjectGroupPython] G4_B  # scripted group (container) (typed FeaturePython)
  Dunit = g/cm3
  Dvalue = 2.37
  Group = -> [B_element007]
  conduct = 2
  density = 1
  expand = 3
  formula = B
  name = G4_B
  specific = 4
FEATURE [App::DocumentObjectGroupPython] C_element124  label="C_element : 070"  # scripted group (container) (typed FeaturePython)
  n = 1
  ref = C_element
FEATURE [App::DocumentObjectGroupPython] G4_C  # scripted group (container) (typed FeaturePython)
  Dunit = g/cm3
  Dvalue = 2
  Group = -> [C_element124]
  conduct = 2
  density = 1
  expand = 3
  formula = C
  name = G4_C
  specific = 4
FEATURE [App::DocumentObjectGroupPython] N_element048  label="N_element : 021"  # scripted group (container) (typed FeaturePython)
  n = 1
  ref = N_element
FEATURE [App::DocumentObjectGroupPython] G4_N  # scripted group (container) (typed FeaturePython)
  Dunit = g/cm3
  Dvalue = 0.0011652
  Group = -> [N_element048]
  conduct = 2
  density = 1
  expand = 3
  formula = N
  name = G4_N
  specific = 4
FEATURE [App::DocumentObjectGroupPython] O_element105  label="O_element : 059"  # scripted group (container) (typed FeaturePython)
  n = 1
  ref = O_element
FEATURE [App::DocumentObjectGroupPython] G4_O  # scripted group (container) (typed FeaturePython)
  Dunit = g/cm3
  Dvalue = 0.00133151
  Group = -> [O_element105]
  conduct = 2
  density = 1
  expand = 3
  formula = O
  name = G4_O
  specific = 4
FEATURE [App::DocumentObjectGroupPython] F_element019  label="F_element : 008"  # scripted group (container) (typed FeaturePython)
  n = 1
  ref = F_element
FEATURE [App::DocumentObjectGroupPython] G4_F  # scripted group (container) (typed FeaturePython)
  Dunit = g/cm3
  Dvalue = 0.00158029
  Group = -> [F_element019]
  conduct = 2
  density = 1
  expand = 3
  formula = F
  name = G4_F
  specific = 4
FEATURE [App::DocumentObjectGroupPython] Ne_element001  label="Ne_element : 1"  # scripted group (container) (typed FeaturePython)
  n = 1
  ref = Ne_element
FEATURE [App::DocumentObjectGroupPython] G4_Ne  # scripted group (container) (typed FeaturePython)
  Dunit = g/cm3
  Dvalue = 0.000838505
  Group = -> [Ne_element001]
  conduct = 2
  density = 1
  expand = 3
  formula = Ne
  name = G4_Ne
  specific = 4
FEATURE [App::DocumentObjectGroupPython] Na_element020  label="Na_element : 005"  # scripted group (container) (typed FeaturePython)
  n = 1
  ref = Na_element
FEATURE [App::DocumentObjectGroupPython] G4_Na  # scripted group (container) (typed FeaturePython)
  Dunit = g/cm3
  Dvalue = 0.971
  Group = -> [Na_element020]
  conduct = 2
  density = 1
  expand = 3
  formula = Na
  name = G4_Na
  specific = 4
FEATURE [App::DocumentObjectGroupPython] Mg_element011  label="Mg_element : 005"  # scripted group (container) (typed FeaturePython)
  n = 1
  ref = Mg_element
FEATURE [App::DocumentObjectGroupPython] G4_Mg  # scripted group (container) (typed FeaturePython)
  Dunit = g/cm3
  Dvalue = 1.74
  Group = -> [Mg_element011]
  conduct = 2
  density = 1
  expand = 3
  formula = Mg
  name = G4_Mg
  specific = 4
FEATURE [App::DocumentObjectGroupPython] Al_element004  label="Al_element : 1"  # scripted group (container) (typed FeaturePython)
  n = 1
  ref = Al_element
FEATURE [App::DocumentObjectGroupPython] G4_Al  # scripted group (container) (typed FeaturePython)
  Dunit = g/cm3
  Dvalue = 2.699
  Group = -> [Al_element004]
  conduct = 2
  density = 1
  expand = 3
  formula = Al
  name = G4_Al
  specific = 4
FEATURE [App::DocumentObjectGroupPython] Si_element007  label="Si_element : 002"  # scripted group (container) (typed FeaturePython)
  n = 1
  ref = Si_element
FEATURE [App::DocumentObjectGroupPython] G4_Si  # scripted group (container) (typed FeaturePython)
  Dunit = g/cm3
  Dvalue = 2.33
  Group = -> [Si_element007]
  conduct = 2
  density = 1
  expand = 3
  formula = Si
  name = G4_Si
  specific = 4
FEATURE [App::DocumentObjectGroupPython] P_element013  label="P_element : 002"  # scripted group (container) (typed FeaturePython)
  n = 1
  ref = P_element
FEATURE [App::DocumentObjectGroupPython] G4_P  # scripted group (container) (typed FeaturePython)
  Dunit = g/cm3
  Dvalue = 2.2
  Group = -> [P_element013]
  conduct = 2
  density = 1
  expand = 3
  formula = P
  name = G4_P
  specific = 4
FEATURE [App::DocumentObjectGroupPython] S_element023  label="S_element : 007"  # scripted group (container) (typed FeaturePython)
  n = 1
  ref = S_element
FEATURE [App::DocumentObjectGroupPython] G4_S  # scripted group (container) (typed FeaturePython)
  Dunit = g/cm3
  Dvalue = 2
  Group = -> [S_element023]
  conduct = 2
  density = 1
  expand = 3
  formula = S
  name = G4_S
  specific = 4
FEATURE [App::DocumentObjectGroupPython] Cl_element029  label="Cl_element : 015"  # scripted group (container) (typed FeaturePython)
  n = 1
  ref = Cl_element
FEATURE [App::DocumentObjectGroupPython] G4_Cl  # scripted group (container) (typed FeaturePython)
  Dunit = g/cm3
  Dvalue = 0.00299473
  Group = -> [Cl_element029]
  conduct = 2
  density = 1
  expand = 3
  formula = Cl
  name = G4_Cl
  specific = 4
FEATURE [App::DocumentObjectGroupPython] Ar_element002  label="Ar_element : 1"  # scripted group (container) (typed FeaturePython)
  n = 1
  ref = Ar_element
FEATURE [App::DocumentObjectGroupPython] G4_Ar  # scripted group (container) (typed FeaturePython)
  Dunit = g/cm3
  Dvalue = 0.00166201
  Group = -> [Ar_element002]
  conduct = 2
  density = 1
  expand = 3
  formula = Ar
  name = G4_Ar
  specific = 4
FEATURE [App::DocumentObjectGroupPython] K_element013  label="K_element : 003"  # scripted group (container) (typed FeaturePython)
  n = 1
  ref = K_element
FEATURE [App::DocumentObjectGroupPython] G4_K  # scripted group (container) (typed FeaturePython)
  Dunit = g/cm3
  Dvalue = 0.862
  Group = -> [K_element013]
  conduct = 2
  density = 1
  expand = 3
  formula = K
  name = G4_K
  specific = 4
FEATURE [App::DocumentObjectGroupPython] Ca_element014  label="Ca_element : 007"  # scripted group (container) (typed FeaturePython)
  n = 1
  ref = Ca_element
FEATURE [App::DocumentObjectGroupPython] G4_Ca  # scripted group (container) (typed FeaturePython)
  Dunit = g/cm3
  Dvalue = 1.55
  Group = -> [Ca_element014]
  conduct = 2
  density = 1
  expand = 3
  formula = Ca
  name = G4_Ca
  specific = 4
FEATURE [App::DocumentObjectGroupPython] Sc_element001  label="Sc_element : 1"  # scripted group (container) (typed FeaturePython)
  n = 1
  ref = Sc_element
FEATURE [App::DocumentObjectGroupPython] G4_Sc  # scripted group (container) (typed FeaturePython)
  Dunit = g/cm3
  Dvalue = 2.989
  Group = -> [Sc_element001]
  conduct = 2
  density = 1
  expand = 3
  formula = Sc
  name = G4_Sc
  specific = 4
FEATURE [App::DocumentObjectGroupPython] Ti_element004  label="Ti_element : 002"  # scripted group (container) (typed FeaturePython)
  n = 1
  ref = Ti_element
FEATURE [App::DocumentObjectGroupPython] G4_Ti  # scripted group (container) (typed FeaturePython)
  Dunit = g/cm3
  Dvalue = 4.54
  Group = -> [Ti_element004]
  conduct = 2
  density = 1
  expand = 3
  formula = Ti
  name = G4_Ti
  specific = 4
FEATURE [App::DocumentObjectGroupPython] V_element001  label="V_element : 1"  # scripted group (container) (typed FeaturePython)
  n = 1
  ref = V_element
FEATURE [App::DocumentObjectGroupPython] G4_V  # scripted group (container) (typed FeaturePython)
  Dunit = g/cm3
  Dvalue = 6.11
  Group = -> [V_element001]
  conduct = 2
  density = 1
  expand = 3
  formula = V
  name = G4_V
  specific = 4
FEATURE [App::DocumentObjectGroupPython] Cr_element001  label="Cr_element : 1"  # scripted group (container) (typed FeaturePython)
  n = 1
  ref = Cr_element
FEATURE [App::DocumentObjectGroupPython] G4_Cr  # scripted group (container) (typed FeaturePython)
  Dunit = g/cm3
  Dvalue = 7.18
  Group = -> [Cr_element001]
  conduct = 2
  density = 1
  expand = 3
  formula = Cr
  name = G4_Cr
  specific = 4
FEATURE [App::DocumentObjectGroupPython] Mn_element001  label="Mn_element : 1"  # scripted group (container) (typed FeaturePython)
  n = 1
  ref = Mn_element
FEATURE [App::DocumentObjectGroupPython] G4_Mn  # scripted group (container) (typed FeaturePython)
  Dunit = g/cm3
  Dvalue = 7.44
  Group = -> [Mn_element001]
  conduct = 2
  density = 1
  expand = 3
  formula = Mn
  name = G4_Mn
  specific = 4
FEATURE [App::DocumentObjectGroupPython] Fe_element007  label="Fe_element : 004"  # scripted group (container) (typed FeaturePython)
  n = 1
  ref = Fe_element
FEATURE [App::DocumentObjectGroupPython] G4_Fe  # scripted group (container) (typed FeaturePython)
  Dunit = g/cm3
  Dvalue = 7.874
  Group = -> [Fe_element007]
  conduct = 2
  density = 1
  expand = 3
  formula = Fe
  name = G4_Fe
  specific = 4
FEATURE [App::DocumentObjectGroupPython] Co_element001  label="Co_element : 1"  # scripted group (container) (typed FeaturePython)
  n = 1
  ref = Co_element
FEATURE [App::DocumentObjectGroupPython] G4_Co  # scripted group (container) (typed FeaturePython)
  Dunit = g/cm3
  Dvalue = 8.9
  Group = -> [Co_element001]
  conduct = 2
  density = 1
  expand = 3
  formula = Co
  name = G4_Co
  specific = 4
FEATURE [App::DocumentObjectGroupPython] Ni_element001  label="Ni_element : 1"  # scripted group (container) (typed FeaturePython)
  n = 1
  ref = Ni_element
FEATURE [App::DocumentObjectGroupPython] G4_Ni  # scripted group (container) (typed FeaturePython)
  Dunit = g/cm3
  Dvalue = 8.902
  Group = -> [Ni_element001]
  conduct = 2
  density = 1
  expand = 3
  formula = Ni
  name = G4_Ni
  specific = 4
FEATURE [App::DocumentObjectGroupPython] Cu_element001  label="Cu_element : 1"  # scripted group (container) (typed FeaturePython)
  n = 1
  ref = Cu_element
FEATURE [App::DocumentObjectGroupPython] G4_Cu  # scripted group (container) (typed FeaturePython)
  Dunit = g/cm3
  Dvalue = 8.96
  Group = -> [Cu_element001]
  conduct = 2
  density = 1
  expand = 3
  formula = Cu
  name = G4_Cu
  specific = 4
FEATURE [App::DocumentObjectGroupPython] Zn_element001  label="Zn_element : 1"  # scripted group (container) (typed FeaturePython)
  n = 1
  ref = Zn_element
FEATURE [App::DocumentObjectGroupPython] G4_Zn  # scripted group (container) (typed FeaturePython)
  Dunit = g/cm3
  Dvalue = 7.133
  Group = -> [Zn_element001]
  conduct = 2
  density = 1
  expand = 3
  formula = Zn
  name = G4_Zn
  specific = 4
FEATURE [App::DocumentObjectGroupPython] Ga_element002  label="Ga_element : 002"  # scripted group (container) (typed FeaturePython)
  n = 1
  ref = Ga_element
FEATURE [App::DocumentObjectGroupPython] G4_Ga  # scripted group (container) (typed FeaturePython)
  Dunit = g/cm3
  Dvalue = 5.904
  Group = -> [Ga_element002]
  conduct = 2
  density = 1
  expand = 3
  formula = Ga
  name = G4_Ga
  specific = 4
FEATURE [App::DocumentObjectGroupPython] Ge_element002  label="Ge_element : 1"  # scripted group (container) (typed FeaturePython)
  n = 1
  ref = Ge_element
FEATURE [App::DocumentObjectGroupPython] G4_Ge  # scripted group (container) (typed FeaturePython)
  Dunit = g/cm3
  Dvalue = 5.323
  Group = -> [Ge_element002]
  conduct = 2
  density = 1
  expand = 3
  formula = Ge
  name = G4_Ge
  specific = 4
FEATURE [App::DocumentObjectGroupPython] As_element003  label="As_element : 002"  # scripted group (container) (typed FeaturePython)
  n = 1
  ref = As_element
FEATURE [App::DocumentObjectGroupPython] G4_As  # scripted group (container) (typed FeaturePython)
  Dunit = g/cm3
  Dvalue = 5.73
  Group = -> [As_element003]
  conduct = 2
  density = 1
  expand = 3
  formula = As
  name = G4_As
  specific = 4
FEATURE [App::DocumentObjectGroupPython] Se_element001  label="Se_element : 1"  # scripted group (container) (typed FeaturePython)
  n = 1
  ref = Se_element
FEATURE [App::DocumentObjectGroupPython] G4_Se  # scripted group (container) (typed FeaturePython)
  Dunit = g/cm3
  Dvalue = 4.5
  Group = -> [Se_element001]
  conduct = 2
  density = 1
  expand = 3
  formula = Se
  name = G4_Se
  specific = 4
FEATURE [App::DocumentObjectGroupPython] Br_element007  label="Br_element : 004"  # scripted group (container) (typed FeaturePython)
  n = 1
  ref = Br_element
FEATURE [App::DocumentObjectGroupPython] G4_Br  # scripted group (container) (typed FeaturePython)
  Dunit = g/cm3
  Dvalue = 0.0070721
  Group = -> [Br_element007]
  conduct = 2
  density = 1
  expand = 3
  formula = Br
  name = G4_Br
  specific = 4
FEATURE [App::DocumentObjectGroupPython] Kr_element001  label="Kr_element : 1"  # scripted group (container) (typed FeaturePython)
  n = 1
  ref = Kr_element
FEATURE [App::DocumentObjectGroupPython] G4_Kr  # scripted group (container) (typed FeaturePython)
  Dunit = g/cm3
  Dvalue = 0.00347832
  Group = -> [Kr_element001]
  conduct = 2
  density = 1
  expand = 3
  formula = Kr
  name = G4_Kr
  specific = 4
FEATURE [App::DocumentObjectGroupPython] Rb_element001  label="Rb_element : 1"  # scripted group (container) (typed FeaturePython)
  n = 1
  ref = Rb_element
FEATURE [App::DocumentObjectGroupPython] G4_Rb  # scripted group (container) (typed FeaturePython)
  Dunit = g/cm3
  Dvalue = 1.532
  Group = -> [Rb_element001]
  conduct = 2
  density = 1
  expand = 3
  formula = Rb
  name = G4_Rb
  specific = 4
FEATURE [App::DocumentObjectGroupPython] Sr_element001  label="Sr_element : 1"  # scripted group (container) (typed FeaturePython)
  n = 1
  ref = Sr_element
FEATURE [App::DocumentObjectGroupPython] G4_Sr  # scripted group (container) (typed FeaturePython)
  Dunit = g/cm3
  Dvalue = 2.54
  Group = -> [Sr_element001]
  conduct = 2
  density = 1
  expand = 3
  formula = Sr
  name = G4_Sr
  specific = 4
FEATURE [App::DocumentObjectGroupPython] Y_element001  label="Y_element : 1"  # scripted group (container) (typed FeaturePython)
  n = 1
  ref = Y_element
FEATURE [App::DocumentObjectGroupPython] G4_Y  # scripted group (container) (typed FeaturePython)
  Dunit = g/cm3
  Dvalue = 4.469
  Group = -> [Y_element001]
  conduct = 2
  density = 1
  expand = 3
  formula = Y
  name = G4_Y
  specific = 4
FEATURE [App::DocumentObjectGroupPython] Zr_element001  label="Zr_element : 1"  # scripted group (container) (typed FeaturePython)
  n = 1
  ref = Zr_element
FEATURE [App::DocumentObjectGroupPython] G4_Zr  # scripted group (container) (typed FeaturePython)
  Dunit = g/cm3
  Dvalue = 6.506
  Group = -> [Zr_element001]
  conduct = 2
  density = 1
  expand = 3
  formula = Zr
  name = G4_Zr
  specific = 4
FEATURE [App::DocumentObjectGroupPython] Nb_element001  label="Nb_element : 1"  # scripted group (container) (typed FeaturePython)
  n = 1
  ref = Nb_element
FEATURE [App::DocumentObjectGroupPython] G4_Nb  # scripted group (container) (typed FeaturePython)
  Dunit = g/cm3
  Dvalue = 8.57
  Group = -> [Nb_element001]
  conduct = 2
  density = 1
  expand = 3
  formula = Nb
  name = G4_Nb
  specific = 4
FEATURE [App::DocumentObjectGroupPython] Mo_element001  label="Mo_element : 1"  # scripted group (container) (typed FeaturePython)
  n = 1
  ref = Mo_element
FEATURE [App::DocumentObjectGroupPython] G4_Mo  # scripted group (container) (typed FeaturePython)
  Dunit = g/cm3
  Dvalue = 10.22
  Group = -> [Mo_element001]
  conduct = 2
  density = 1
  expand = 3
  formula = Mo
  name = G4_Mo
  specific = 4
FEATURE [App::DocumentObjectGroupPython] Tc_element001  label="Tc_element : 1"  # scripted group (container) (typed FeaturePython)
  n = 1
  ref = Tc_element
FEATURE [App::DocumentObjectGroupPython] G4_Tc  # scripted group (container) (typed FeaturePython)
  Dunit = g/cm3
  Dvalue = 11.5
  Group = -> [Tc_element001]
  conduct = 2
  density = 1
  expand = 3
  formula = Tc
  name = G4_Tc
  specific = 4
FEATURE [App::DocumentObjectGroupPython] Ru_element001  label="Ru_element : 1"  # scripted group (container) (typed FeaturePython)
  n = 1
  ref = Ru_element
FEATURE [App::DocumentObjectGroupPython] G4_Ru  # scripted group (container) (typed FeaturePython)
  Dunit = g/cm3
  Dvalue = 12.41
  Group = -> [Ru_element001]
  conduct = 2
  density = 1
  expand = 3
  formula = Ru
  name = G4_Ru
  specific = 4
FEATURE [App::DocumentObjectGroupPython] Rh_element001  label="Rh_element : 1"  # scripted group (container) (typed FeaturePython)
  n = 1
  ref = Rh_element
FEATURE [App::DocumentObjectGroupPython] G4_Rh  # scripted group (container) (typed FeaturePython)
  Dunit = g/cm3
  Dvalue = 12.41
  Group = -> [Rh_element001]
  conduct = 2
  density = 1
  expand = 3
  formula = Rh
  name = G4_Rh
  specific = 4
FEATURE [App::DocumentObjectGroupPython] Pd_element001  label="Pd_element : 1"  # scripted group (container) (typed FeaturePython)
  n = 1
  ref = Pd_element
FEATURE [App::DocumentObjectGroupPython] G4_Pd  # scripted group (container) (typed FeaturePython)
  Dunit = g/cm3
  Dvalue = 12.02
  Group = -> [Pd_element001]
  conduct = 2
  density = 1
  expand = 3
  formula = Pd
  name = G4_Pd
  specific = 4
FEATURE [App::DocumentObjectGroupPython] Ag_element006  label="Ag_element : 004"  # scripted group (container) (typed FeaturePython)
  n = 1
  ref = Ag_element
FEATURE [App::DocumentObjectGroupPython] G4_Ag  # scripted group (container) (typed FeaturePython)
  Dunit = g/cm3
  Dvalue = 10.5
  Group = -> [Ag_element006]
  conduct = 2
  density = 1
  expand = 3
  formula = Ag
  name = G4_Ag
  specific = 4
FEATURE [App::DocumentObjectGroupPython] Cd_element003  label="Cd_element : 003"  # scripted group (container) (typed FeaturePython)
  n = 1
  ref = Cd_element
FEATURE [App::DocumentObjectGroupPython] G4_Cd  # scripted group (container) (typed FeaturePython)
  Dunit = g/cm3
  Dvalue = 8.65
  Group = -> [Cd_element003]
  conduct = 2
  density = 1
  expand = 3
  formula = Cd
  name = G4_Cd
  specific = 4
FEATURE [App::DocumentObjectGroupPython] In_element001  label="In_element : 1"  # scripted group (container) (typed FeaturePython)
  n = 1
  ref = In_element
FEATURE [App::DocumentObjectGroupPython] G4_In  # scripted group (container) (typed FeaturePython)
  Dunit = g/cm3
  Dvalue = 7.31
  Group = -> [In_element001]
  conduct = 2
  density = 1
  expand = 3
  formula = In
  name = G4_In
  specific = 4
FEATURE [App::DocumentObjectGroupPython] Sn_element001  label="Sn_element : 1"  # scripted group (container) (typed FeaturePython)
  n = 1
  ref = Sn_element
FEATURE [App::DocumentObjectGroupPython] G4_Sn  # scripted group (container) (typed FeaturePython)
  Dunit = g/cm3
  Dvalue = 7.31
  Group = -> [Sn_element001]
  conduct = 2
  density = 1
  expand = 3
  formula = Sn
  name = G4_Sn
  specific = 4
FEATURE [App::DocumentObjectGroupPython] Sb_element001  label="Sb_element : 1"  # scripted group (container) (typed FeaturePython)
  n = 1
  ref = Sb_element
FEATURE [App::DocumentObjectGroupPython] G4_Sb  # scripted group (container) (typed FeaturePython)
  Dunit = g/cm3
  Dvalue = 6.691
  Group = -> [Sb_element001]
  conduct = 2
  density = 1
  expand = 3
  formula = Sb
  name = G4_Sb
  specific = 4
FEATURE [App::DocumentObjectGroupPython] Te_element002  label="Te_element : 002"  # scripted group (container) (typed FeaturePython)
  n = 1
  ref = Te_element
FEATURE [App::DocumentObjectGroupPython] G4_Te  # scripted group (container) (typed FeaturePython)
  Dunit = g/cm3
  Dvalue = 6.24
  Group = -> [Te_element002]
  conduct = 2
  density = 1
  expand = 3
  formula = Te
  name = G4_Te
  specific = 4
FEATURE [App::DocumentObjectGroupPython] I_element010  label="I_element : 006"  # scripted group (container) (typed FeaturePython)
  n = 1
  ref = I_element
FEATURE [App::DocumentObjectGroupPython] G4_I  # scripted group (container) (typed FeaturePython)
  Dunit = g/cm3
  Dvalue = 4.93
  Group = -> [I_element010]
  conduct = 2
  density = 1
  expand = 3
  formula = I
  name = G4_I
  specific = 4
FEATURE [App::DocumentObjectGroupPython] Xe_element001  label="Xe_element : 1"  # scripted group (container) (typed FeaturePython)
  n = 1
  ref = Xe_element
FEATURE [App::DocumentObjectGroupPython] G4_Xe  # scripted group (container) (typed FeaturePython)
  Dunit = g/cm3
  Dvalue = 0.00548536
  Group = -> [Xe_element001]
  conduct = 2
  density = 1
  expand = 3
  formula = Xe
  name = G4_Xe
  specific = 4
FEATURE [App::DocumentObjectGroupPython] Cs_element003  label="Cs_element : 003"  # scripted group (container) (typed FeaturePython)
  n = 1
  ref = Cs_element
FEATURE [App::DocumentObjectGroupPython] G4_Cs  # scripted group (container) (typed FeaturePython)
  Dunit = g/cm3
  Dvalue = 1.873
  Group = -> [Cs_element003]
  conduct = 2
  density = 1
  expand = 3
  formula = Cs
  name = G4_Cs
  specific = 4
FEATURE [App::DocumentObjectGroupPython] Ba_element003  label="Ba_element : 003"  # scripted group (container) (typed FeaturePython)
  n = 1
  ref = Ba_element
FEATURE [App::DocumentObjectGroupPython] G4_Ba  # scripted group (container) (typed FeaturePython)
  Dunit = g/cm3
  Dvalue = 3.5
  Group = -> [Ba_element003]
  conduct = 2
  density = 1
  expand = 3
  formula = Ba
  name = G4_Ba
  specific = 4
FEATURE [App::DocumentObjectGroupPython] La_element003  label="La_element : 003"  # scripted group (container) (typed FeaturePython)
  n = 1
  ref = La_element
FEATURE [App::DocumentObjectGroupPython] G4_La  # scripted group (container) (typed FeaturePython)
  Dunit = g/cm3
  Dvalue = 6.154
  Group = -> [La_element003]
  conduct = 2
  density = 1
  expand = 3
  formula = La
  name = G4_La
  specific = 4
FEATURE [App::DocumentObjectGroupPython] Ce_element002  label="Ce_element : 1"  # scripted group (container) (typed FeaturePython)
  n = 1
  ref = Ce_element
FEATURE [App::DocumentObjectGroupPython] G4_Ce  # scripted group (container) (typed FeaturePython)
  Dunit = g/cm3
  Dvalue = 6.657
  Group = -> [Ce_element002]
  conduct = 2
  density = 1
  expand = 3
  formula = Ce
  name = G4_Ce
  specific = 4
FEATURE [App::DocumentObjectGroupPython] Pr_element001  label="Pr_element : 1"  # scripted group (container) (typed FeaturePython)
  n = 1
  ref = Pr_element
FEATURE [App::DocumentObjectGroupPython] G4_Pr  # scripted group (container) (typed FeaturePython)
  Dunit = g/cm3
  Dvalue = 6.71
  Group = -> [Pr_element001]
  conduct = 2
  density = 1
  expand = 3
  formula = Pr
  name = G4_Pr
  specific = 4
FEATURE [App::DocumentObjectGroupPython] Nd_element001  label="Nd_element : 1"  # scripted group (container) (typed FeaturePython)
  n = 1
  ref = Nd_element
FEATURE [App::DocumentObjectGroupPython] G4_Nd  # scripted group (container) (typed FeaturePython)
  Dunit = g/cm3
  Dvalue = 6.9
  Group = -> [Nd_element001]
  conduct = 2
  density = 1
  expand = 3
  formula = Nd
  name = G4_Nd
  specific = 4
FEATURE [App::DocumentObjectGroupPython] Pm_element001  label="Pm_element : 1"  # scripted group (container) (typed FeaturePython)
  n = 1
  ref = Pm_element
FEATURE [App::DocumentObjectGroupPython] G4_Pm  # scripted group (container) (typed FeaturePython)
  Dunit = g/cm3
  Dvalue = 7.22
  Group = -> [Pm_element001]
  conduct = 2
  density = 1
  expand = 3
  formula = Pm
  name = G4_Pm
  specific = 4
FEATURE [App::DocumentObjectGroupPython] Sm_element001  label="Sm_element : 1"  # scripted group (container) (typed FeaturePython)
  n = 1
  ref = Sm_element
FEATURE [App::DocumentObjectGroupPython] G4_Sm  # scripted group (container) (typed FeaturePython)
  Dunit = g/cm3
  Dvalue = 7.46
  Group = -> [Sm_element001]
  conduct = 2
  density = 1
  expand = 3
  formula = Sm
  name = G4_Sm
  specific = 4
FEATURE [App::DocumentObjectGroupPython] Eu_element001  label="Eu_element : 1"  # scripted group (container) (typed FeaturePython)
  n = 1
  ref = Eu_element
FEATURE [App::DocumentObjectGroupPython] G4_Eu  # scripted group (container) (typed FeaturePython)
  Dunit = g/cm3
  Dvalue = 5.243
  Group = -> [Eu_element001]
  conduct = 2
  density = 1
  expand = 3
  formula = Eu
  name = G4_Eu
  specific = 4
FEATURE [App::DocumentObjectGroupPython] Gd_element002  label="Gd_element : 1"  # scripted group (container) (typed FeaturePython)
  n = 1
  ref = Gd_element
FEATURE [App::DocumentObjectGroupPython] G4_Gd  # scripted group (container) (typed FeaturePython)
  Dunit = g/cm3
  Dvalue = 7.9004
  Group = -> [Gd_element002]
  conduct = 2
  density = 1
  expand = 3
  formula = Gd
  name = G4_Gd
  specific = 4
FEATURE [App::DocumentObjectGroupPython] Tb_element001  label="Tb_element : 1"  # scripted group (container) (typed FeaturePython)
  n = 1
  ref = Tb_element
FEATURE [App::DocumentObjectGroupPython] G4_Tb  # scripted group (container) (typed FeaturePython)
  Dunit = g/cm3
  Dvalue = 8.229
  Group = -> [Tb_element001]
  conduct = 2
  density = 1
  expand = 3
  formula = Tb
  name = G4_Tb
  specific = 4
FEATURE [App::DocumentObjectGroupPython] Dy_element001  label="Dy_element : 1"  # scripted group (container) (typed FeaturePython)
  n = 1
  ref = Dy_element
FEATURE [App::DocumentObjectGroupPython] G4_Dy  # scripted group (container) (typed FeaturePython)
  Dunit = g/cm3
  Dvalue = 8.55
  Group = -> [Dy_element001]
  conduct = 2
  density = 1
  expand = 3
  formula = Dy
  name = G4_Dy
  specific = 4
FEATURE [App::DocumentObjectGroupPython] Ho_element001  label="Ho_element : 1"  # scripted group (container) (typed FeaturePython)
  n = 1
  ref = Ho_element
FEATURE [App::DocumentObjectGroupPython] G4_Ho  # scripted group (container) (typed FeaturePython)
  Dunit = g/cm3
  Dvalue = 8.795
  Group = -> [Ho_element001]
  conduct = 2
  density = 1
  expand = 3
  formula = Ho
  name = G4_Ho
  specific = 4
FEATURE [App::DocumentObjectGroupPython] Er_element001  label="Er_element : 1"  # scripted group (container) (typed FeaturePython)
  n = 1
  ref = Er_element
FEATURE [App::DocumentObjectGroupPython] G4_Er  # scripted group (container) (typed FeaturePython)
  Dunit = g/cm3
  Dvalue = 9.066
  Group = -> [Er_element001]
  conduct = 2
  density = 1
  expand = 3
  formula = Er
  name = G4_Er
  specific = 4
FEATURE [App::DocumentObjectGroupPython] Tm_element001  label="Tm_element : 1"  # scripted group (container) (typed FeaturePython)
  n = 1
  ref = Tm_element
FEATURE [App::DocumentObjectGroupPython] G4_Tm  # scripted group (container) (typed FeaturePython)
  Dunit = g/cm3
  Dvalue = 9.321
  Group = -> [Tm_element001]
  conduct = 2
  density = 1
  expand = 3
  formula = Tm
  name = G4_Tm
  specific = 4
FEATURE [App::DocumentObjectGroupPython] Yb_element001  label="Yb_element : 1"  # scripted group (container) (typed FeaturePython)
  n = 1
  ref = Yb_element
FEATURE [App::DocumentObjectGroupPython] G4_Yb  # scripted group (container) (typed FeaturePython)
  Dunit = g/cm3
  Dvalue = 6.73
  Group = -> [Yb_element001]
  conduct = 2
  density = 1
  expand = 3
  formula = Yb
  name = G4_Yb
  specific = 4
FEATURE [App::DocumentObjectGroupPython] Lu_element001  label="Lu_element : 1"  # scripted group (container) (typed FeaturePython)
  n = 1
  ref = Lu_element
FEATURE [App::DocumentObjectGroupPython] G4_Lu  # scripted group (container) (typed FeaturePython)
  Dunit = g/cm3
  Dvalue = 9.84
  Group = -> [Lu_element001]
  conduct = 2
  density = 1
  expand = 3
  formula = Lu
  name = G4_Lu
  specific = 4
FEATURE [App::DocumentObjectGroupPython] Hf_element001  label="Hf_element : 1"  # scripted group (container) (typed FeaturePython)
  n = 1
  ref = Hf_element
FEATURE [App::DocumentObjectGroupPython] G4_Hf  # scripted group (container) (typed FeaturePython)
  Dunit = g/cm3
  Dvalue = 13.31
  Group = -> [Hf_element001]
  conduct = 2
  density = 1
  expand = 3
  formula = Hf
  name = G4_Hf
  specific = 4
FEATURE [App::DocumentObjectGroupPython] Ta_element001  label="Ta_element : 1"  # scripted group (container) (typed FeaturePython)
  n = 1
  ref = Ta_element
FEATURE [App::DocumentObjectGroupPython] G4_Ta  # scripted group (container) (typed FeaturePython)
  Dunit = g/cm3
  Dvalue = 16.654
  Group = -> [Ta_element001]
  conduct = 2
  density = 1
  expand = 3
  formula = Ta
  name = G4_Ta
  specific = 4
FEATURE [App::DocumentObjectGroupPython] W_element004  label="W_element : 004"  # scripted group (container) (typed FeaturePython)
  n = 1
  ref = W_element
FEATURE [App::DocumentObjectGroupPython] G4_W  # scripted group (container) (typed FeaturePython)
  Dunit = g/cm3
  Dvalue = 19.3
  Group = -> [W_element004]
  conduct = 2
  density = 1
  expand = 3
  formula = W
  name = G4_W
  specific = 4
FEATURE [App::DocumentObjectGroupPython] Re_element001  label="Re_element : 1"  # scripted group (container) (typed FeaturePython)
  n = 1
  ref = Re_element
FEATURE [App::DocumentObjectGroupPython] G4_Re  # scripted group (container) (typed FeaturePython)
  Dunit = g/cm3
  Dvalue = 21.02
  Group = -> [Re_element001]
  conduct = 2
  density = 1
  expand = 3
  formula = Re
  name = G4_Re
  specific = 4
FEATURE [App::DocumentObjectGroupPython] Os_element001  label="Os_element : 1"  # scripted group (container) (typed FeaturePython)
  n = 1
  ref = Os_element
FEATURE [App::DocumentObjectGroupPython] G4_Os  # scripted group (container) (typed FeaturePython)
  Dunit = g/cm3
  Dvalue = 22.57
  Group = -> [Os_element001]
  conduct = 2
  density = 1
  expand = 3
  formula = Os
  name = G4_Os
  specific = 4
FEATURE [App::DocumentObjectGroupPython] Ir_element001  label="Ir_element : 1"  # scripted group (container) (typed FeaturePython)
  n = 1
  ref = Ir_element
FEATURE [App::DocumentObjectGroupPython] G4_Ir  # scripted group (container) (typed FeaturePython)
  Dunit = g/cm3
  Dvalue = 22.42
  Group = -> [Ir_element001]
  conduct = 2
  density = 1
  expand = 3
  formula = Ir
  name = G4_Ir
  specific = 4
FEATURE [App::DocumentObjectGroupPython] Pt_element001  label="Pt_element : 1"  # scripted group (container) (typed FeaturePython)
  n = 1
  ref = Pt_element
FEATURE [App::DocumentObjectGroupPython] G4_Pt  # scripted group (container) (typed FeaturePython)
  Dunit = g/cm3
  Dvalue = 21.45
  Group = -> [Pt_element001]
  conduct = 2
  density = 1
  expand = 3
  formula = Pt
  name = G4_Pt
  specific = 4
FEATURE [App::DocumentObjectGroupPython] Au_element001  label="Au_element : 1"  # scripted group (container) (typed FeaturePython)
  n = 1
  ref = Au_element
FEATURE [App::DocumentObjectGroupPython] G4_Au  # scripted group (container) (typed FeaturePython)
  Dunit = g/cm3
  Dvalue = 19.32
  Group = -> [Au_element001]
  conduct = 2
  density = 1
  expand = 3
  formula = Au
  name = G4_Au
  specific = 4
FEATURE [App::DocumentObjectGroupPython] Hg_element002  label="Hg_element : 002"  # scripted group (container) (typed FeaturePython)
  n = 1
  ref = Hg_element
FEATURE [App::DocumentObjectGroupPython] G4_Hg  # scripted group (container) (typed FeaturePython)
  Dunit = g/cm3
  Dvalue = 13.546
  Group = -> [Hg_element002]
  conduct = 2
  density = 1
  expand = 3
  formula = Hg
  name = G4_Hg
  specific = 4
FEATURE [App::DocumentObjectGroupPython] Tl_element002  label="Tl_element : 002"  # scripted group (container) (typed FeaturePython)
  n = 1
  ref = Tl_element
FEATURE [App::DocumentObjectGroupPython] G4_Tl  # scripted group (container) (typed FeaturePython)
  Dunit = g/cm3
  Dvalue = 11.72
  Group = -> [Tl_element002]
  conduct = 2
  density = 1
  expand = 3
  formula = Tl
  name = G4_Tl
  specific = 4
FEATURE [App::DocumentObjectGroupPython] Pb_element003  label="Pb_element : 1"  # scripted group (container) (typed FeaturePython)
  n = 1
  ref = Pb_element
FEATURE [App::DocumentObjectGroupPython] G4_Pb  # scripted group (container) (typed FeaturePython)
  Dunit = g/cm3
  Dvalue = 11.35
  Group = -> [Pb_element003]
  conduct = 2
  density = 1
  expand = 3
  formula = Pb
  name = G4_Pb
  specific = 4
FEATURE [App::DocumentObjectGroupPython] Bi_element002  label="Bi_element : 1"  # scripted group (container) (typed FeaturePython)
  n = 1
  ref = Bi_element
FEATURE [App::DocumentObjectGroupPython] G4_Bi  # scripted group (container) (typed FeaturePython)
  Dunit = g/cm3
  Dvalue = 9.747
  Group = -> [Bi_element002]
  conduct = 2
  density = 1
  expand = 3
  formula = Bi
  name = G4_Bi
  specific = 4
FEATURE [App::DocumentObjectGroupPython] Po_element001  label="Po_element : 1"  # scripted group (container) (typed FeaturePython)
  n = 1
  ref = Po_element
FEATURE [App::DocumentObjectGroupPython] G4_Po  # scripted group (container) (typed FeaturePython)
  Dunit = g/cm3
  Dvalue = 9.32
  Group = -> [Po_element001]
  conduct = 2
  density = 1
  expand = 3
  formula = Po
  name = G4_Po
  specific = 4
FEATURE [App::DocumentObjectGroupPython] At_element001  label="At_element : 1"  # scripted group (container) (typed FeaturePython)
  n = 1
  ref = At_element
FEATURE [App::DocumentObjectGroupPython] G4_At  # scripted group (container) (typed FeaturePython)
  Dunit = g/cm3
  Dvalue = 9.32
  Group = -> [At_element001]
  conduct = 2
  density = 1
  expand = 3
  formula = At
  name = G4_At
  specific = 4
FEATURE [App::DocumentObjectGroupPython] Rn_element001  label="Rn_element : 1"  # scripted group (container) (typed FeaturePython)
  n = 1
  ref = Rn_element
FEATURE [App::DocumentObjectGroupPython] G4_Rn  # scripted group (container) (typed FeaturePython)
  Dunit = g/cm3
  Dvalue = 0.00900662
  Group = -> [Rn_element001]
  conduct = 2
  density = 1
  expand = 3
  formula = Rn
  name = G4_Rn
  specific = 4
FEATURE [App::DocumentObjectGroupPython] Fr_element001  label="Fr_element : 1"  # scripted group (container) (typed FeaturePython)
  n = 1
  ref = Fr_element
FEATURE [App::DocumentObjectGroupPython] G4_Fr  # scripted group (container) (typed FeaturePython)
  Dunit = g/cm3
  Dvalue = 1
  Group = -> [Fr_element001]
  conduct = 2
  density = 1
  expand = 3
  formula = Fr
  name = G4_Fr
  specific = 4
FEATURE [App::DocumentObjectGroupPython] Ra_element001  label="Ra_element : 1"  # scripted group (container) (typed FeaturePython)
  n = 1
  ref = Ra_element
FEATURE [App::DocumentObjectGroupPython] G4_Ra  # scripted group (container) (typed FeaturePython)
  Dunit = g/cm3
  Dvalue = 5
  Group = -> [Ra_element001]
  conduct = 2
  density = 1
  expand = 3
  formula = Ra
  name = G4_Ra
  specific = 4
FEATURE [App::DocumentObjectGroupPython] Ac_element001  label="Ac_element : 1"  # scripted group (container) (typed FeaturePython)
  n = 1
  ref = Ac_element
FEATURE [App::DocumentObjectGroupPython] G4_Ac  # scripted group (container) (typed FeaturePython)
  Dunit = g/cm3
  Dvalue = 10.07
  Group = -> [Ac_element001]
  conduct = 2
  density = 1
  expand = 3
  formula = Ac
  name = G4_Ac
  specific = 4
FEATURE [App::DocumentObjectGroupPython] Th_element001  label="Th_element : 1"  # scripted group (container) (typed FeaturePython)
  n = 1
  ref = Th_element
FEATURE [App::DocumentObjectGroupPython] G4_Th  # scripted group (container) (typed FeaturePython)
  Dunit = g/cm3
  Dvalue = 11.72
  Group = -> [Th_element001]
  conduct = 2
  density = 1
  expand = 3
  formula = Th
  name = G4_Th
  specific = 4
FEATURE [App::DocumentObjectGroupPython] Pa_element001  label="Pa_element : 1"  # scripted group (container) (typed FeaturePython)
  n = 1
  ref = Pa_element
FEATURE [App::DocumentObjectGroupPython] G4_Pa  # scripted group (container) (typed FeaturePython)
  Dunit = g/cm3
  Dvalue = 15.37
  Group = -> [Pa_element001]
  conduct = 2
  density = 1
  expand = 3
  formula = Pa
  name = G4_Pa
  specific = 4
FEATURE [App::DocumentObjectGroupPython] U_element004  label="U_element : 004"  # scripted group (container) (typed FeaturePython)
  n = 1
  ref = U_element
FEATURE [App::DocumentObjectGroupPython] G4_U  # scripted group (container) (typed FeaturePython)
  Dunit = g/cm3
  Dvalue = 18.95
  Group = -> [U_element004]
  conduct = 2
  density = 1
  expand = 3
  formula = U
  name = G4_U
  specific = 4
FEATURE [App::DocumentObjectGroupPython] Np_element001  label="Np_element : 1"  # scripted group (container) (typed FeaturePython)
  n = 1
  ref = Np_element
FEATURE [App::DocumentObjectGroupPython] G4_Np  # scripted group (container) (typed FeaturePython)
  Dunit = g/cm3
  Dvalue = 20.25
  Group = -> [Np_element001]
  conduct = 2
  density = 1
  expand = 3
  formula = Np
  name = G4_Np
  specific = 4
FEATURE [App::DocumentObjectGroupPython] Pu_element002  label="Pu_element : 002"  # scripted group (container) (typed FeaturePython)
  n = 1
  ref = Pu_element
FEATURE [App::DocumentObjectGroupPython] G4_Pu  # scripted group (container) (typed FeaturePython)
  Dunit = g/cm3
  Dvalue = 19.84
  Group = -> [Pu_element002]
  conduct = 2
  density = 1
  expand = 3
  formula = Pu
  name = G4_Pu
  specific = 4
FEATURE [App::DocumentObjectGroupPython] Am_element001  label="Am_element : 1"  # scripted group (container) (typed FeaturePython)
  n = 1
  ref = Am_element
FEATURE [App::DocumentObjectGroupPython] G4_Am  # scripted group (container) (typed FeaturePython)
  Dunit = g/cm3
  Dvalue = 13.67
  Group = -> [Am_element001]
  conduct = 2
  density = 1
  expand = 3
  formula = Am
  name = G4_Am
  specific = 4
FEATURE [App::DocumentObjectGroupPython] Cm_element001  label="Cm_element : 1"  # scripted group (container) (typed FeaturePython)
  n = 1
  ref = Cm_element
FEATURE [App::DocumentObjectGroupPython] G4_Cm  # scripted group (container) (typed FeaturePython)
  Dunit = g/cm3
  Dvalue = 13.51
  Group = -> [Cm_element001]
  conduct = 2
  density = 1
  expand = 3
  formula = Cm
  name = G4_Cm
  specific = 4
FEATURE [App::DocumentObjectGroupPython] Bk_element001  label="Bk_element : 1"  # scripted group (container) (typed FeaturePython)
  n = 1
  ref = Bk_element
FEATURE [App::DocumentObjectGroupPython] G4_Bk  # scripted group (container) (typed FeaturePython)
  Dunit = g/cm3
  Dvalue = 14
  Group = -> [Bk_element001]
  conduct = 2
  density = 1
  expand = 3
  formula = Bk
  name = G4_Bk
  specific = 4
FEATURE [App::DocumentObjectGroupPython] Cf_element001  label="Cf_element : 1"  # scripted group (container) (typed FeaturePython)
  n = 1
  ref = Cf_element
FEATURE [App::DocumentObjectGroupPython] G4_Cf  # scripted group (container) (typed FeaturePython)
  Dunit = g/cm3
  Dvalue = 10
  Group = -> [Cf_element001]
  conduct = 2
  density = 1
  expand = 3
  formula = Cf
  name = G4_Cf
  specific = 4
FEATURE [App::DocumentObjectGroupPython] Element  # scripted group (container) (typed FeaturePython)
  Group = -> [G4_H,G4_He,G4_Li,G4_Be,G4_B,G4_C,G4_N,G4_O,G4_F,G4_Ne,G4_Na,G4_Mg,G4_Al,G4_Si,G4_P,G4_S,G4_Cl,G4_Ar,G4_K,G4_Ca,G4_Sc,G4_Ti,G4_V,G4_Cr,G4_Mn,G4_Fe,G4_Co,G4_Ni,G4_Cu,G4_Zn,G4_Ga,G4_Ge,G4_As,G4_Se,G4_Br,G4_Kr,G4_Rb,G4_Sr,G4_Y,G4_Zr,G4_Nb,G4_Mo,G4_Tc,G4_Ru,G4_Rh,G4_Pd,G4_Ag,G4_Cd,G4_In,G4_Sn,G4_Sb,G4_Te,G4_I,G4_Xe,G4_Cs,G4_Ba,G4_La,G4_Ce,G4_Pr,G4_Nd,G4_Pm,G4_Sm,G4_Eu,G4_Gd,G4_Tb,G4_Dy,G4_Ho,G4_Er,+30 more]
FEATURE [App::DocumentObjectGroupPython] H_element114  label="H_element : 063"  # scripted group (container) (typed FeaturePython)
  n = 2
  ref = H_element
FEATURE [App::DocumentObjectGroupPython] G4_lH2  # scripted group (container) (typed FeaturePython)
  Dunit = g/cm3
  Dvalue = 0.0708
  Group = -> [H_element114]
  conduct = 2
  density = 1
  expand = 3
  formula = G4_lH2
  name = G4_lH2
  specific = 4
FEATURE [App::DocumentObjectGroupPython] N_element049  label="N_element : 022"  # scripted group (container) (typed FeaturePython)
  n = 2
  ref = N_element
FEATURE [App::DocumentObjectGroupPython] G4_lN2  # scripted group (container) (typed FeaturePython)
  Dunit = g/cm3
  Dvalue = 0.807
  Group = -> [N_element049]
  conduct = 2
  density = 1
  expand = 3
  formula = G4_lN2
  name = G4_lN2
  specific = 4
FEATURE [App::DocumentObjectGroupPython] O_element106  label="O_element : 060"  # scripted group (container) (typed FeaturePython)
  n = 2
  ref = O_element
FEATURE [App::DocumentObjectGroupPython] G4_lO2  # scripted group (container) (typed FeaturePython)
  Dunit = g/cm3
  Dvalue = 1.141
  Group = -> [O_element106]
  conduct = 2
  density = 1
  expand = 3
  formula = G4_lO2
  name = G4_lO2
  specific = 4
FEATURE [App::DocumentObjectGroupPython] Ar_element003  label="Ar_element : 002"  # scripted group (container) (typed FeaturePython)
  n = 1
  ref = Ar_element
FEATURE [App::DocumentObjectGroupPython] G4_lAr  # scripted group (container) (typed FeaturePython)
  Dunit = g/cm3
  Dvalue = 1.396
  Group = -> [Ar_element003]
  conduct = 2
  density = 1
  expand = 3
  formula = G4_lAr
  name = G4_lAr
  specific = 4
FEATURE [App::DocumentObjectGroupPython] Br_element008  label="Br_element : 005"  # scripted group (container) (typed FeaturePython)
  n = 1
  ref = Br_element
FEATURE [App::DocumentObjectGroupPython] G4_lBr  # scripted group (container) (typed FeaturePython)
  Dunit = g/cm3
  Dvalue = 3.1028
  Group = -> [Br_element008]
  conduct = 2
  density = 1
  expand = 3
  formula = G4_lBr
  name = G4_lBr
  specific = 4
FEATURE [App::DocumentObjectGroupPython] Kr_element002  label="Kr_element : 002"  # scripted group (container) (typed FeaturePython)
  n = 1
  ref = Kr_element
FEATURE [App::DocumentObjectGroupPython] G4_lKr  # scripted group (container) (typed FeaturePython)
  Dunit = g/cm3
  Dvalue = 2.418
  Group = -> [Kr_element002]
  conduct = 2
  density = 1
  expand = 3
  formula = G4_lKr
  name = G4_lKr
  specific = 4
FEATURE [App::DocumentObjectGroupPython] Xe_element002  label="Xe_element : 002"  # scripted group (container) (typed FeaturePython)
  n = 1
  ref = Xe_element
FEATURE [App::DocumentObjectGroupPython] G4_lXe  # scripted group (container) (typed FeaturePython)
  Dunit = g/cm3
  Dvalue = 2.953
  Group = -> [Xe_element002]
  conduct = 2
  density = 1
  expand = 3
  formula = G4_lXe
  name = G4_lXe
  specific = 4
FEATURE [App::DocumentObjectGroupPython] O_element107  label="O_element : 061"  # scripted group (container) (typed FeaturePython)
  n = 4
  ref = O_element
FEATURE [App::DocumentObjectGroupPython] Pb_element004  label="Pb_element : 002"  # scripted group (container) (typed FeaturePython)
  n = 1
  ref = Pb_element
FEATURE [App::DocumentObjectGroupPython] W_element005  label="W_element : 005"  # scripted group (container) (typed FeaturePython)
  n = 1
  ref = W_element
FEATURE [App::DocumentObjectGroupPython] G4_PbWO4  # scripted group (container) (typed FeaturePython)
  Dunit = g/cm3
  Dvalue = 8.28
  Group = -> [O_element107,Pb_element004,W_element005]
  conduct = 2
  density = 1
  expand = 3
  formula = G4_PbWO4
  name = G4_PbWO4
  specific = 4
FEATURE [App::DocumentObjectGroupPython] H_element115  label="H_element : 064"  # scripted group (container) (typed FeaturePython)
  n = 1
  ref = H_element
FEATURE [App::DocumentObjectGroupPython] G4_Galactic  # scripted group (container) (typed FeaturePython)
  Dunit = g/cm3
  Dvalue = 0
  Group = -> [H_element115]
  conduct = 2
  density = 1
  expand = 3
  formula = G4_Galactic
  name = G4_Galactic
  specific = 4
FEATURE [App::DocumentObjectGroupPython] C_element125  label="C_element : 071"  # scripted group (container) (typed FeaturePython)
  n = 1
  ref = C_element
FEATURE [App::DocumentObjectGroupPython] G4_GRAPHITE_POROUS  # scripted group (container) (typed FeaturePython)
  Dunit = g/cm3
  Dvalue = 1.7
  Group = -> [C_element125]
  conduct = 2
  density = 1
  expand = 3
  formula = G4_GRAPHITE_POROUS
  name = G4_GRAPHITE_POROUS
  specific = 4
FEATURE [App::DocumentObjectGroupPython] H_element116  label="H_element : 0.150"  # scripted group (container) (typed FeaturePython)
  n = 0.080538
FEATURE [App::DocumentObjectGroupPython] C_element126  label="C_element : 0.600"  # scripted group (container) (typed FeaturePython)
  n = 0.599848
FEATURE [App::DocumentObjectGroupPython] O_element108  label="O_element : 0.320"  # scripted group (container) (typed FeaturePython)
  n = 0.319614
FEATURE [App::DocumentObjectGroupPython] G4_LUCITE  # scripted group (container) (typed FeaturePython)
  Dunit = g/cm3
  Dvalue = 1.19
  Group = -> [H_element116,C_element126,O_element108]
  conduct = 2
  density = 1
  expand = 3
  formula = G4_LUCITE
  name = G4_LUCITE
  specific = 4
FEATURE [App::DocumentObjectGroupPython] Cu_element002  label="Cu_element : 62"  # scripted group (container) (typed FeaturePython)
  n = 62
  ref = Cu_element
FEATURE [App::DocumentObjectGroupPython] Zn_element002  label="Zn_element : 35"  # scripted group (container) (typed FeaturePython)
  n = 35
  ref = Zn_element
FEATURE [App::DocumentObjectGroupPython] Pb_element005  label="Pb_element : 3"  # scripted group (container) (typed FeaturePython)
  n = 3
  ref = Pb_element
FEATURE [App::DocumentObjectGroupPython] G4_BRASS  # scripted group (container) (typed FeaturePython)
  Dunit = g/cm3
  Dvalue = 8.52
  Group = -> [Cu_element002,Zn_element002,Pb_element005]
  conduct = 2
  density = 1
  expand = 3
  formula = G4_BRASS
  name = G4_BRASS
  specific = 4
FEATURE [App::DocumentObjectGroupPython] Cu_element003  label="Cu_element : 89"  # scripted group (container) (typed FeaturePython)
  n = 89
  ref = Cu_element
FEATURE [App::DocumentObjectGroupPython] Zn_element003  label="Zn_element : 9"  # scripted group (container) (typed FeaturePython)
  n = 9
  ref = Zn_element
FEATURE [App::DocumentObjectGroupPython] Pb_element006  label="Pb_element : 2"  # scripted group (container) (typed FeaturePython)
  n = 2
  ref = Pb_element
FEATURE [App::DocumentObjectGroupPython] G4_BRONZE  # scripted group (container) (typed FeaturePython)
  Dunit = g/cm3
  Dvalue = 8.82
  Group = -> [Cu_element003,Zn_element003,Pb_element006]
  conduct = 2
  density = 1
  expand = 3
  formula = G4_BRONZE
  name = G4_BRONZE
  specific = 4
FEATURE [App::DocumentObjectGroupPython] Fe_element008  label="Fe_element : 74"  # scripted group (container) (typed FeaturePython)
  n = 74
  ref = Fe_element
FEATURE [App::DocumentObjectGroupPython] Cr_element002  label="Cr_element : 18"  # scripted group (container) (typed FeaturePython)
  n = 18
  ref = Cr_element
FEATURE [App::DocumentObjectGroupPython] Ni_element002  label="Ni_element : 8"  # scripted group (container) (typed FeaturePython)
  n = 8
  ref = Ni_element
FEATURE [App::DocumentObjectGroupPython] G4_STAINLESS_STEEL  label="G4_STAINLESS-STEEL"  # scripted group (container) (typed FeaturePython)
  Dunit = g/cm3
  Dvalue = 8
  Group = -> [Fe_element008,Cr_element002,Ni_element002]
  conduct = 2
  density = 1
  expand = 3
  formula = G4_STAINLESS-STEEL
  name = G4_STAINLESS-STEEL
  specific = 4
FEATURE [App::DocumentObjectGroupPython] H_element117  label="H_element : 065"  # scripted group (container) (typed FeaturePython)
  n = 18
  ref = H_element
FEATURE [App::DocumentObjectGroupPython] C_element127  label="C_element : 072"  # scripted group (container) (typed FeaturePython)
  n = 12
  ref = C_element
FEATURE [App::DocumentObjectGroupPython] O_element109  label="O_element : 062"  # scripted group (container) (typed FeaturePython)
  n = 7
  ref = O_element
FEATURE [App::DocumentObjectGroupPython] G4_CR39  # scripted group (container) (typed FeaturePython)
  Dunit = g/cm3
  Dvalue = 1.32
  Group = -> [H_element117,C_element127,O_element109]
  conduct = 2
  density = 1
  expand = 3
  formula = G4_CR39
  name = G4_CR39
  specific = 4
FEATURE [App::DocumentObjectGroupPython] H_element118  label="H_element : 38"  # scripted group (container) (typed FeaturePython)
  n = 38
  ref = H_element
FEATURE [App::DocumentObjectGroupPython] C_element128  label="C_element : 073"  # scripted group (container) (typed FeaturePython)
  n = 18
  ref = C_element
FEATURE [App::DocumentObjectGroupPython] O_element110  label="O_element : 063"  # scripted group (container) (typed FeaturePython)
  n = 1
  ref = O_element
FEATURE [App::DocumentObjectGroupPython] G4_OCTADECANOL  # scripted group (container) (typed FeaturePython)
  Dunit = g/cm3
  Dvalue = 0.812
  Group = -> [H_element118,C_element128,O_element110]
  conduct = 2
  density = 1
  expand = 3
  formula = G4_OCTADECANOL
  name = G4_OCTADECANOL
  specific = 4
FEATURE [App::DocumentObjectGroupPython] HEP  # scripted group (container) (typed FeaturePython)
  Group = -> [G4_lH2,G4_lN2,G4_lO2,G4_lAr,G4_lBr,G4_lKr,G4_lXe,G4_PbWO4,G4_Galactic,G4_GRAPHITE_POROUS,G4_LUCITE,G4_BRASS,G4_BRONZE,G4_STAINLESS_STEEL,G4_CR39,G4_OCTADECANOL]
FEATURE [App::DocumentObjectGroupPython] C_element129  label="C_element : 074"  # scripted group (container) (typed FeaturePython)
  n = 14
  ref = C_element
FEATURE [App::DocumentObjectGroupPython] H_element119  label="H_element : 066"  # scripted group (container) (typed FeaturePython)
  n = 10
  ref = H_element
FEATURE [App::DocumentObjectGroupPython] O_element111  label="O_element : 064"  # scripted group (container) (typed FeaturePython)
  n = 2
  ref = O_element
FEATURE [App::DocumentObjectGroupPython] N_element050  label="N_element : 023"  # scripted group (container) (typed FeaturePython)
  n = 2
  ref = N_element
FEATURE [App::DocumentObjectGroupPython] G4_KEVLAR  # scripted group (container) (typed FeaturePython)
  Dunit = g/cm3
  Dvalue = 1.44
  Group = -> [C_element129,H_element119,O_element111,N_element050]
  conduct = 2
  density = 1
  expand = 3
  formula = G4_KEVLAR
  name = G4_KEVLAR
  specific = 4
FEATURE [App::DocumentObjectGroupPython] C_element130  label="C_element : 075"  # scripted group (container) (typed FeaturePython)
  n = 10
  ref = C_element
FEATURE [App::DocumentObjectGroupPython] H_element120  label="H_element : 067"  # scripted group (container) (typed FeaturePython)
  n = 8
  ref = H_element
FEATURE [App::DocumentObjectGroupPython] O_element112  label="O_element : 065"  # scripted group (container) (typed FeaturePython)
  n = 4
  ref = O_element
FEATURE [App::DocumentObjectGroupPython] G4_DACRON  # scripted group (container) (typed FeaturePython)
  Dunit = g/cm3
  Dvalue = 1.4
  Group = -> [C_element130,H_element120,O_element112]
  conduct = 2
  density = 1
  expand = 3
  formula = G4_DACRON
  name = G4_DACRON
  specific = 4
FEATURE [App::DocumentObjectGroupPython] C_element131  label="C_element : 076"  # scripted group (container) (typed FeaturePython)
  n = 4
  ref = C_element
FEATURE [App::DocumentObjectGroupPython] H_element121  label="H_element : 068"  # scripted group (container) (typed FeaturePython)
  n = 5
  ref = H_element
FEATURE [App::DocumentObjectGroupPython] Cl_element030  label="Cl_element : 016"  # scripted group (container) (typed FeaturePython)
  n = 1
  ref = Cl_element
FEATURE [App::DocumentObjectGroupPython] G4_NEOPRENE  # scripted group (container) (typed FeaturePython)
  Dunit = g/cm3
  Dvalue = 1.23
  Group = -> [C_element131,H_element121,Cl_element030]
  conduct = 2
  density = 1
  expand = 3
  formula = G4_NEOPRENE
  name = G4_NEOPRENE
  specific = 4
FEATURE [App::DocumentObjectGroupPython] Space  # scripted group (container) (typed FeaturePython)
  Group = -> [G4_KEVLAR,G4_DACRON,G4_NEOPRENE]
FEATURE [App::DocumentObjectGroupPython] H_element122  label="H_element : 069"  # scripted group (container) (typed FeaturePython)
  n = 5
  ref = H_element
FEATURE [App::DocumentObjectGroupPython] C_element132  label="C_element : 077"  # scripted group (container) (typed FeaturePython)
  n = 4
  ref = C_element
FEATURE [App::DocumentObjectGroupPython] N_element051  label="N_element : 3"  # scripted group (container) (typed FeaturePython)
  n = 3
  ref = N_element
FEATURE [App::DocumentObjectGroupPython] O_element113  label="O_element : 066"  # scripted group (container) (typed FeaturePython)
  n = 1
  ref = O_element
FEATURE [App::DocumentObjectGroupPython] G4_CYTOSINE  # scripted group (container) (typed FeaturePython)
  Dunit = g/cm3
  Dvalue = 1.55
  Group = -> [H_element122,C_element132,N_element051,O_element113]
  conduct = 2
  density = 1
  expand = 3
  formula = G4_CYTOSINE
  name = G4_CYTOSINE
  specific = 4
FEATURE [App::DocumentObjectGroupPython] H_element123  label="H_element : 070"  # scripted group (container) (typed FeaturePython)
  n = 6
  ref = H_element
FEATURE [App::DocumentObjectGroupPython] C_element133  label="C_element : 078"  # scripted group (container) (typed FeaturePython)
  n = 5
  ref = C_element
FEATURE [App::DocumentObjectGroupPython] N_element052  label="N_element : 024"  # scripted group (container) (typed FeaturePython)
  n = 2
  ref = N_element
FEATURE [App::DocumentObjectGroupPython] O_element114  label="O_element : 067"  # scripted group (container) (typed FeaturePython)
  n = 2
  ref = O_element
FEATURE [App::DocumentObjectGroupPython] G4_THYMINE  # scripted group (container) (typed FeaturePython)
  Dunit = g/cm3
  Dvalue = 1.23
  Group = -> [H_element123,C_element133,N_element052,O_element114]
  conduct = 2
  density = 1
  expand = 3
  formula = G4_THYMINE
  name = G4_THYMINE
  specific = 4
FEATURE [App::DocumentObjectGroupPython] H_element124  label="H_element : 071"  # scripted group (container) (typed FeaturePython)
  n = 4
  ref = H_element
FEATURE [App::DocumentObjectGroupPython] C_element134  label="C_element : 079"  # scripted group (container) (typed FeaturePython)
  n = 4
  ref = C_element
FEATURE [App::DocumentObjectGroupPython] N_element053  label="N_element : 025"  # scripted group (container) (typed FeaturePython)
  n = 2
  ref = N_element
FEATURE [App::DocumentObjectGroupPython] O_element115  label="O_element : 068"  # scripted group (container) (typed FeaturePython)
  n = 2
  ref = O_element
FEATURE [App::DocumentObjectGroupPython] G4_URACIL  # scripted group (container) (typed FeaturePython)
  Dunit = g/cm3
  Dvalue = 1.32
  Group = -> [H_element124,C_element134,N_element053,O_element115]
  conduct = 2
  density = 1
  expand = 3
  formula = G4_URACIL
  name = G4_URACIL
  specific = 4
FEATURE [App::DocumentObjectGroupPython] H_element125  label="H_element : 072"  # scripted group (container) (typed FeaturePython)
  n = 4
  ref = H_element
FEATURE [App::DocumentObjectGroupPython] C_element135  label="C_element : 080"  # scripted group (container) (typed FeaturePython)
  n = 5
  ref = C_element
FEATURE [App::DocumentObjectGroupPython] N_element054  label="N_element : 026"  # scripted group (container) (typed FeaturePython)
  n = 5
  ref = N_element
FEATURE [App::DocumentObjectGroupPython] G4_DNA_ADENINE  # scripted group (container) (typed FeaturePython)
  Dunit = g/cm3
  Dvalue = 1
  Group = -> [H_element125,C_element135,N_element054]
  conduct = 2
  density = 1
  expand = 3
  formula = G4_DNA_ADENINE
  name = G4_DNA_ADENINE
  specific = 4
FEATURE [App::DocumentObjectGroupPython] H_element126  label="H_element : 073"  # scripted group (container) (typed FeaturePython)
  n = 4
  ref = H_element
FEATURE [App::DocumentObjectGroupPython] C_element136  label="C_element : 081"  # scripted group (container) (typed FeaturePython)
  n = 5
  ref = C_element
FEATURE [App::DocumentObjectGroupPython] N_element055  label="N_element : 027"  # scripted group (container) (typed FeaturePython)
  n = 5
  ref = N_element
FEATURE [App::DocumentObjectGroupPython] O_element116  label="O_element : 069"  # scripted group (container) (typed FeaturePython)
  n = 1
  ref = O_element
FEATURE [App::DocumentObjectGroupPython] G4_DNA_GUANINE  # scripted group (container) (typed FeaturePython)
  Dunit = g/cm3
  Dvalue = 1
  Group = -> [H_element126,C_element136,N_element055,O_element116]
  conduct = 2
  density = 1
  expand = 3
  formula = G4_DNA_GUANINE
  name = G4_DNA_GUANINE
  specific = 4
FEATURE [App::DocumentObjectGroupPython] H_element127  label="H_element : 074"  # scripted group (container) (typed FeaturePython)
  n = 4
  ref = H_element
FEATURE [App::DocumentObjectGroupPython] C_element137  label="C_element : 082"  # scripted group (container) (typed FeaturePython)
  n = 4
  ref = C_element
FEATURE [App::DocumentObjectGroupPython] N_element056  label="N_element : 028"  # scripted group (container) (typed FeaturePython)
  n = 3
  ref = N_element
FEATURE [App::DocumentObjectGroupPython] O_element117  label="O_element : 070"  # scripted group (container) (typed FeaturePython)
  n = 1
  ref = O_element
FEATURE [App::DocumentObjectGroupPython] G4_DNA_CYTOSINE  # scripted group (container) (typed FeaturePython)
  Dunit = g/cm3
  Dvalue = 1
  Group = -> [H_element127,C_element137,N_element056,O_element117]
  conduct = 2
  density = 1
  expand = 3
  formula = G4_DNA_CYTOSINE
  name = G4_DNA_CYTOSINE
  specific = 4
FEATURE [App::DocumentObjectGroupPython] H_element128  label="H_element : 075"  # scripted group (container) (typed FeaturePython)
  n = 5
  ref = H_element
FEATURE [App::DocumentObjectGroupPython] C_element138  label="C_element : 083"  # scripted group (container) (typed FeaturePython)
  n = 5
  ref = C_element
FEATURE [App::DocumentObjectGroupPython] N_element057  label="N_element : 029"  # scripted group (container) (typed FeaturePython)
  n = 2
  ref = N_element
FEATURE [App::DocumentObjectGroupPython] O_element118  label="O_element : 071"  # scripted group (container) (typed FeaturePython)
  n = 2
  ref = O_element
FEATURE [App::DocumentObjectGroupPython] G4_DNA_THYMINE  # scripted group (container) (typed FeaturePython)
  Dunit = g/cm3
  Dvalue = 1
  Group = -> [H_element128,C_element138,N_element057,O_element118]
  conduct = 2
  density = 1
  expand = 3
  formula = G4_DNA_THYMINE
  name = G4_DNA_THYMINE
  specific = 4
FEATURE [App::DocumentObjectGroupPython] H_element129  label="H_element : 076"  # scripted group (container) (typed FeaturePython)
  n = 3
  ref = H_element
FEATURE [App::DocumentObjectGroupPython] C_element139  label="C_element : 084"  # scripted group (container) (typed FeaturePython)
  n = 4
  ref = C_element
FEATURE [App::DocumentObjectGroupPython] N_element058  label="N_element : 030"  # scripted group (container) (typed FeaturePython)
  n = 2
  ref = N_element
FEATURE [App::DocumentObjectGroupPython] O_element119  label="O_element : 072"  # scripted group (container) (typed FeaturePython)
  n = 2
  ref = O_element
FEATURE [App::DocumentObjectGroupPython] G4_DNA_URACIL  # scripted group (container) (typed FeaturePython)
  Dunit = g/cm3
  Dvalue = 1
  Group = -> [H_element129,C_element139,N_element058,O_element119]
  conduct = 2
  density = 1
  expand = 3
  formula = G4_DNA_URACIL
  name = G4_DNA_URACIL
  specific = 4
FEATURE [App::DocumentObjectGroupPython] H_element130  label="H_element : 077"  # scripted group (container) (typed FeaturePython)
  n = 10
  ref = H_element
FEATURE [App::DocumentObjectGroupPython] C_element140  label="C_element : 085"  # scripted group (container) (typed FeaturePython)
  n = 10
  ref = C_element
FEATURE [App::DocumentObjectGroupPython] N_element059  label="N_element : 031"  # scripted group (container) (typed FeaturePython)
  n = 5
  ref = N_element
FEATURE [App::DocumentObjectGroupPython] O_element120  label="O_element : 073"  # scripted group (container) (typed FeaturePython)
  n = 4
  ref = O_element
FEATURE [App::DocumentObjectGroupPython] G4_DNA_ADENOSINE  # scripted group (container) (typed FeaturePython)
  Dunit = g/cm3
  Dvalue = 1
  Group = -> [H_element130,C_element140,N_element059,O_element120]
  conduct = 2
  density = 1
  expand = 3
  formula = G4_DNA_ADENOSINE
  name = G4_DNA_ADENOSINE
  specific = 4
FEATURE [App::DocumentObjectGroupPython] H_element131  label="H_element : 078"  # scripted group (container) (typed FeaturePython)
  n = 10
  ref = H_element
FEATURE [App::DocumentObjectGroupPython] C_element141  label="C_element : 086"  # scripted group (container) (typed FeaturePython)
  n = 10
  ref = C_element
FEATURE [App::DocumentObjectGroupPython] N_element060  label="N_element : 032"  # scripted group (container) (typed FeaturePython)
  n = 5
  ref = N_element
FEATURE [App::DocumentObjectGroupPython] O_element121  label="O_element : 074"  # scripted group (container) (typed FeaturePython)
  n = 5
  ref = O_element
FEATURE [App::DocumentObjectGroupPython] G4_DNA_GUANOSINE  # scripted group (container) (typed FeaturePython)
  Dunit = g/cm3
  Dvalue = 1
  Group = -> [H_element131,C_element141,N_element060,O_element121]
  conduct = 2
  density = 1
  expand = 3
  formula = G4_DNA_GUANOSINE
  name = G4_DNA_GUANOSINE
  specific = 4
FEATURE [App::DocumentObjectGroupPython] H_element132  label="H_element : 079"  # scripted group (container) (typed FeaturePython)
  n = 10
  ref = H_element
FEATURE [App::DocumentObjectGroupPython] C_element142  label="C_element : 087"  # scripted group (container) (typed FeaturePython)
  n = 9
  ref = C_element
FEATURE [App::DocumentObjectGroupPython] N_element061  label="N_element : 033"  # scripted group (container) (typed FeaturePython)
  n = 3
  ref = N_element
FEATURE [App::DocumentObjectGroupPython] O_element122  label="O_element : 075"  # scripted group (container) (typed FeaturePython)
  n = 5
  ref = O_element
FEATURE [App::DocumentObjectGroupPython] G4_DNA_CYTIDINE  # scripted group (container) (typed FeaturePython)
  Dunit = g/cm3
  Dvalue = 1
  Group = -> [H_element132,C_element142,N_element061,O_element122]
  conduct = 2
  density = 1
  expand = 3
  formula = G4_DNA_CYTIDINE
  name = G4_DNA_CYTIDINE
  specific = 4
FEATURE [App::DocumentObjectGroupPython] H_element133  label="H_element : 080"  # scripted group (container) (typed FeaturePython)
  n = 9
  ref = H_element
FEATURE [App::DocumentObjectGroupPython] C_element143  label="C_element : 088"  # scripted group (container) (typed FeaturePython)
  n = 9
  ref = C_element
FEATURE [App::DocumentObjectGroupPython] N_element062  label="N_element : 034"  # scripted group (container) (typed FeaturePython)
  n = 2
  ref = N_element
FEATURE [App::DocumentObjectGroupPython] O_element123  label="O_element : 076"  # scripted group (container) (typed FeaturePython)
  n = 6
  ref = O_element
FEATURE [App::DocumentObjectGroupPython] G4_DNA_URIDINE  # scripted group (container) (typed FeaturePython)
  Dunit = g/cm3
  Dvalue = 1
  Group = -> [H_element133,C_element143,N_element062,O_element123]
  conduct = 2
  density = 1
  expand = 3
  formula = G4_DNA_URIDINE
  name = G4_DNA_URIDINE
  specific = 4
FEATURE [App::DocumentObjectGroupPython] H_element134  label="H_element : 081"  # scripted group (container) (typed FeaturePython)
  n = 11
  ref = H_element
FEATURE [App::DocumentObjectGroupPython] C_element144  label="C_element : 089"  # scripted group (container) (typed FeaturePython)
  n = 10
  ref = C_element
FEATURE [App::DocumentObjectGroupPython] N_element063  label="N_element : 035"  # scripted group (container) (typed FeaturePython)
  n = 2
  ref = N_element
FEATURE [App::DocumentObjectGroupPython] O_element124  label="O_element : 077"  # scripted group (container) (typed FeaturePython)
  n = 6
  ref = O_element
FEATURE [App::DocumentObjectGroupPython] G4_DNA_METHYLURIDINE  # scripted group (container) (typed FeaturePython)
  Dunit = g/cm3
  Dvalue = 1
  Group = -> [H_element134,C_element144,N_element063,O_element124]
  conduct = 2
  density = 1
  expand = 3
  formula = G4_DNA_METHYLURIDINE
  name = G4_DNA_METHYLURIDINE
  specific = 4
FEATURE [App::DocumentObjectGroupPython] P_element014  label="P_element : 003"  # scripted group (container) (typed FeaturePython)
  n = 1
  ref = P_element
FEATURE [App::DocumentObjectGroupPython] O_element125  label="O_element : 078"  # scripted group (container) (typed FeaturePython)
  n = 3
  ref = O_element
FEATURE [App::DocumentObjectGroupPython] G4_DNA_MONOPHOSPHATE  # scripted group (container) (typed FeaturePython)
  Dunit = g/cm3
  Dvalue = 1
  Group = -> [P_element014,O_element125]
  conduct = 2
  density = 1
  expand = 3
  formula = G4_DNA_MONOPHOSPHATE
  name = G4_DNA_MONOPHOSPHATE
  specific = 4
FEATURE [App::DocumentObjectGroupPython] H_element135  label="H_element : 082"  # scripted group (container) (typed FeaturePython)
  n = 10
  ref = H_element
FEATURE [App::DocumentObjectGroupPython] C_element145  label="C_element : 090"  # scripted group (container) (typed FeaturePython)
  n = 10
  ref = C_element
FEATURE [App::DocumentObjectGroupPython] N_element064  label="N_element : 036"  # scripted group (container) (typed FeaturePython)
  n = 5
  ref = N_element
FEATURE [App::DocumentObjectGroupPython] O_element126  label="O_element : 079"  # scripted group (container) (typed FeaturePython)
  n = 7
  ref = O_element
FEATURE [App::DocumentObjectGroupPython] P_element015  label="P_element : 004"  # scripted group (container) (typed FeaturePython)
  n = 1
  ref = P_element
FEATURE [App::DocumentObjectGroupPython] G4_DNA_A  # scripted group (container) (typed FeaturePython)
  Dunit = g/cm3
  Dvalue = 1
  Group = -> [H_element135,C_element145,N_element064,O_element126,P_element015]
  conduct = 2
  density = 1
  expand = 3
  formula = G4_DNA_A
  name = G4_DNA_A
  specific = 4
FEATURE [App::DocumentObjectGroupPython] H_element136  label="H_element : 083"  # scripted group (container) (typed FeaturePython)
  n = 10
  ref = H_element
FEATURE [App::DocumentObjectGroupPython] C_element146  label="C_element : 091"  # scripted group (container) (typed FeaturePython)
  n = 10
  ref = C_element
FEATURE [App::DocumentObjectGroupPython] N_element065  label="N_element : 037"  # scripted group (container) (typed FeaturePython)
  n = 5
  ref = N_element
FEATURE [App::DocumentObjectGroupPython] O_element127  label="O_element : 8"  # scripted group (container) (typed FeaturePython)
  n = 8
  ref = O_element
FEATURE [App::DocumentObjectGroupPython] P_element016  label="P_element : 005"  # scripted group (container) (typed FeaturePython)
  n = 1
  ref = P_element
FEATURE [App::DocumentObjectGroupPython] G4_DNA_G  # scripted group (container) (typed FeaturePython)
  Dunit = g/cm3
  Dvalue = 1
  Group = -> [H_element136,C_element146,N_element065,O_element127,P_element016]
  conduct = 2
  density = 1
  expand = 3
  formula = G4_DNA_G
  name = G4_DNA_G
  specific = 4
FEATURE [App::DocumentObjectGroupPython] H_element137  label="H_element : 084"  # scripted group (container) (typed FeaturePython)
  n = 10
  ref = H_element
FEATURE [App::DocumentObjectGroupPython] C_element147  label="C_element : 092"  # scripted group (container) (typed FeaturePython)
  n = 9
  ref = C_element
FEATURE [App::DocumentObjectGroupPython] N_element066  label="N_element : 038"  # scripted group (container) (typed FeaturePython)
  n = 3
  ref = N_element
FEATURE [App::DocumentObjectGroupPython] O_element128  label="O_element : 080"  # scripted group (container) (typed FeaturePython)
  n = 8
  ref = O_element
FEATURE [App::DocumentObjectGroupPython] P_element017  label="P_element : 006"  # scripted group (container) (typed FeaturePython)
  n = 1
  ref = P_element
FEATURE [App::DocumentObjectGroupPython] G4_DNA_C  # scripted group (container) (typed FeaturePython)
  Dunit = g/cm3
  Dvalue = 1
  Group = -> [H_element137,C_element147,N_element066,O_element128,P_element017]
  conduct = 2
  density = 1
  expand = 3
  formula = G4_DNA_C
  name = G4_DNA_C
  specific = 4
FEATURE [App::DocumentObjectGroupPython] H_element138  label="H_element : 085"  # scripted group (container) (typed FeaturePython)
  n = 9
  ref = H_element
FEATURE [App::DocumentObjectGroupPython] C_element148  label="C_element : 093"  # scripted group (container) (typed FeaturePython)
  n = 9
  ref = C_element
FEATURE [App::DocumentObjectGroupPython] N_element067  label="N_element : 039"  # scripted group (container) (typed FeaturePython)
  n = 2
  ref = N_element
FEATURE [App::DocumentObjectGroupPython] O_element129  label="O_element : 9"  # scripted group (container) (typed FeaturePython)
  n = 9
  ref = O_element
FEATURE [App::DocumentObjectGroupPython] P_element018  label="P_element : 007"  # scripted group (container) (typed FeaturePython)
  n = 1
  ref = P_element
FEATURE [App::DocumentObjectGroupPython] G4_DNA_U  # scripted group (container) (typed FeaturePython)
  Dunit = g/cm3
  Dvalue = 1
  Group = -> [H_element138,C_element148,N_element067,O_element129,P_element018]
  conduct = 2
  density = 1
  expand = 3
  formula = G4_DNA_U
  name = G4_DNA_U
  specific = 4
FEATURE [App::DocumentObjectGroupPython] H_element139  label="H_element : 086"  # scripted group (container) (typed FeaturePython)
  n = 11
  ref = H_element
FEATURE [App::DocumentObjectGroupPython] C_element149  label="C_element : 094"  # scripted group (container) (typed FeaturePython)
  n = 10
  ref = C_element
FEATURE [App::DocumentObjectGroupPython] N_element068  label="N_element : 040"  # scripted group (container) (typed FeaturePython)
  n = 2
  ref = N_element
FEATURE [App::DocumentObjectGroupPython] O_element130  label="O_element : 081"  # scripted group (container) (typed FeaturePython)
  n = 9
  ref = O_element
FEATURE [App::DocumentObjectGroupPython] P_element019  label="P_element : 008"  # scripted group (container) (typed FeaturePython)
  n = 1
  ref = P_element
FEATURE [App::DocumentObjectGroupPython] G4_DNA_MU  # scripted group (container) (typed FeaturePython)
  Dunit = g/cm3
  Dvalue = 1
  Group = -> [H_element139,C_element149,N_element068,O_element130,P_element019]
  conduct = 2
  density = 1
  expand = 3
  formula = G4_DNA_MU
  name = G4_DNA_MU
  specific = 4
FEATURE [App::DocumentObjectGroupPython] BioChemical  # scripted group (container) (typed FeaturePython)
  Group = -> [G4_CYTOSINE,G4_THYMINE,G4_URACIL,G4_DNA_ADENINE,G4_DNA_GUANINE,G4_DNA_CYTOSINE,G4_DNA_THYMINE,G4_DNA_URACIL,G4_DNA_ADENOSINE,G4_DNA_GUANOSINE,G4_DNA_CYTIDINE,G4_DNA_URIDINE,G4_DNA_METHYLURIDINE,G4_DNA_MONOPHOSPHATE,G4_DNA_A,G4_DNA_G,G4_DNA_C,G4_DNA_U,G4_DNA_MU]
FEATURE [App::DocumentObjectGroupPython] G4Materials  # scripted group (container) (typed FeaturePython)
  Group = -> [NIST,Element,HEP,Space,BioChemical]
  version = 1
FEATURE [App::DocumentObjectGroupPython] Geant4  # scripted group (container) (typed FeaturePython)
  Group = -> [G4Isotopes,G4Elements,G4Materials]
FEATURE [App::DocumentObjectGroupPython] Materials  # scripted group (container) (typed FeaturePython)
  Group = -> [Geant4]
FEATURE [Part::FeaturePython] GDMLBox_WorldBox  # WARN: FeaturePython — macro-defined, semantics opaque (R4)
  lunit = 2
  material = 5
  x = 2350.01
  y = 2367.27
  z = 13016.7
FEATURE [Part::Cylinder] Cylinder
  Angle = 360
  AttacherType = Attacher::AttachEngine3D
  FirstAngle = 0
  Height = 200
  Placement = pos=(474,0,4850) rot=(0,0,1;0rad)
  Radius = 60
  SecondAngle = 0
FEATURE [Sketcher::SketchObject] Sketch001
  ArcFitTolerance = 0
  AttachmentSupport = -> [YZ_Plane001]
  FullyConstrained = false
  MakeInternals = false
  MapMode = 5
  Placement = pos=(0,0,0) rot=(0.57735,0.57735,0.57735;2.0944rad)
  sketch-geometry (36):
    g0: LineSegment StartX=345.196 StartY=1207.39 StartZ=0 EndX=345.196 EndY=4779.1 EndZ=0
    g1: LineSegment StartX=910.487 StartY=4896.42 StartZ=0 EndX=910.487 EndY=5006.42 EndZ=0
    g2: LineSegment StartX=435.196 StartY=4869.1 StartZ=0 EndX=445.196 EndY=4869.1 EndZ=0
    g3: LineSegment StartX=445.196 StartY=4869.1 StartZ=0 EndX=445.196 EndY=4896.42 EndZ=0
    g4: LineSegment StartX=445.196 StartY=4896.42 StartZ=0 EndX=910.487 EndY=4896.42 EndZ=0
    g5: LineSegment StartX=318.538 StartY=5006.42 StartZ=0 EndX=910.487 EndY=5006.42 EndZ=0
    g6: LineSegment StartX=175.531 StartY=1234.96 StartZ=0 EndX=318.538 EndY=1234.96 EndZ=0
    g7: LineSegment StartX=318.538 StartY=5006.42 StartZ=0 EndX=318.538 EndY=1234.96 EndZ=0
    g8: LineSegment StartX=0 StartY=39.215 StartZ=0 EndX=0 EndY=0 EndZ=0
    g9-g16: Circle [constr] x8 (B-spline internal-alignment scaffolding for g17; pole/knot coordinates omitted)
    g17: BSplineCurve PolesCount=8 KnotsCount=6 Degree=3 IsPeriodic=0
    g18-g23: GeomPoint [constr] x6 (B-spline internal-alignment scaffolding for g17; pole/knot coordinates omitted)
    g24: LineSegment StartX=175.531 StartY=1234.96 StartZ=0 EndX=175.531 EndY=838.896 EndZ=0
    g25-g29: Circle [constr] x5 (B-spline internal-alignment scaffolding for g30; pole/knot coordinates omitted)
    g30: BSplineCurve PolesCount=5 KnotsCount=3 Degree=3 IsPeriodic=0
    g31: GeomPoint [constr] X=175.531 Y=838.896 Z=0
    g32: GeomPoint [constr] X=165.058 Y=242.363 Z=0
    g33: GeomPoint [constr] X=0 Y=39.215 Z=0
    g34: ArcOfCircle CenterX=435.196 CenterY=4779.1 CenterZ=0 NormalX=0 NormalY=0 NormalZ=1 AngleXU=0 Radius=90 StartAngle=1.5708 EndAngle=3.14159
    g35: GeomPoint [constr] X=345.196 Y=4869.1 Z=0
  constraints (38):
    c: Vertical(g1)
    c: Horizontal(g2)
    c: Coincident(g2,g3)
    c: Vertical(g3)
    c: Coincident(g3,g4)
    c: Coincident(g4,g1)
    c: Horizontal(g4)
    c: Coincident(g5,g1)
    c: Horizontal(g5)
    c: Horizontal(g6)
    c: Coincident(g7,g5)
    c: Coincident(g7,g6)
    c: Vertical(g7)
    c: DistanceX(g35,g2) = 100
    c: Vertical(g8)
    c: Vertical(g0)
    c: Coincident(g17,g0)
    c: Weight(g9) = 1
    c: Equal(g9, g10-g16) x7
    c: Coincident(g17,g8)
    c: InternalAlignment(g9-g16 -> g17) x8
    c: InternalAlignment(g18-g23 -> g17) x6
    c: Coincident(g24,g6)
    c: Vertical(g24)
    c: Coincident(g30,g24)
    c: Weight(g25) = 1
    c: Equal(g25, g26-g29) x4
    c: Coincident(g30,g8)
    c: InternalAlignment(g25-g29 -> g30) x5
    c: InternalAlignment(g31,g30)
    c: InternalAlignment(g32,g30)
    c: InternalAlignment(g33,g30)
    c: Coincident(g8,g-1)
    c: PointOnObject(g35,g2)
    c: PointOnObject(g35,g0)
    c: Tangent(g2,g34) = 1.5708
    c: Tangent(g0,g34) = 1.5708
    c: Radius(g34) = 90
FEATURE [Part::Revolution] Revolve
  Angle = 360
  Axis = (0,0,1)
  Base = (0,0,0)
  FaceMakerClass = Part::FaceMakerBullseye
  Solid = true
  Source = -> Sketch001
  Symmetric = false
  material = 176
FEATURE [Part::Cut] Cut
  Base = -> Revolve
  Tool = -> Cylinder
FEATURE [App::Part] Bool_Cut
  Group = -> [Sketch001,Revolve,Cylinder,Cut]
  Origin = -> Origin004
FEATURE [App::Part] worldVOL
  Group = -> [GDMLBox_WorldBox,Bool_Cut]
  Origin = -> Origin
